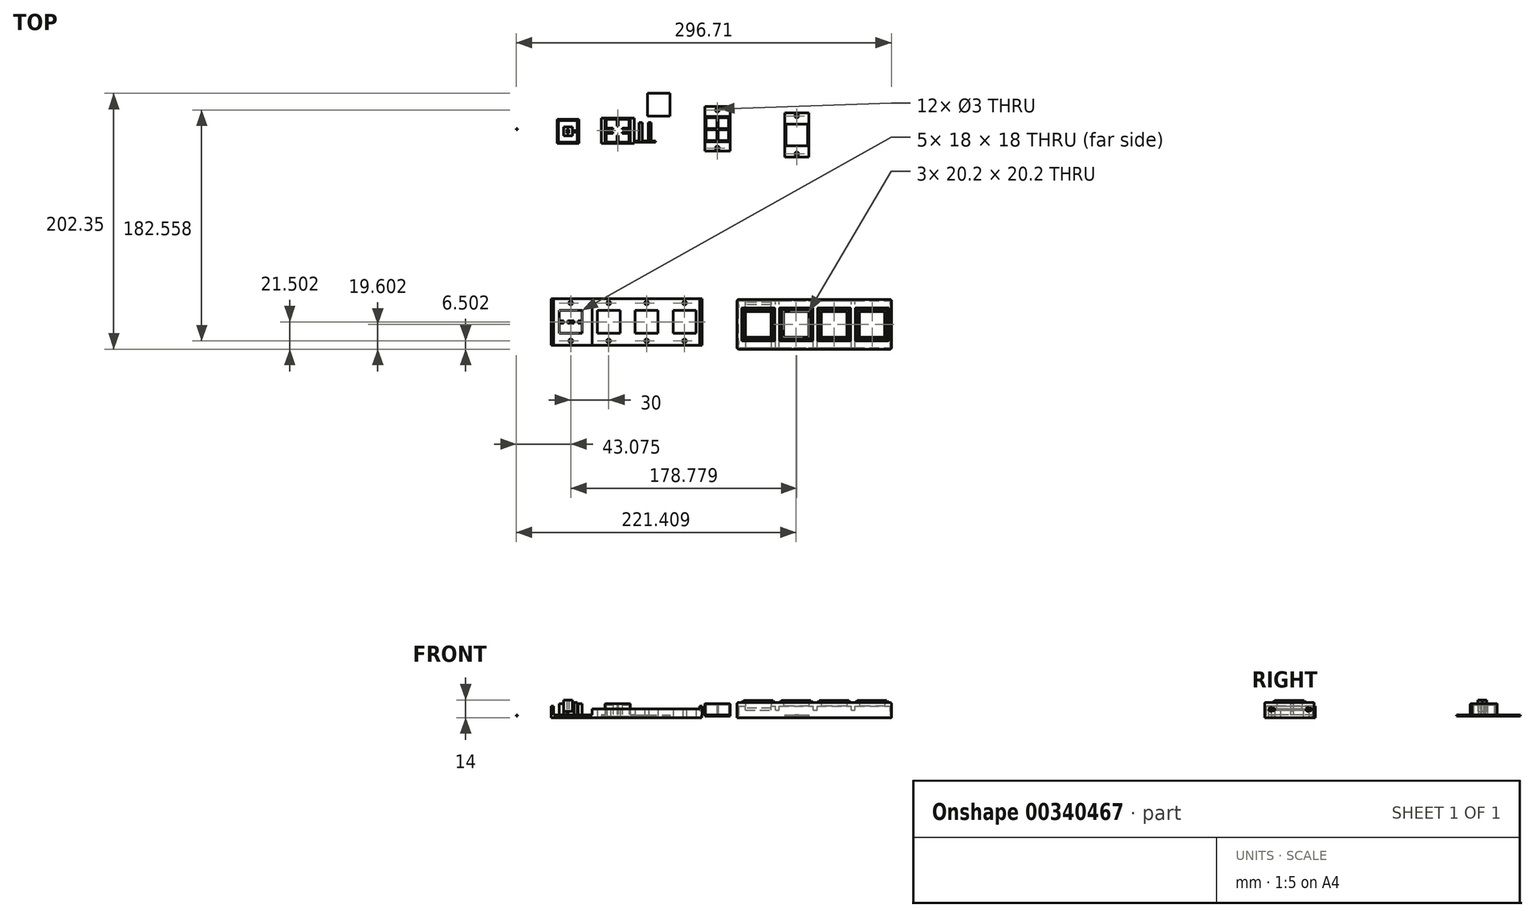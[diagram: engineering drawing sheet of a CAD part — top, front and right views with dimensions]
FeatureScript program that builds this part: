
annotation { "Feature Type Name" : "Feature", "Feature Type Description" : "" }
export const myFeature = defineFeature(function(context is Context, id is Id, definition is map)
    precondition{}
    {
        {
            var Q0;
            Q0=qCreatedBy(makeId("Top.planeOp"),FACE);
            var sketch = newSketch(context, id + "F0", { "sketchPlane" : qUnion([Q0])});
            skPoint(sketch, "E0.middle", {"position": v(0, 0) * mm});
            skLineSegment(sketch, "E1.bottom", {"start": v(10, -10) * mm, "end": v(-10, -10) * mm});
            skLineSegment(sketch, "E1.top", {"start": v(10, 10) * mm, "end": v(-10, 10) * mm});
            skLineSegment(sketch, "E1.left", {"start": v(10, -10) * mm, "end": v(10, 10) * mm});
            skLineSegment(sketch, "E1.right", {"start": v(-10, -10) * mm, "end": v(-10, 10) * mm});
            skSolve(sketch);
        }
        {
            var Q0;
            Q0=makeQuery(id+"F0.imprint","IMPRINT",FACE,{"disambiguationData":[TD([[makeQuery(id+"F0.imprint","IMPRINT",EDGE,{"derivedFrom":sQuery(id+"F0.wireOp",EDGE,"E1.bottom")}),-1.0]])]});
            extrude(context, id + "F1", {"entities" : qUnion([Q0]), "depth" : 10 * mm});
        }
        {
            var Q0;
            Q0=makeQuery(id+"F1.opExtrude","CAP_FACE",FACE,{"disambiguationData":[OSD([sQuery(id+"F0.wireOp",EDGE,"E1.bottom"),sQuery(id+"F0.wireOp",EDGE,"E1.top"),sQuery(id+"F0.wireOp",EDGE,"E1.left"),sQuery(id+"F0.wireOp",EDGE,"E1.right")])],"isStart":true});
            shell(context, id + "F2", {"entities" : qUnion([Q0]), "thickness" : 1 * mm});
        }
        {
            var Q0;
            Q0=qCreatedBy(makeId("Top.planeOp"),FACE);
            var sketch = newSketch(context, id + "F3", { "sketchPlane" : qUnion([Q0])});
            skLineSegment(sketch, "E2.bottom", {"start": v(0.5, -9) * mm, "end": v(-0.5, -9) * mm});
            skLineSegment(sketch, "E2.top", {"start": v(0.5, 9) * mm, "end": v(-0.5, 9) * mm});
            skLineSegment(sketch, "E2.left", {"start": v(0.5, -9) * mm, "end": v(0.5, -0.5) * mm});
            skLineSegment(sketch, "E2.right", {"start": v(-0.5, -9) * mm, "end": v(-0.5, -0.5) * mm});
            skLineSegment(sketch, "E3.bottom", {"start": v(9, 0.5) * mm, "end": v(0.5, 0.5) * mm});
            skLineSegment(sketch, "E3.top", {"start": v(9, -0.5) * mm, "end": v(0.5, -0.5) * mm});
            skLineSegment(sketch, "E3.left", {"start": v(9, 0.5) * mm, "end": v(9, -0.5) * mm});
            skLineSegment(sketch, "E3.right", {"start": v(-9, 0.5) * mm, "end": v(-9, -0.5) * mm});
            skLineSegment(sketch, "E4.trimOffspring", {"start": v(-0.5, 0.5) * mm, "end": v(-0.5, 9) * mm});
            skLineSegment(sketch, "E5.trimOffspring", {"start": v(-0.5, -0.5) * mm, "end": v(-9, -0.5) * mm});
            skLineSegment(sketch, "E6.trimOffspring", {"start": v(0.5, 0.5) * mm, "end": v(0.5, 9) * mm});
            skLineSegment(sketch, "E7.trimOffspring", {"start": v(-0.5, 0.5) * mm, "end": v(-9, 0.5) * mm});
            skSolve(sketch);
        }
        {
            var Q0;
            Q0=qSketchRegion(id+"F3",true);
            extrude(context, id + "F4", {"entities" : qUnion([Q0]), "operationType" : NewBodyOperationType.ADD, "depth" : 9 * mm});
        }
        {
            var Q0;
            Q0=qCreatedBy(makeId("Top.planeOp"),FACE);
            var sketch = newSketch(context, id + "F5", { "sketchPlane" : qUnion([Q0])});
            skLineSegment(sketch, "E8.bottom", {"start": v(-10, -9.5) * mm, "end": v(10, -9.5) * mm});
            skLineSegment(sketch, "E8.top", {"start": v(-10, -17.5) * mm, "end": v(10, -17.5) * mm});
            skLineSegment(sketch, "E8.left", {"start": v(-10, -9.5) * mm, "end": v(-10, -17.5) * mm});
            skLineSegment(sketch, "E8.right", {"start": v(10, -9.5) * mm, "end": v(10, -17.5) * mm});
            skLineSegment(sketch, "E9.bottom", {"start": v(-10, 10) * mm, "end": v(10, 10) * mm});
            skLineSegment(sketch, "E9.top", {"start": v(-10, 18) * mm, "end": v(10, 18) * mm});
            skLineSegment(sketch, "E9.left", {"start": v(-10, 10) * mm, "end": v(-10, 18) * mm});
            skLineSegment(sketch, "E9.right", {"start": v(10, 10) * mm, "end": v(10, 18) * mm});
            skLineSegment(sketch, "E10.bottom", {"start": v(-10, -9.5) * mm, "end": v(-13, -9.5) * mm, "construction": true});
            skLineSegment(sketch, "E10.top", {"start": v(-10, 10) * mm, "end": v(-13, 10) * mm, "construction": true});
            skLineSegment(sketch, "E10.left", {"start": v(-10, -9.5) * mm, "end": v(-10, 10) * mm});
            skLineSegment(sketch, "E10.right", {"start": v(-13, -9.5) * mm, "end": v(-13, 10) * mm, "construction": true});
            skLineSegment(sketch, "E11.bottom", {"start": v(10, -9.5) * mm, "end": v(13, -9.5) * mm, "construction": true});
            skLineSegment(sketch, "E11.top", {"start": v(10, 10) * mm, "end": v(13, 10) * mm, "construction": true});
            skLineSegment(sketch, "E11.left", {"start": v(10, -9.5) * mm, "end": v(10, 10) * mm});
            skLineSegment(sketch, "E11.right", {"start": v(13, -9.5) * mm, "end": v(13, 10) * mm, "construction": true});
            skCircle(sketch, "E12", {"center": v(0, 15) * mm, "radius": 1.5 * mm});
            skCircle(sketch, "E13", {"center": v(0, -15) * mm, "radius": 1.5 * mm});
            skSolve(sketch);
        }
        {
            var Q0;
            Q0=makeQuery(id+"F5.imprint","IMPRINT",FACE,{"disambiguationData":[TD([[makeQuery(id+"F5.imprint","IMPRINT",EDGE,{"derivedFrom":sQuery(id+"F5.wireOp",EDGE,"E10.bottom")}),-1.0]])]});
            var Q1;
            Q1=makeQuery(id+"F5.imprint","IMPRINT",FACE,{"disambiguationData":[TD([[makeQuery(id+"F5.imprint","IMPRINT",EDGE,{"derivedFrom":sQuery(id+"F5.wireOp",EDGE,"E8.bottom")}),-1.0]])]});
            var Q2;
            Q2=makeQuery(id+"F5.imprint","IMPRINT",FACE,{"disambiguationData":[TD([[makeQuery(id+"F5.imprint","IMPRINT",EDGE,{"derivedFrom":sQuery(id+"F5.wireOp",EDGE,"E11.bottom")}),1.0]])]});
            var Q3;
            Q3=makeQuery(id+"F5.imprint","IMPRINT",FACE,{"disambiguationData":[TD([[makeQuery(id+"F5.imprint","IMPRINT",EDGE,{"derivedFrom":sQuery(id+"F5.wireOp",EDGE,"E9.bottom")}),1.0]])]});
            extrude(context, id + "F6", {"entities" : qUnion([Q0, Q1, Q2, Q3]), "operationType" : NewBodyOperationType.ADD, "depth" : 1 * mm});
        }
        {
            var Q0;
            Q0=qCreatedBy(makeId("Top.planeOp"),FACE);
            var sketch = newSketch(context, id + "F7", { "sketchPlane" : qUnion([Q0])});
            skLineSegment(sketch, "E14.bottom", {"start": v(53.3, 4.9) * mm, "end": v(72.3, 4.9) * mm});
            skLineSegment(sketch, "E14.top", {"start": v(53.3, -14.1) * mm, "end": v(72.3, -14.1) * mm});
            skLineSegment(sketch, "E14.left", {"start": v(53.3, 4.9) * mm, "end": v(53.3, -14.1) * mm});
            skLineSegment(sketch, "E14.right", {"start": v(72.3, 4.9) * mm, "end": v(72.3, -14.1) * mm});
            skLineSegment(sketch, "E15.top", {"start": v(53.3, 12.9) * mm, "end": v(72.3, 12.9) * mm});
            skLineSegment(sketch, "E15.left", {"start": v(53.3, 4.9) * mm, "end": v(53.3, 12.9) * mm});
            skLineSegment(sketch, "E15.right", {"start": v(72.3, 4.9) * mm, "end": v(72.3, 12.9) * mm});
            skLineSegment(sketch, "E16.top", {"start": v(53.3, -22.1) * mm, "end": v(72.3, -22.1) * mm});
            skLineSegment(sketch, "E16.left", {"start": v(53.3, -14.1) * mm, "end": v(53.3, -22.1) * mm});
            skLineSegment(sketch, "E16.right", {"start": v(72.3, -14.1) * mm, "end": v(72.3, -22.1) * mm});
            skLineSegment(sketch, "E17.bottom", {"start": v(62.05, 4.9) * mm, "end": v(63.55, 4.9) * mm, "construction": true});
            skLineSegment(sketch, "E17.top", {"start": v(62.05, -14.1) * mm, "end": v(63.55, -14.1) * mm, "construction": true});
            skLineSegment(sketch, "E17.left", {"start": v(62.05, 4.9) * mm, "end": v(62.05, -14.1) * mm, "construction": true});
            skLineSegment(sketch, "E17.right", {"start": v(63.55, 4.9) * mm, "end": v(63.55, -14.1) * mm, "construction": true});
            skLineSegment(sketch, "E18.bottom", {"start": v(53.3, -3.86) * mm, "end": v(54.3, -3.86) * mm, "construction": true});
            skLineSegment(sketch, "E18.top", {"start": v(53.3, -5.36) * mm, "end": v(57.43, -5.36) * mm, "construction": true});
            skLineSegment(sketch, "E18.left", {"start": v(53.3, -3.86) * mm, "end": v(53.3, -5.36) * mm, "construction": true});
            skLineSegment(sketch, "E18.right", {"start": v(72.3, -3.86) * mm, "end": v(72.3, -5.36) * mm, "construction": true});
            skLineSegment(sketch, "E19.0", {"start": v(54.3, 3.9) * mm, "end": v(71.3, 3.9) * mm});
            skLineSegment(sketch, "E19.1", {"start": v(54.3, 3.9) * mm, "end": v(54.3, -13.1) * mm});
            skLineSegment(sketch, "E19.2", {"start": v(54.3, -13.1) * mm, "end": v(71.3, -13.1) * mm});
            skLineSegment(sketch, "E19.3", {"start": v(71.3, 3.9) * mm, "end": v(71.3, -13.1) * mm});
            skCircle(sketch, "E20", {"center": v(62.8, 10.4) * mm, "radius": 1.5 * mm});
            skPoint(sketch, "E21", {"position": v(62.8, 4.9) * mm});
            skLineSegment(sketch, "E22.bottom", {"start": v(63.3, -5.1) * mm, "end": v(62.3, -5.1) * mm, "construction": true});
            skLineSegment(sketch, "E22.top", {"start": v(63.3, -4.1) * mm, "end": v(62.3, -4.1) * mm, "construction": true});
            skLineSegment(sketch, "E22.left", {"start": v(63.3, -5.1) * mm, "end": v(63.3, -4.1) * mm, "construction": true});
            skLineSegment(sketch, "E22.right", {"start": v(62.3, -5.1) * mm, "end": v(62.3, -4.1) * mm, "construction": true});
            skPoint(sketch, "E22.middle", {"position": v(62.8, -4.6) * mm});
            skPoint(sketch, "E22.middle.positionSnap0", {"position": v(62.05, -4.6) * mm});
            skPoint(sketch, "E22.middle.positionSnap1", {"position": v(62.8, -3.86) * mm});
            skPoint(sketch, "E22.centerSnap0", {"position": v(62.05, -4.6) * mm});
            skPoint(sketch, "E22.centerSnap1", {"position": v(62.8, -3.86) * mm});
            skCircle(sketch, "E23", {"center": v(62.8, -19.6) * mm, "radius": 1.5 * mm});
            skPoint(sketch, "E23.centerSnap0", {"position": v(62.8, 12.9) * mm});
            skLineSegment(sketch, "E24.bottom", {"start": v(57.43, 3.9) * mm, "end": v(58.93, 3.9) * mm});
            skLineSegment(sketch, "E24.top", {"start": v(57.43, -13.1) * mm, "end": v(58.93, -13.1) * mm});
            skLineSegment(sketch, "E24.left", {"start": v(57.43, 3.9) * mm, "end": v(57.43, -3.86) * mm});
            skLineSegment(sketch, "E24.right", {"start": v(58.93, 3.9) * mm, "end": v(58.93, -3.86) * mm});
            skLineSegment(sketch, "E25.bottom", {"start": v(66.68, 3.9) * mm, "end": v(68.18, 3.9) * mm});
            skLineSegment(sketch, "E25.top", {"start": v(66.68, -13.1) * mm, "end": v(68.18, -13.1) * mm});
            skLineSegment(sketch, "E25.left", {"start": v(66.68, 3.9) * mm, "end": v(66.68, -3.86) * mm});
            skLineSegment(sketch, "E25.right", {"start": v(68.18, 3.9) * mm, "end": v(68.18, -3.86) * mm});
            skLineSegment(sketch, "E26.bottom", {"start": v(54.3, -3.86) * mm, "end": v(57.43, -3.86) * mm});
            skLineSegment(sketch, "E26.top", {"start": v(54.3, -5.36) * mm, "end": v(57.43, -5.36) * mm});
            skLineSegment(sketch, "E26.left", {"start": v(54.3, -3.86) * mm, "end": v(54.3, -5.36) * mm});
            skLineSegment(sketch, "E26.right", {"start": v(71.3, -3.86) * mm, "end": v(71.3, -5.36) * mm});
            skLineSegment(sketch, "E27.trimOffspring", {"start": v(58.93, -3.86) * mm, "end": v(66.68, -3.86) * mm, "construction": true});
            skLineSegment(sketch, "E28.trimOffspring", {"start": v(58.93, -3.86) * mm, "end": v(66.68, -3.86) * mm});
            skLineSegment(sketch, "E29.trimOffspring", {"start": v(57.43, -5.36) * mm, "end": v(57.43, -13.1) * mm});
            skLineSegment(sketch, "E30.trimOffspring", {"start": v(58.93, -5.36) * mm, "end": v(58.93, -13.1) * mm});
            skLineSegment(sketch, "E31.trimOffspring", {"start": v(58.93, -5.36) * mm, "end": v(66.68, -5.36) * mm, "construction": true});
            skLineSegment(sketch, "E32.trimOffspring", {"start": v(58.93, -5.36) * mm, "end": v(66.68, -5.36) * mm});
            skLineSegment(sketch, "E33.trimOffspring", {"start": v(68.18, -3.86) * mm, "end": v(72.3, -3.86) * mm, "construction": true});
            skLineSegment(sketch, "E34.trimOffspring", {"start": v(66.68, -5.36) * mm, "end": v(66.68, -13.1) * mm});
            skLineSegment(sketch, "E35.trimOffspring", {"start": v(68.18, -5.36) * mm, "end": v(72.3, -5.36) * mm, "construction": true});
            skLineSegment(sketch, "E36.trimOffspring", {"start": v(68.18, -5.36) * mm, "end": v(68.18, -13.1) * mm});
            skLineSegment(sketch, "E37.trimOffspring", {"start": v(68.18, -3.86) * mm, "end": v(71.3, -3.86) * mm});
            skLineSegment(sketch, "E38.trimOffspring", {"start": v(68.18, -5.36) * mm, "end": v(71.3, -5.36) * mm});
            skLineSegment(sketch, "E39.bottom", {"start": v(55.04, 3.07) * mm, "end": v(61.04, 3.07) * mm, "construction": true});
            skLineSegment(sketch, "E39.top", {"start": v(55.04, -2.93) * mm, "end": v(61.04, -2.93) * mm, "construction": true});
            skLineSegment(sketch, "E39.left", {"start": v(55.04, 3.07) * mm, "end": v(55.04, -2.93) * mm, "construction": true});
            skLineSegment(sketch, "E39.right", {"start": v(61.04, 3.07) * mm, "end": v(61.04, -2.93) * mm, "construction": true});
            skLineSegment(sketch, "E40.bottom", {"start": v(64.3, 3.07) * mm, "end": v(70.3, 3.07) * mm, "construction": true});
            skLineSegment(sketch, "E40.top", {"start": v(64.3, -2.93) * mm, "end": v(70.3, -2.93) * mm, "construction": true});
            skLineSegment(sketch, "E40.left", {"start": v(64.3, 3.07) * mm, "end": v(64.3, -2.93) * mm, "construction": true});
            skLineSegment(sketch, "E40.right", {"start": v(70.3, 3.07) * mm, "end": v(70.3, -2.93) * mm, "construction": true});
            skSolve(sketch);
        }
        {
            var Q0;
            Q0=makeQuery(id+"F7.imprint","IMPRINT",FACE,{"disambiguationData":[TD([[makeQuery(id+"F7.imprint","IMPRINT",EDGE,{"derivedFrom":sQuery(id+"F7.wireOp",EDGE,"E14.left")}),1.0]])]});
            var Q1;
            Q1=makeQuery(id+"F7.imprint","IMPRINT",FACE,{"disambiguationData":[TD([[makeQuery(id+"F7.imprint","IMPRINT",EDGE,{"derivedFrom":sQuery(id+"F7.wireOp",EDGE,"E14.bottom")}),1.0]])]});
            var Q2;
            Q2=makeQuery(id+"F7.imprint","IMPRINT",FACE,{"disambiguationData":[TD([[makeQuery(id+"F7.imprint","IMPRINT",EDGE,{"derivedFrom":sQuery(id+"F7.wireOp",EDGE,"MVN2uy9p-aqT3-YTcf-EiQD-pbnfHAAz3MAc.bottom")}),-1.0]])]});
            var Q3;
            Q3=makeQuery(id+"F7.imprint","IMPRINT",FACE,{"disambiguationData":[TD([[makeQuery(id+"F7.imprint","IMPRINT",EDGE,{"derivedFrom":sQuery(id+"F7.wireOp",EDGE,"sKF5d9FJ-0LFq-fu9g-diTO-PrwaPXYM0bzY.bottom")}),-1.0]])]});
            var Q4;
            Q4=makeQuery(id+"F7.imprint","IMPRINT",FACE,{"disambiguationData":[TD([[makeQuery(id+"F7.imprint","IMPRINT",EDGE,{"derivedFrom":sQuery(id+"F7.wireOp",EDGE,"E14.top")}),-1.0]])]});
            var Q5;
            Q5=makeQuery(id+"F7.imprint","IMPRINT",FACE,{"disambiguationData":[TD([[makeQuery(id+"F7.imprint","IMPRINT",EDGE,{"derivedFrom":sQuery(id+"F7.wireOp",EDGE,"E24.bottom")}),-1.0]])]});
            var Q6;
            Q6=makeQuery(id+"F7.imprint","IMPRINT",FACE,{"disambiguationData":[TD([[makeQuery(id+"F7.imprint","IMPRINT",EDGE,{"derivedFrom":sQuery(id+"F7.wireOp",EDGE,"E25.bottom")}),-1.0]])]});
            extrude(context, id + "F8", {"entities" : qUnion([Q0, Q1, Q2, Q3, Q4, Q5, Q6]), "depth" : 1 * mm});
        }
        {
            var Q0;
            Q0=qCreatedBy(makeId("Top.planeOp"),FACE);
            var sketch = newSketch(context, id + "F9", { "sketchPlane" : qUnion([Q0])});
            skLineSegment(sketch, "E41.bottom", {"start": v(-88.88, 8.7) * mm, "end": v(-68.88, 8.7) * mm});
            skLineSegment(sketch, "E41.top", {"start": v(-88.88, -11.3) * mm, "end": v(-68.88, -11.3) * mm});
            skLineSegment(sketch, "E41.left", {"start": v(-88.88, 8.7) * mm, "end": v(-88.88, -11.3) * mm});
            skLineSegment(sketch, "E41.right", {"start": v(-68.88, 8.7) * mm, "end": v(-68.88, -11.3) * mm});
            skSolve(sketch);
        }
        {
            var Q0;
            Q0=makeQuery(id+"F9.imprint","IMPRINT",FACE,{"disambiguationData":[TD([[makeQuery(id+"F9.imprint","IMPRINT",EDGE,{"derivedFrom":sQuery(id+"F9.wireOp",EDGE,"E41.bottom")}),-1.0]])]});
            extrude(context, id + "F10", {"entities" : qUnion([Q0]), "depth" : 10 * mm});
        }
        {
            var Q0;
            Q0=makeQuery(id+"F15.boolean.opBoolean","MERGE",FACE,{"derivedFrom":[makeQuery(id+"F10.opExtrude","CAP_FACE",FACE,{"disambiguationData":[OSD([sQuery(id+"F9.wireOp",EDGE,"E41.bottom"),sQuery(id+"F9.wireOp",EDGE,"E41.top"),sQuery(id+"F9.wireOp",EDGE,"E41.left"),sQuery(id+"F9.wireOp",EDGE,"E41.right")])],"isStart":true}),makeQuery(id+"F15.opExtrude","CAP_FACE",FACE,{"disambiguationData":[OSD([sQuery(id+"F14.wireOp",EDGE,"E49.bottom"),sQuery(id+"F14.wireOp",EDGE,"E49.top"),sQuery(id+"F14.wireOp",EDGE,"E49.left"),sQuery(id+"F14.wireOp",EDGE,"E49.right"),sQuery(id+"F14.wireOp",EDGE,"E50.trimOffspring"),sQuery(id+"F14.wireOp",EDGE,"E52.trimOffspring"),sQuery(id+"F14.wireOp",EDGE,"E54"),sQuery(id+"F14.wireOp",EDGE,"E55"),sQuery(id+"F14.wireOp",EDGE,"E56.bottom"),sQuery(id+"F14.wireOp",EDGE,"E56.top"),sQuery(id+"F14.wireOp",EDGE,"E56.left"),sQuery(id+"F14.wireOp",EDGE,"E57.bottom"),sQuery(id+"F14.wireOp",EDGE,"E57.top"),sQuery(id+"F14.wireOp",EDGE,"E57.left"),sQuery(id+"F14.wireOp",EDGE,"E58.bottom"),sQuery(id+"F14.wireOp",EDGE,"E58.top"),sQuery(id+"F14.wireOp",EDGE,"E58.right"),sQuery(id+"F14.wireOp",EDGE,"E59.bottom"),sQuery(id+"F14.wireOp",EDGE,"E59.top"),sQuery(id+"F14.wireOp",EDGE,"E59.right")])],"isStart":true})]});
            var sketch = newSketch(context, id + "F11", { "sketchPlane" : qUnion([Q0])});
            skLineSegment(sketch, "E42.bottom", {"start": v(-88.88, 11.3) * mm, "end": v(-68.88, 11.3) * mm});
            skLineSegment(sketch, "E42.top", {"start": v(-88.88, 14.3) * mm, "end": v(-68.88, 14.3) * mm, "construction": true});
            skLineSegment(sketch, "E42.left", {"start": v(-88.88, 11.3) * mm, "end": v(-88.88, 14.3) * mm, "construction": true});
            skLineSegment(sketch, "E42.right", {"start": v(-68.88, 11.3) * mm, "end": v(-68.88, 14.3) * mm, "construction": true});
            skLineSegment(sketch, "E43.bottom", {"start": v(-88.88, -8.7) * mm, "end": v(-68.88, -8.7) * mm});
            skLineSegment(sketch, "E43.top", {"start": v(-88.88, -11.7) * mm, "end": v(-68.88, -11.7) * mm});
            skLineSegment(sketch, "E43.left", {"start": v(-88.88, -8.7) * mm, "end": v(-88.88, -11.7) * mm, "construction": true});
            skLineSegment(sketch, "E43.right", {"start": v(-68.88, -8.7) * mm, "end": v(-68.88, -11.7) * mm, "construction": true});
            skLineSegment(sketch, "E44.bottom", {"start": v(-88.88, -8.7) * mm, "end": v(-91.88, -8.7) * mm});
            skLineSegment(sketch, "E44.top", {"start": v(-88.88, 11.3) * mm, "end": v(-91.88, 11.3) * mm});
            skLineSegment(sketch, "E44.left", {"start": v(-88.88, -8.7) * mm, "end": v(-88.88, 11.3) * mm});
            skLineSegment(sketch, "E44.right", {"start": v(-91.88, -8.7) * mm, "end": v(-91.88, 11.3) * mm});
            skLineSegment(sketch, "E45.bottom", {"start": v(-68.88, -8.7) * mm, "end": v(-65.88, -8.7) * mm});
            skLineSegment(sketch, "E45.top", {"start": v(-68.88, 11.3) * mm, "end": v(-65.88, 11.3) * mm});
            skLineSegment(sketch, "E45.left", {"start": v(-68.88, -8.7) * mm, "end": v(-68.88, 11.3) * mm});
            skLineSegment(sketch, "E45.right", {"start": v(-65.88, -8.7) * mm, "end": v(-65.88, 11.3) * mm});
            skLineSegment(sketch, "E46.bottom", {"start": v(-88.88, -11.7) * mm, "end": v(-68.88, -11.7) * mm, "construction": true});
            skLineSegment(sketch, "E46.top", {"start": v(-88.88, -16.7) * mm, "end": v(-68.88, -16.7) * mm, "construction": true});
            skLineSegment(sketch, "E46.left", {"start": v(-88.88, -11.7) * mm, "end": v(-88.88, -16.7) * mm, "construction": true});
            skLineSegment(sketch, "E46.right", {"start": v(-68.88, -11.7) * mm, "end": v(-68.88, -16.7) * mm, "construction": true});
            skCircle(sketch, "E47", {"center": v(-78.88, -13.7) * mm, "radius": 1.5 * mm, "construction": true});
            skSolve(sketch);
        }
        {
            var Q0;
            Q0=qSketchRegion(id+"F11",true);
            extrude(context, id + "F12", {"entities" : qUnion([Q0]), "operationType" : NewBodyOperationType.ADD, "oppositeDirection" : true, "depth" : 0.95 * mm});
        }
        {
            var Q0;
            Q0=makeQuery(id+"F10.opExtrude","CAP_FACE",FACE,{"disambiguationData":[OSD([sQuery(id+"F9.wireOp",EDGE,"E41.bottom"),sQuery(id+"F9.wireOp",EDGE,"E41.top"),sQuery(id+"F9.wireOp",EDGE,"E41.left"),sQuery(id+"F9.wireOp",EDGE,"E41.right")])],"isStart":true});
            shell(context, id + "F13", {"entities" : qUnion([Q0]), "thickness" : 1 * mm});
        }
        {
            var Q0;
            Q0=qCreatedBy(makeId("Top.planeOp"),FACE);
            var sketch = newSketch(context, id + "F14", { "sketchPlane" : qUnion([Q0])});
            skLineSegment(sketch, "E48.bottom", {"start": v(-87.88, -0.2) * mm, "end": v(-79.38, -0.2) * mm, "construction": true});
            skLineSegment(sketch, "E48.top", {"start": v(-87.88, -2.4) * mm, "end": v(-79.38, -2.4) * mm, "construction": true});
            skLineSegment(sketch, "E48.left", {"start": v(-87.88, -0.2) * mm, "end": v(-87.88, -2.4) * mm, "construction": true});
            skLineSegment(sketch, "E48.right", {"start": v(-69.88, -0.2) * mm, "end": v(-69.88, -2.4) * mm, "construction": true});
            skLineSegment(sketch, "E49.bottom", {"start": v(-79.38, 7.7) * mm, "end": v(-78.38, 7.7) * mm});
            skLineSegment(sketch, "E49.top", {"start": v(-79.38, -10.3) * mm, "end": v(-78.38, -10.3) * mm});
            skLineSegment(sketch, "E49.left", {"start": v(-79.38, 7.7) * mm, "end": v(-79.38, -0.2) * mm});
            skLineSegment(sketch, "E49.right", {"start": v(-78.38, 7.7) * mm, "end": v(-78.38, -0.2) * mm});
            skLineSegment(sketch, "E50.trimOffspring", {"start": v(-79.38, -10.3) * mm, "end": v(-79.38, -2.4) * mm});
            skLineSegment(sketch, "E51.trimOffspring", {"start": v(-78.38, -0.2) * mm, "end": v(-69.88, -0.2) * mm, "construction": true});
            skLineSegment(sketch, "E52.trimOffspring", {"start": v(-78.38, -2.4) * mm, "end": v(-78.38, -10.3) * mm});
            skLineSegment(sketch, "E53.trimOffspring", {"start": v(-78.38, -2.4) * mm, "end": v(-69.88, -2.4) * mm, "construction": true});
            skLineSegment(sketch, "E54", {"start": v(-79.38, -2.4) * mm, "end": v(-79.38, -0.2) * mm});
            skLineSegment(sketch, "E55", {"start": v(-78.38, -2.4) * mm, "end": v(-78.38, -0.2) * mm});
            skLineSegment(sketch, "E56.bottom", {"start": v(-87.88, -2.4) * mm, "end": v(-79.38, -2.4) * mm});
            skLineSegment(sketch, "E56.top", {"start": v(-87.88, -3.3) * mm, "end": v(-79.38, -3.3) * mm});
            skLineSegment(sketch, "E56.left", {"start": v(-87.88, -2.4) * mm, "end": v(-87.88, -3.3) * mm});
            skLineSegment(sketch, "E56.right", {"start": v(-79.38, -2.4) * mm, "end": v(-79.38, -3.3) * mm});
            skLineSegment(sketch, "E57.bottom", {"start": v(-87.88, -0.2) * mm, "end": v(-79.38, -0.2) * mm});
            skLineSegment(sketch, "E57.top", {"start": v(-87.88, 0.7) * mm, "end": v(-79.38, 0.7) * mm});
            skLineSegment(sketch, "E57.left", {"start": v(-87.88, -0.2) * mm, "end": v(-87.88, 0.7) * mm});
            skLineSegment(sketch, "E57.right", {"start": v(-79.38, -0.2) * mm, "end": v(-79.38, 0.7) * mm});
            skLineSegment(sketch, "E58.bottom", {"start": v(-78.38, -3.3) * mm, "end": v(-69.88, -3.3) * mm});
            skLineSegment(sketch, "E58.top", {"start": v(-78.38, -2.4) * mm, "end": v(-69.88, -2.4) * mm});
            skLineSegment(sketch, "E58.left", {"start": v(-78.38, -3.3) * mm, "end": v(-78.38, -2.4) * mm});
            skLineSegment(sketch, "E58.right", {"start": v(-69.88, -3.3) * mm, "end": v(-69.88, -2.4) * mm});
            skLineSegment(sketch, "E59.bottom", {"start": v(-78.38, -0.2) * mm, "end": v(-69.88, -0.2) * mm});
            skLineSegment(sketch, "E59.top", {"start": v(-78.38, 0.7) * mm, "end": v(-69.88, 0.7) * mm});
            skLineSegment(sketch, "E59.left", {"start": v(-78.38, -0.2) * mm, "end": v(-78.38, 0.7) * mm});
            skLineSegment(sketch, "E59.right", {"start": v(-69.88, -0.2) * mm, "end": v(-69.88, 0.7) * mm});
            skSolve(sketch);
        }
        {
            var Q0;
            Q0=makeQuery(id+"F14.imprint","IMPRINT",FACE,{"disambiguationData":[TD([[makeQuery(id+"F14.imprint","IMPRINT",EDGE,{"derivedFrom":sQuery(id+"F14.wireOp",EDGE,"E49.bottom")}),-1.0]])]});
            var Q1;
            Q1=makeQuery(id+"F14.imprint","IMPRINT",FACE,{"disambiguationData":[TD([[makeQuery(id+"F14.imprint","IMPRINT",EDGE,{"derivedFrom":sQuery(id+"F14.wireOp",EDGE,"E56.bottom")}),-1.0]])]});
            var Q2;
            Q2=makeQuery(id+"F14.imprint","IMPRINT",FACE,{"disambiguationData":[TD([[makeQuery(id+"F14.imprint","IMPRINT",EDGE,{"derivedFrom":sQuery(id+"F14.wireOp",EDGE,"E57.bottom")}),1.0]])]});
            var Q3;
            Q3=makeQuery(id+"F14.imprint","IMPRINT",FACE,{"disambiguationData":[TD([[makeQuery(id+"F14.imprint","IMPRINT",EDGE,{"derivedFrom":sQuery(id+"F14.wireOp",EDGE,"E59.bottom")}),1.0]])]});
            var Q4;
            Q4=makeQuery(id+"F14.imprint","IMPRINT",FACE,{"disambiguationData":[TD([[makeQuery(id+"F14.imprint","IMPRINT",EDGE,{"derivedFrom":sQuery(id+"F14.wireOp",EDGE,"E58.bottom")}),1.0]])]});
            var Q5;
            Q5=sQuery(id+"F14.wireOp",EDGE,"E49.left");
            var Q6;
            Q6=sQuery(id+"F14.wireOp",EDGE,"E50.trimOffspring");
            var Q7;
            Q7=sQuery(id+"F14.wireOp",EDGE,"E48.top");
            var Q8;
            Q8=sQuery(id+"F14.wireOp",EDGE,"E51.trimOffspring");
            var Q9;
            Q9=sQuery(id+"F14.wireOp",EDGE,"E49.bottom");
            var Q10;
            Q10=sQuery(id+"F14.wireOp",EDGE,"E49.right");
            var Q11;
            Q11=sQuery(id+"F14.wireOp",EDGE,"E49.top");
            var Q12;
            Q12=sQuery(id+"F14.wireOp",EDGE,"E48.bottom");
            var Q13;
            Q13=sQuery(id+"F14.wireOp",EDGE,"E52.trimOffspring");
            var Q14;
            Q14=sQuery(id+"F14.wireOp",EDGE,"E53.trimOffspring");
            var Q15;
            Q15=sQuery(id+"F14.wireOp",EDGE,"E48.right");
            var Q16;
            Q16=sQuery(id+"F14.wireOp",EDGE,"E48.left");
            extrude(context, id + "F15", {"entities" : qUnion([Q0, Q1, Q2, Q3, Q4]), "operationType" : NewBodyOperationType.ADD, "surfaceEntities" : qUnion([Q5, Q6, Q7, Q8, Q9, Q10, Q11, Q12, Q13, Q14, Q15, Q16]), "depth" : 9 * mm});
        }
        {
            var Q0;
            Q0=makeQuery(id+"F15.boolean.opBoolean","MERGE",FACE,{"derivedFrom":[makeQuery(id+"F10.opExtrude","CAP_FACE",FACE,{"disambiguationData":[OSD([sQuery(id+"F9.wireOp",EDGE,"E41.bottom"),sQuery(id+"F9.wireOp",EDGE,"E41.top"),sQuery(id+"F9.wireOp",EDGE,"E41.left"),sQuery(id+"F9.wireOp",EDGE,"E41.right")])],"isStart":true}),makeQuery(id+"F15.opExtrude","CAP_FACE",FACE,{"disambiguationData":[OSD([sQuery(id+"F14.wireOp",EDGE,"E48.bottom"),sQuery(id+"F14.wireOp",EDGE,"E48.top"),sQuery(id+"F14.wireOp",EDGE,"E48.left"),sQuery(id+"F14.wireOp",EDGE,"E48.right"),sQuery(id+"F14.wireOp",EDGE,"E49.bottom"),sQuery(id+"F14.wireOp",EDGE,"E49.top"),sQuery(id+"F14.wireOp",EDGE,"E49.left"),sQuery(id+"F14.wireOp",EDGE,"E49.right"),sQuery(id+"F14.wireOp",EDGE,"E50.trimOffspring"),sQuery(id+"F14.wireOp",EDGE,"E51.trimOffspring"),sQuery(id+"F14.wireOp",EDGE,"E52.trimOffspring"),sQuery(id+"F14.wireOp",EDGE,"E53.trimOffspring")])],"isStart":true})]});
            var sketch = newSketch(context, id + "F16", { "sketchPlane" : qUnion([Q0])});
            skLineSegment(sketch, "E60.bottom", {"start": v(-75.28, -2.3) * mm, "end": v(-82.48, -2.3) * mm});
            skLineSegment(sketch, "E60.top", {"start": v(-75.28, 4.9) * mm, "end": v(-82.48, 4.9) * mm});
            skLineSegment(sketch, "E60.left", {"start": v(-75.28, -2.3) * mm, "end": v(-75.28, 4.9) * mm});
            skLineSegment(sketch, "E60.right", {"start": v(-82.48, -2.3) * mm, "end": v(-82.48, 4.9) * mm});
            skPoint(sketch, "E60.middle.positionSnap1", {"position": v(-88.88, 1.8) * mm});
            skSolve(sketch);
        }
        {
            var Q0;
            {var subQ1=makeQuery(id+"F15.opExtrude","CAP_EDGE",EDGE,{"disambiguationData":[OSD([sQuery(id+"F14.wireOp",EDGE,"E49.right")])],"isStart":true});var subQ3=sQuery(id+"F16.wireOp",EDGE,"E60.bottom");var subQ4=makeQuery(id+"F16.imprint","INTERSECT",VERTEX,{"derivedFrom":[subQ1,subQ3]});Q0=makeQuery(id+"F16.imprint","IMPRINT",FACE,{"disambiguationData":[TD([[makeQuery(id+"F16.imprint","IMPRINT",EDGE,{"disambiguationData":[TD([[subQ4,-1.0]])],"derivedFrom":subQ3}),-1.0]])]});}
            extrude(context, id + "F17", {"entities" : qUnion([Q0]), "operationType" : NewBodyOperationType.REMOVE, "oppositeDirection" : true, "depth" : 9 * mm});
        }
        {
            var Q0;
            Q0=qCreatedBy(makeId("Top.planeOp"),FACE);
            var sketch = newSketch(context, id + "F18", { "sketchPlane" : qUnion([Q0])});
            skLineSegment(sketch, "E61.bottom", {"start": v(-126.7, 7.66) * mm, "end": v(-109.7, 7.66) * mm});
            skLineSegment(sketch, "E61.top", {"start": v(-126.7, -11.34) * mm, "end": v(-109.7, -11.34) * mm});
            skLineSegment(sketch, "E61.left", {"start": v(-126.7, 7.66) * mm, "end": v(-126.7, -11.34) * mm});
            skLineSegment(sketch, "E61.right", {"start": v(-109.7, 7.66) * mm, "end": v(-109.7, -11.34) * mm});
            skLineSegment(sketch, "E62.top", {"start": v(-126.7, 15.66) * mm, "end": v(-109.7, 15.66) * mm});
            skLineSegment(sketch, "E62.left", {"start": v(-126.7, 7.66) * mm, "end": v(-126.7, 15.66) * mm});
            skLineSegment(sketch, "E62.right", {"start": v(-109.7, 7.66) * mm, "end": v(-109.7, 15.66) * mm});
            skLineSegment(sketch, "E63.top", {"start": v(-126.7, -19.34) * mm, "end": v(-109.7, -19.34) * mm});
            skLineSegment(sketch, "E63.left", {"start": v(-126.7, -11.34) * mm, "end": v(-126.7, -19.34) * mm});
            skLineSegment(sketch, "E63.right", {"start": v(-109.7, -11.34) * mm, "end": v(-109.7, -19.34) * mm});
            skLineSegment(sketch, "E64.bottom", {"start": v(-118.94, 7.66) * mm, "end": v(-117.44, 7.66) * mm, "construction": true});
            skLineSegment(sketch, "E64.top", {"start": v(-118.94, -11.34) * mm, "end": v(-117.44, -11.34) * mm, "construction": true});
            skLineSegment(sketch, "E64.left", {"start": v(-118.94, 7.66) * mm, "end": v(-118.94, -1.09) * mm, "construction": true});
            skLineSegment(sketch, "E64.right", {"start": v(-117.44, 7.66) * mm, "end": v(-117.44, -1.09) * mm, "construction": true});
            skLineSegment(sketch, "E65.bottom", {"start": v(-126.7, -1.09) * mm, "end": v(-123.07, -1.09) * mm, "construction": true});
            skLineSegment(sketch, "E65.top", {"start": v(-126.7, -2.59) * mm, "end": v(-123.07, -2.59) * mm, "construction": true});
            skLineSegment(sketch, "E65.left", {"start": v(-126.7, -1.09) * mm, "end": v(-126.7, -2.59) * mm, "construction": true});
            skLineSegment(sketch, "E65.right", {"start": v(-109.7, -1.09) * mm, "end": v(-109.7, -2.59) * mm, "construction": true});
            skLineSegment(sketch, "E66.0", {"start": v(-125.7, 6.66) * mm, "end": v(-110.7, 6.66) * mm});
            skLineSegment(sketch, "E66.1", {"start": v(-125.7, 6.66) * mm, "end": v(-125.7, -10.34) * mm});
            skLineSegment(sketch, "E66.2", {"start": v(-125.7, -10.34) * mm, "end": v(-110.7, -10.34) * mm});
            skLineSegment(sketch, "E66.3", {"start": v(-110.7, 6.66) * mm, "end": v(-110.7, -10.34) * mm});
            skCircle(sketch, "E67", {"center": v(-118.2, 13.16) * mm, "radius": 1.5 * mm});
            skPoint(sketch, "E68", {"position": v(-118.2, 7.66) * mm});
            skCircle(sketch, "E69", {"center": v(-118.2, -16.84) * mm, "radius": 1.5 * mm});
            skPoint(sketch, "E69.centerSnap0", {"position": v(-118.2, 15.66) * mm});
            skLineSegment(sketch, "E70.bottom", {"start": v(-125.3, 5.6) * mm, "end": v(-119.3, 5.6) * mm, "construction": true});
            skLineSegment(sketch, "E70.top", {"start": v(-125.3, -0.4) * mm, "end": v(-119.3, -0.4) * mm, "construction": true});
            skLineSegment(sketch, "E70.left", {"start": v(-125.3, 5.6) * mm, "end": v(-125.3, -0.4) * mm, "construction": true});
            skLineSegment(sketch, "E70.right", {"start": v(-119.3, 5.6) * mm, "end": v(-119.3, -0.4) * mm, "construction": true});
            skLineSegment(sketch, "E71.bottom", {"start": v(-101.6, 6.16) * mm, "end": v(-94.6, 6.16) * mm, "construction": true});
            skLineSegment(sketch, "E71.top", {"start": v(-101.6, -0.84) * mm, "end": v(-94.6, -0.84) * mm, "construction": true});
            skLineSegment(sketch, "E71.left", {"start": v(-101.6, 6.16) * mm, "end": v(-101.6, -0.84) * mm, "construction": true});
            skLineSegment(sketch, "E71.right", {"start": v(-94.6, 6.16) * mm, "end": v(-94.6, -0.84) * mm, "construction": true});
            skLineSegment(sketch, "E72.trimOffspring", {"start": v(-117.44, -1.09) * mm, "end": v(-114.82, -1.09) * mm, "construction": true});
            skLineSegment(sketch, "E73.trimOffspring", {"start": v(-117.44, -2.59) * mm, "end": v(-114.82, -2.59) * mm, "construction": true});
            skLineSegment(sketch, "E74.trimOffspring", {"start": v(-118.94, -2.59) * mm, "end": v(-118.94, -11.34) * mm, "construction": true});
            skLineSegment(sketch, "E75.trimOffspring", {"start": v(-117.44, -2.59) * mm, "end": v(-117.44, -11.34) * mm, "construction": true});
            skLineSegment(sketch, "E76.bottom", {"start": v(-123.07, 6.66) * mm, "end": v(-121.57, 6.66) * mm});
            skLineSegment(sketch, "E76.top", {"start": v(-123.07, -10.34) * mm, "end": v(-121.57, -10.34) * mm});
            skLineSegment(sketch, "E76.left", {"start": v(-123.07, 6.66) * mm, "end": v(-123.07, -1.09) * mm});
            skLineSegment(sketch, "E76.right", {"start": v(-121.57, 6.66) * mm, "end": v(-121.57, -1.09) * mm});
            skLineSegment(sketch, "E77.bottom", {"start": v(-114.82, 6.66) * mm, "end": v(-113.32, 6.66) * mm});
            skLineSegment(sketch, "E77.top", {"start": v(-114.82, -10.34) * mm, "end": v(-113.32, -10.34) * mm});
            skLineSegment(sketch, "E77.left", {"start": v(-114.82, 6.66) * mm, "end": v(-114.82, -1.09) * mm});
            skLineSegment(sketch, "E77.right", {"start": v(-113.32, 6.66) * mm, "end": v(-113.32, -1.09) * mm});
            skLineSegment(sketch, "E78.bottom", {"start": v(-125.7, -1.09) * mm, "end": v(-123.07, -1.09) * mm});
            skLineSegment(sketch, "E78.top", {"start": v(-125.7, -2.59) * mm, "end": v(-123.07, -2.59) * mm});
            skLineSegment(sketch, "E78.left", {"start": v(-125.7, -1.09) * mm, "end": v(-125.7, -2.59) * mm});
            skLineSegment(sketch, "E78.right", {"start": v(-110.7, -1.09) * mm, "end": v(-110.7, -2.59) * mm});
            skLineSegment(sketch, "E79.trimOffspring", {"start": v(-123.07, -2.59) * mm, "end": v(-123.07, -10.34) * mm});
            skLineSegment(sketch, "E80.trimOffspring", {"start": v(-121.57, -2.59) * mm, "end": v(-121.57, -10.34) * mm});
            skLineSegment(sketch, "E81.trimOffspring", {"start": v(-121.57, -1.09) * mm, "end": v(-118.94, -1.09) * mm, "construction": true});
            skLineSegment(sketch, "E82.trimOffspring", {"start": v(-121.57, -2.59) * mm, "end": v(-118.94, -2.59) * mm, "construction": true});
            skLineSegment(sketch, "E83.trimOffspring", {"start": v(-121.57, -1.09) * mm, "end": v(-114.82, -1.09) * mm});
            skLineSegment(sketch, "E84.trimOffspring", {"start": v(-121.57, -2.59) * mm, "end": v(-114.82, -2.59) * mm});
            skLineSegment(sketch, "E85.trimOffspring", {"start": v(-114.82, -2.59) * mm, "end": v(-114.82, -10.34) * mm});
            skLineSegment(sketch, "E86.trimOffspring", {"start": v(-113.32, -1.09) * mm, "end": v(-109.7, -1.09) * mm, "construction": true});
            skLineSegment(sketch, "E87.trimOffspring", {"start": v(-113.32, -2.59) * mm, "end": v(-113.32, -10.34) * mm});
            skLineSegment(sketch, "E88.trimOffspring", {"start": v(-113.32, -1.09) * mm, "end": v(-110.7, -1.09) * mm});
            skLineSegment(sketch, "E89.trimOffspring", {"start": v(-113.32, -2.59) * mm, "end": v(-109.7, -2.59) * mm, "construction": true});
            skLineSegment(sketch, "E90.trimOffspring", {"start": v(-113.32, -2.59) * mm, "end": v(-110.7, -2.59) * mm});
            skLineSegment(sketch, "E91.bottom", {"start": v(-117.06, 5.6) * mm, "end": v(-111.06, 5.6) * mm, "construction": true});
            skLineSegment(sketch, "E91.top", {"start": v(-117.06, -0.4) * mm, "end": v(-111.06, -0.4) * mm, "construction": true});
            skLineSegment(sketch, "E91.left", {"start": v(-117.06, 5.6) * mm, "end": v(-117.06, -0.4) * mm, "construction": true});
            skLineSegment(sketch, "E91.right", {"start": v(-111.06, 5.6) * mm, "end": v(-111.06, -0.4) * mm, "construction": true});
            skSolve(sketch);
        }
        {
            var Q0;
            Q0=makeQuery(id+"F18.imprint","IMPRINT",FACE,{"disambiguationData":[TD([[makeQuery(id+"F18.imprint","IMPRINT",EDGE,{"derivedFrom":sQuery(id+"F18.wireOp",EDGE,"E61.bottom")}),1.0]])]});
            var Q1;
            Q1=makeQuery(id+"F18.imprint","IMPRINT",FACE,{"disambiguationData":[TD([[makeQuery(id+"F18.imprint","IMPRINT",EDGE,{"derivedFrom":sQuery(id+"F18.wireOp",EDGE,"E61.top")}),-1.0]])]});
            var Q2;
            Q2=makeQuery(id+"F18.imprint","IMPRINT",FACE,{"disambiguationData":[TD([[makeQuery(id+"F18.imprint","IMPRINT",EDGE,{"derivedFrom":sQuery(id+"F18.wireOp",EDGE,"E61.left")}),1.0]])]});
            var Q3;
            Q3=makeQuery(id+"F18.imprint","IMPRINT",FACE,{"disambiguationData":[TD([[makeQuery(id+"F18.imprint","IMPRINT",EDGE,{"derivedFrom":sQuery(id+"F18.wireOp",EDGE,"0d877499-d8d4-4159-99c7-822d795fc6ca.bottom")}),-1.0]])]});
            var Q4;
            Q4=makeQuery(id+"F18.imprint","IMPRINT",FACE,{"disambiguationData":[TD([[makeQuery(id+"F18.imprint","IMPRINT",EDGE,{"derivedFrom":sQuery(id+"F18.wireOp",EDGE,"c0df8190-0039-47ec-86a2-d0705ce6734e.bottom")}),-1.0]])]});
            var Q5;
            Q5=makeQuery(id+"F18.imprint","IMPRINT",FACE,{"disambiguationData":[TD([[makeQuery(id+"F18.imprint","IMPRINT",EDGE,{"derivedFrom":sQuery(id+"F18.wireOp",EDGE,"hlkj7elJ-mpTF-eRwW-Toyz-55aFHtf3xgrz.bottom")}),-1.0]])]});
            var Q6;
            Q6=makeQuery(id+"F18.imprint","IMPRINT",FACE,{"disambiguationData":[TD([[makeQuery(id+"F18.imprint","IMPRINT",EDGE,{"derivedFrom":sQuery(id+"F18.wireOp",EDGE,"E76.bottom")}),-1.0]])]});
            var Q7;
            Q7=makeQuery(id+"F18.imprint","IMPRINT",FACE,{"disambiguationData":[TD([[makeQuery(id+"F18.imprint","IMPRINT",EDGE,{"derivedFrom":sQuery(id+"F18.wireOp",EDGE,"E77.bottom")}),-1.0]])]});
            extrude(context, id + "F19", {"entities" : qUnion([Q0, Q1, Q2, Q3, Q4, Q5, Q6, Q7]), "depth" : 1 * mm});
        }
        {
            var Q0;
            Q0=makeQuery(id+"F19.opExtrude","CAP_FACE",FACE,{"disambiguationData":[OSD([sQuery(id+"F18.wireOp",EDGE,"E61.left"),sQuery(id+"F18.wireOp",EDGE,"E61.right"),sQuery(id+"F18.wireOp",EDGE,"E62.top"),sQuery(id+"F18.wireOp",EDGE,"E62.left"),sQuery(id+"F18.wireOp",EDGE,"E62.right"),sQuery(id+"F18.wireOp",EDGE,"E63.top"),sQuery(id+"F18.wireOp",EDGE,"E63.left"),sQuery(id+"F18.wireOp",EDGE,"E63.right"),sQuery(id+"F18.wireOp",EDGE,"E66.0"),sQuery(id+"F18.wireOp",EDGE,"E66.1"),sQuery(id+"F18.wireOp",EDGE,"E66.2"),sQuery(id+"F18.wireOp",EDGE,"E66.3"),sQuery(id+"F18.wireOp",EDGE,"0d877499-d8d4-4159-99c7-822d795fc6ca.bottom"),sQuery(id+"F18.wireOp",EDGE,"0d877499-d8d4-4159-99c7-822d795fc6ca.top"),sQuery(id+"F18.wireOp",EDGE,"c0df8190-0039-47ec-86a2-d0705ce6734e.bottom"),sQuery(id+"F18.wireOp",EDGE,"c0df8190-0039-47ec-86a2-d0705ce6734e.top"),sQuery(id+"F18.wireOp",EDGE,"E67"),sQuery(id+"F18.wireOp",EDGE,"E69"),sQuery(id+"F18.wireOp",EDGE,"hlkj7elJ-mpTF-eRwW-Toyz-55aFHtf3xgrz.left"),sQuery(id+"F18.wireOp",EDGE,"hlkj7elJ-mpTF-eRwW-Toyz-55aFHtf3xgrz.right")])],"isStart":false});
            var sketch = newSketch(context, id + "F20", { "sketchPlane" : qUnion([Q0])});
            skLineSegment(sketch, "E92.bottom", {"start": v(-118.94, -0.34) * mm, "end": v(-117.44, -0.34) * mm});
            skLineSegment(sketch, "E92.top", {"start": v(-118.94, -3.34) * mm, "end": v(-117.44, -3.34) * mm});
            skLineSegment(sketch, "E92.left", {"start": v(-118.94, -0.34) * mm, "end": v(-118.94, -3.34) * mm});
            skLineSegment(sketch, "E92.right", {"start": v(-117.44, -0.34) * mm, "end": v(-117.44, -3.34) * mm});
            skSolve(sketch);
        }
        {
            var Q0;
            {var subQ0=sQuery(id+"F20.wireOp",EDGE,"E92.left");var subQ1=makeQuery(id+"F19.opExtrude","CAP_EDGE",EDGE,{"disambiguationData":[OSD([sQuery(id+"F18.wireOp",EDGE,"E83.trimOffspring")])],"isStart":false});var subQ2=makeQuery(id+"F20.imprint","INTERSECT",VERTEX,{"derivedFrom":[subQ1,subQ0]});Q0=makeQuery(id+"F20.imprint","IMPRINT",FACE,{"disambiguationData":[TD([[makeQuery(id+"F20.imprint","IMPRINT",EDGE,{"disambiguationData":[TD([[subQ2,-1.0]])],"derivedFrom":subQ0}),1.0]])]});}
            extrude(context, id + "F21", {"entities" : qUnion([Q0]), "operationType" : NewBodyOperationType.ADD, "depth" : 3 * mm});
        }
        {
            var Q0;
            Q0=makeQuery(id+"F21.opExtrude","CAP_FACE",FACE,{"disambiguationData":[OSD([sQuery(id+"F18.wireOp",EDGE,"E83.trimOffspring"),sQuery(id+"F18.wireOp",EDGE,"E84.trimOffspring"),sQuery(id+"F20.wireOp",EDGE,"E92.left"),sQuery(id+"F20.wireOp",EDGE,"E92.right")])],"isStart":false});
            var sketch = newSketch(context, id + "F22", { "sketchPlane" : qUnion([Q0])});
            skLineSegment(sketch, "E93.bottom", {"start": v(-114.7, -5.34) * mm, "end": v(-121.7, -5.34) * mm});
            skLineSegment(sketch, "E93.top", {"start": v(-114.7, 1.66) * mm, "end": v(-121.7, 1.66) * mm});
            skLineSegment(sketch, "E93.left", {"start": v(-114.7, -5.34) * mm, "end": v(-114.7, 1.66) * mm});
            skLineSegment(sketch, "E93.right", {"start": v(-121.7, -5.34) * mm, "end": v(-121.7, 1.66) * mm});
            skPoint(sketch, "E93.middle", {"position": v(-118.2, -1.84) * mm});
            skPoint(sketch, "E93.middle.positionSnap0", {"position": v(-118.2, -1.09) * mm});
            skPoint(sketch, "E93.middle.positionSnap1", {"position": v(-118.94, -1.84) * mm});
            skPoint(sketch, "E93.centerSnap0", {"position": v(-118.2, -1.09) * mm});
            skPoint(sketch, "E93.centerSnap1", {"position": v(-118.94, -1.84) * mm});
            skSolve(sketch);
        }
        {
            var Q0;
            Q0=makeQuery(id+"F22.imprint","IMPRINT",FACE,{"disambiguationData":[TD([[makeQuery(id+"F22.imprint","IMPRINT",EDGE,{"derivedFrom":sQuery(id+"F22.wireOp",EDGE,"E93.bottom")}),-1.0]])]});
            extrude(context, id + "F23", {"entities" : qUnion([Q0]), "depth" : 9 * mm});
        }
        {
            var Q0;
            Q0=qCreatedBy(makeId("Top.planeOp"),FACE);
            var sketch = newSketch(context, id + "F24", { "sketchPlane" : qUnion([Q0])});
            skLineSegment(sketch, "E94.bottom", {"start": v(-158.05, -0.5) * mm, "end": v(-159.05, -0.5) * mm});
            skLineSegment(sketch, "E94.top", {"start": v(-158.05, 0.5) * mm, "end": v(-159.05, 0.5) * mm});
            skLineSegment(sketch, "E94.left", {"start": v(-158.05, -0.5) * mm, "end": v(-158.05, 0.5) * mm});
            skLineSegment(sketch, "E94.right", {"start": v(-159.05, -0.5) * mm, "end": v(-159.05, 0.5) * mm});
            skPoint(sketch, "E94.middle", {"position": v(-158.55, 0) * mm});
            skSolve(sketch);
        }
        {
            var Q0;
            Q0=qSketchRegion(id+"F24",true);
            extrude(context, id + "F25", {"entities" : qUnion([Q0]), "depth" : 1 * mm});
        }
        {
            var Q0;
            Q0=makeQuery(id+"F19.opExtrude","CAP_FACE",FACE,{"disambiguationData":[OSD([sQuery(id+"F18.wireOp",EDGE,"E61.left"),sQuery(id+"F18.wireOp",EDGE,"E61.right"),sQuery(id+"F18.wireOp",EDGE,"E62.top"),sQuery(id+"F18.wireOp",EDGE,"E62.left"),sQuery(id+"F18.wireOp",EDGE,"E62.right"),sQuery(id+"F18.wireOp",EDGE,"E63.top"),sQuery(id+"F18.wireOp",EDGE,"E63.left"),sQuery(id+"F18.wireOp",EDGE,"E63.right"),sQuery(id+"F18.wireOp",EDGE,"E66.0"),sQuery(id+"F18.wireOp",EDGE,"E66.1"),sQuery(id+"F18.wireOp",EDGE,"E66.2"),sQuery(id+"F18.wireOp",EDGE,"E66.3"),sQuery(id+"F18.wireOp",EDGE,"E67"),sQuery(id+"F18.wireOp",EDGE,"E69"),sQuery(id+"F18.wireOp",EDGE,"E76.left"),sQuery(id+"F18.wireOp",EDGE,"E76.right"),sQuery(id+"F18.wireOp",EDGE,"E77.left"),sQuery(id+"F18.wireOp",EDGE,"E77.right"),sQuery(id+"F18.wireOp",EDGE,"E78.bottom"),sQuery(id+"F18.wireOp",EDGE,"E78.top"),sQuery(id+"F18.wireOp",EDGE,"E79.trimOffspring"),sQuery(id+"F18.wireOp",EDGE,"E80.trimOffspring"),sQuery(id+"F18.wireOp",EDGE,"E83.trimOffspring"),sQuery(id+"F18.wireOp",EDGE,"E84.trimOffspring"),sQuery(id+"F18.wireOp",EDGE,"E85.trimOffspring"),sQuery(id+"F18.wireOp",EDGE,"E87.trimOffspring"),sQuery(id+"F18.wireOp",EDGE,"E88.trimOffspring"),sQuery(id+"F18.wireOp",EDGE,"E90.trimOffspring")])],"isStart":false});
            var sketch = newSketch(context, id + "F26", { "sketchPlane" : qUnion([Q0])});
            skPoint(sketch, "E95.firstSnap0", {"position": v(-116.13, -1.09) * mm});
            skLineSegment(sketch, "E95.bottom", {"start": v(-126.7, -1.09) * mm, "end": v(-123.07, -1.09) * mm});
            skLineSegment(sketch, "E95.top", {"start": v(-126.7, -2.59) * mm, "end": v(-123.07, -2.59) * mm});
            skLineSegment(sketch, "E95.left", {"start": v(-126.7, -1.09) * mm, "end": v(-126.7, -2.59) * mm});
            skLineSegment(sketch, "E95.right", {"start": v(-123.07, -1.09) * mm, "end": v(-123.07, -2.59) * mm});
            skLineSegment(sketch, "E96.bottom", {"start": v(-113.32, -1.09) * mm, "end": v(-109.7, -1.09) * mm});
            skLineSegment(sketch, "E96.top", {"start": v(-113.32, -2.59) * mm, "end": v(-109.7, -2.59) * mm});
            skLineSegment(sketch, "E96.left", {"start": v(-113.32, -1.09) * mm, "end": v(-113.32, -2.59) * mm});
            skLineSegment(sketch, "E96.right", {"start": v(-109.7, -1.09) * mm, "end": v(-109.7, -2.59) * mm});
            skSolve(sketch);
        }
        {
            var Q0;
            {var subQ4=sQuery(id+"F26.wireOp",EDGE,"E96.left");Q0=makeQuery(id+"F26.imprint","IMPRINT",FACE,{"disambiguationData":[TD([[makeQuery(id+"F26.imprint","IMPRINT",EDGE,{"derivedFrom":subQ4}),1.0]])]});}
            var Q1;
            {var subQ4=sQuery(id+"F26.wireOp",EDGE,"E95.left");Q1=makeQuery(id+"F26.imprint","IMPRINT",FACE,{"disambiguationData":[TD([[makeQuery(id+"F26.imprint","IMPRINT",EDGE,{"derivedFrom":subQ4}),-1.0]])]});}
            extrude(context, id + "F27", {"entities" : qUnion([Q0, Q1]), "operationType" : NewBodyOperationType.ADD, "depth" : 10 * mm});
        }
        {
            var Q0;
            Q0=qCreatedBy(makeId("Top.planeOp"),FACE);
            var sketch = newSketch(context, id + "F28", { "sketchPlane" : qUnion([Q0])});
            skLineSegment(sketch, "E97.bottom", {"start": v(-65.37, 6.18) * mm, "end": v(-48.87, 6.18) * mm});
            skLineSegment(sketch, "E97.top", {"start": v(-65.37, -10.32) * mm, "end": v(-48.87, -10.32) * mm});
            skLineSegment(sketch, "E97.left", {"start": v(-65.37, 6.18) * mm, "end": v(-65.37, -10.32) * mm});
            skLineSegment(sketch, "E97.right", {"start": v(-48.87, 6.18) * mm, "end": v(-48.87, -10.32) * mm});
            skLineSegment(sketch, "E98.left", {"start": v(-61.97, 5.28) * mm, "end": v(-61.97, -9.42) * mm});
            skLineSegment(sketch, "E98.right", {"start": v(-59.47, 5.28) * mm, "end": v(-59.47, -9.42) * mm});
            skLineSegment(sketch, "E99.left", {"start": v(-54.77, 5.28) * mm, "end": v(-54.77, -9.42) * mm});
            skLineSegment(sketch, "E99.right", {"start": v(-52.27, 5.28) * mm, "end": v(-52.27, -9.42) * mm});
            skLineSegment(sketch, "E100.bottom", {"start": v(-63.47, 4.48) * mm, "end": v(-57.47, 4.48) * mm});
            skLineSegment(sketch, "E100.top", {"start": v(-63.47, -1.52) * mm, "end": v(-57.47, -1.52) * mm});
            skLineSegment(sketch, "E100.left", {"start": v(-63.47, 4.48) * mm, "end": v(-63.47, -1.52) * mm});
            skLineSegment(sketch, "E100.right", {"start": v(-57.47, 4.48) * mm, "end": v(-57.47, -1.52) * mm});
            skLineSegment(sketch, "E101.bottom", {"start": v(-56.77, 4.48) * mm, "end": v(-50.77, 4.48) * mm});
            skLineSegment(sketch, "E101.top", {"start": v(-56.77, -1.52) * mm, "end": v(-50.77, -1.52) * mm});
            skLineSegment(sketch, "E101.left", {"start": v(-56.77, 4.48) * mm, "end": v(-56.77, -1.52) * mm});
            skLineSegment(sketch, "E101.right", {"start": v(-50.77, 4.48) * mm, "end": v(-50.77, -1.52) * mm});
            skLineSegment(sketch, "E102.bottom", {"start": v(-63.47, -2.62) * mm, "end": v(-57.47, -2.62) * mm});
            skLineSegment(sketch, "E102.top", {"start": v(-63.47, -8.62) * mm, "end": v(-57.47, -8.62) * mm});
            skLineSegment(sketch, "E102.left", {"start": v(-63.47, -2.62) * mm, "end": v(-63.47, -8.62) * mm});
            skLineSegment(sketch, "E102.right", {"start": v(-57.47, -2.62) * mm, "end": v(-57.47, -8.62) * mm});
            skLineSegment(sketch, "E103.bottom", {"start": v(-56.77, -2.62) * mm, "end": v(-50.77, -2.62) * mm});
            skLineSegment(sketch, "E103.top", {"start": v(-56.77, -8.62) * mm, "end": v(-50.77, -8.62) * mm});
            skLineSegment(sketch, "E103.left", {"start": v(-56.77, -2.62) * mm, "end": v(-56.77, -8.62) * mm});
            skLineSegment(sketch, "E103.right", {"start": v(-50.77, -2.62) * mm, "end": v(-50.77, -8.62) * mm});
            skLineSegment(sketch, "E104.top", {"start": v(-65.37, 5.28) * mm, "end": v(-48.87, 5.28) * mm});
            skLineSegment(sketch, "E104.left", {"start": v(-65.37, 6.18) * mm, "end": v(-65.37, 5.28) * mm});
            skLineSegment(sketch, "E104.right", {"start": v(-48.87, 6.18) * mm, "end": v(-48.87, 5.28) * mm});
            skLineSegment(sketch, "E105.bottom", {"start": v(-65.37, -10.32) * mm, "end": v(-54.77, -10.32) * mm});
            skLineSegment(sketch, "E105.top", {"start": v(-65.37, -9.42) * mm, "end": v(-48.87, -9.42) * mm});
            skLineSegment(sketch, "E105.left", {"start": v(-65.37, -10.32) * mm, "end": v(-65.37, -9.42) * mm});
            skLineSegment(sketch, "E105.right", {"start": v(-48.87, -10.32) * mm, "end": v(-48.87, -9.42) * mm});
            skLineSegment(sketch, "E106.bottom", {"start": v(-65.37, -9.42) * mm, "end": v(-64.47, -9.42) * mm});
            skLineSegment(sketch, "E106.top", {"start": v(-65.37, 5.28) * mm, "end": v(-64.47, 5.28) * mm});
            skLineSegment(sketch, "E106.left", {"start": v(-65.37, -9.42) * mm, "end": v(-65.37, 5.28) * mm});
            skLineSegment(sketch, "E106.right", {"start": v(-64.47, -9.42) * mm, "end": v(-64.47, 5.28) * mm});
            skLineSegment(sketch, "E107.bottom", {"start": v(-48.87, 5.28) * mm, "end": v(-49.77, 5.28) * mm});
            skLineSegment(sketch, "E107.top", {"start": v(-48.87, -9.42) * mm, "end": v(-49.77, -9.42) * mm});
            skLineSegment(sketch, "E107.left", {"start": v(-48.87, 5.28) * mm, "end": v(-48.87, -9.42) * mm});
            skLineSegment(sketch, "E107.right", {"start": v(-49.77, 5.28) * mm, "end": v(-49.77, -9.42) * mm});
            skLineSegment(sketch, "E108.trimOffspring", {"start": v(-52.27, -10.32) * mm, "end": v(-48.87, -10.32) * mm});
            skSolve(sketch);
        }
        {
            var Q0;
            Q0=makeQuery(id+"F28.imprint","IMPRINT",FACE,{"disambiguationData":[TD([[makeQuery(id+"F28.imprint","IMPRINT",EDGE,{"derivedFrom":sQuery(id+"F28.wireOp",EDGE,"E97.top")}),1.0]])]});
            var Q1;
            Q1=makeQuery(id+"F28.imprint","IMPRINT",FACE,{"disambiguationData":[TD([[makeQuery(id+"F28.imprint","IMPRINT",EDGE,{"derivedFrom":sQuery(id+"F28.wireOp",EDGE,"E106.bottom")}),1.0]])]});
            var Q2;
            Q2=makeQuery(id+"F28.imprint","IMPRINT",FACE,{"disambiguationData":[TD([[makeQuery(id+"F28.imprint","IMPRINT",EDGE,{"derivedFrom":sQuery(id+"F28.wireOp",EDGE,"E97.bottom")}),-1.0]])]});
            var Q3;
            Q3=makeQuery(id+"F28.imprint","IMPRINT",FACE,{"disambiguationData":[TD([[makeQuery(id+"F28.imprint","IMPRINT",EDGE,{"derivedFrom":sQuery(id+"F28.wireOp",EDGE,"E107.bottom")}),1.0]])]});
            var Q4;
            {var subQ0=sQuery(id+"F28.wireOp",EDGE,"E99.left");Q4=makeQuery(id+"F28.imprint","IMPRINT",FACE,{"disambiguationData":[TD([[makeQuery(id+"F28.imprint","IMPRINT",EDGE,{"derivedFrom":subQ0}),1.0]])]});}
            var Q5;
            {var subQ0=sQuery(id+"F28.wireOp",EDGE,"E98.left");Q5=makeQuery(id+"F28.imprint","IMPRINT",FACE,{"disambiguationData":[TD([[makeQuery(id+"F28.imprint","IMPRINT",EDGE,{"derivedFrom":subQ0}),1.0]])]});}
            extrude(context, id + "F29", {"entities" : qUnion([Q0, Q1, Q2, Q3, Q4, Q5]), "depth" : 1 * mm});
        }
        {
            var Q0;
            Q0=qCreatedBy(makeId("Top.planeOp"),FACE);
            var sketch = newSketch(context, id + "F30", { "sketchPlane" : qUnion([Q0])});
            skLineSegment(sketch, "E109.bottom", {"start": v(-124.98, -143.56) * mm, "end": v(-106.98, -143.56) * mm});
            skLineSegment(sketch, "E109.top", {"start": v(-124.98, -161.56) * mm, "end": v(-106.98, -161.56) * mm});
            skLineSegment(sketch, "E109.left", {"start": v(-124.98, -143.56) * mm, "end": v(-124.98, -161.56) * mm});
            skLineSegment(sketch, "E109.right", {"start": v(-106.98, -143.56) * mm, "end": v(-106.98, -161.56) * mm});
            skLineSegment(sketch, "E110.bottom", {"start": v(-116.73, -143.56) * mm, "end": v(-115.23, -143.56) * mm, "construction": true});
            skLineSegment(sketch, "E110.top", {"start": v(-116.73, -161.56) * mm, "end": v(-115.23, -161.56) * mm, "construction": true});
            skLineSegment(sketch, "E110.left", {"start": v(-116.73, -143.56) * mm, "end": v(-116.73, -151.56) * mm, "construction": true});
            skLineSegment(sketch, "E110.right", {"start": v(-115.23, -143.56) * mm, "end": v(-115.23, -151.56) * mm, "construction": true});
            skCircle(sketch, "E111", {"center": v(-115.98, -137.56) * mm, "radius": 1.5 * mm});
            skPoint(sketch, "E112", {"position": v(-115.98, -143.56) * mm});
            skCircle(sketch, "E113", {"center": v(-115.98, -167.56) * mm, "radius": 1.5 * mm});
            skLineSegment(sketch, "E114.trimOffspring", {"start": v(-115.23, -151.56) * mm, "end": v(-112.23, -151.56) * mm, "construction": true});
            skLineSegment(sketch, "E115.trimOffspring", {"start": v(-115.23, -153.56) * mm, "end": v(-112.23, -153.56) * mm, "construction": true});
            skLineSegment(sketch, "E116.trimOffspring", {"start": v(-116.73, -153.56) * mm, "end": v(-116.73, -161.56) * mm, "construction": true});
            skLineSegment(sketch, "E117.trimOffspring", {"start": v(-115.23, -153.56) * mm, "end": v(-115.23, -161.56) * mm, "construction": true});
            skLineSegment(sketch, "E118.bottom", {"start": v(-121.73, -143.56) * mm, "end": v(-119.73, -143.56) * mm});
            skLineSegment(sketch, "E118.top", {"start": v(-121.73, -161.56) * mm, "end": v(-119.73, -161.56) * mm});
            skLineSegment(sketch, "E118.left", {"start": v(-121.73, -143.56) * mm, "end": v(-121.73, -151.56) * mm});
            skLineSegment(sketch, "E118.right", {"start": v(-119.73, -143.56) * mm, "end": v(-119.73, -151.56) * mm});
            skLineSegment(sketch, "E119.bottom", {"start": v(-112.23, -143.56) * mm, "end": v(-110.23, -143.56) * mm});
            skLineSegment(sketch, "E119.top", {"start": v(-112.23, -161.56) * mm, "end": v(-110.23, -161.56) * mm});
            skLineSegment(sketch, "E119.left", {"start": v(-112.23, -143.56) * mm, "end": v(-112.23, -151.56) * mm});
            skLineSegment(sketch, "E119.right", {"start": v(-110.23, -143.56) * mm, "end": v(-110.23, -151.56) * mm});
            skLineSegment(sketch, "E120.bottom", {"start": v(-124.98, -151.56) * mm, "end": v(-121.73, -151.56) * mm});
            skLineSegment(sketch, "E120.top", {"start": v(-124.98, -153.56) * mm, "end": v(-121.73, -153.56) * mm});
            skLineSegment(sketch, "E120.left", {"start": v(-124.98, -151.56) * mm, "end": v(-124.98, -153.56) * mm});
            skLineSegment(sketch, "E120.right", {"start": v(-106.98, -151.56) * mm, "end": v(-106.98, -153.56) * mm});
            skLineSegment(sketch, "E121.trimOffspring", {"start": v(-121.73, -153.56) * mm, "end": v(-121.73, -161.56) * mm});
            skLineSegment(sketch, "E122.trimOffspring", {"start": v(-119.73, -153.56) * mm, "end": v(-119.73, -161.56) * mm});
            skLineSegment(sketch, "E123.trimOffspring", {"start": v(-119.73, -151.56) * mm, "end": v(-116.73, -151.56) * mm, "construction": true});
            skLineSegment(sketch, "E124.trimOffspring", {"start": v(-119.73, -153.56) * mm, "end": v(-116.73, -153.56) * mm, "construction": true});
            skLineSegment(sketch, "E125.trimOffspring", {"start": v(-119.73, -151.56) * mm, "end": v(-112.23, -151.56) * mm});
            skLineSegment(sketch, "E126.trimOffspring", {"start": v(-119.73, -153.56) * mm, "end": v(-112.23, -153.56) * mm});
            skLineSegment(sketch, "E127.trimOffspring", {"start": v(-112.23, -153.56) * mm, "end": v(-112.23, -161.56) * mm});
            skLineSegment(sketch, "E128.trimOffspring", {"start": v(-110.23, -153.56) * mm, "end": v(-110.23, -161.56) * mm});
            skLineSegment(sketch, "E129.trimOffspring", {"start": v(-110.23, -151.56) * mm, "end": v(-106.98, -151.56) * mm});
            skLineSegment(sketch, "E130.trimOffspring", {"start": v(-110.23, -153.56) * mm, "end": v(-106.98, -153.56) * mm});
            skLineSegment(sketch, "E131.bottom", {"start": v(-94.98, -143.56) * mm, "end": v(-76.98, -143.56) * mm});
            skLineSegment(sketch, "E131.top", {"start": v(-94.98, -161.56) * mm, "end": v(-76.98, -161.56) * mm});
            skLineSegment(sketch, "E131.left", {"start": v(-94.98, -143.56) * mm, "end": v(-94.98, -161.56) * mm});
            skLineSegment(sketch, "E131.right", {"start": v(-76.98, -143.56) * mm, "end": v(-76.98, -161.56) * mm});
            skLineSegment(sketch, "E132.bottom", {"start": v(-86.73, -143.56) * mm, "end": v(-85.23, -143.56) * mm, "construction": true});
            skLineSegment(sketch, "E132.top", {"start": v(-86.73, -161.56) * mm, "end": v(-85.23, -161.56) * mm, "construction": true});
            skLineSegment(sketch, "E132.left", {"start": v(-86.73, -143.56) * mm, "end": v(-86.73, -151.56) * mm, "construction": true});
            skLineSegment(sketch, "E132.right", {"start": v(-85.23, -143.56) * mm, "end": v(-85.23, -151.56) * mm, "construction": true});
            skLineSegment(sketch, "E133.bottom", {"start": v(-94.98, -151.56) * mm, "end": v(-91.73, -151.56) * mm, "construction": true});
            skLineSegment(sketch, "E133.top", {"start": v(-94.98, -153.56) * mm, "end": v(-91.73, -153.56) * mm, "construction": true});
            skLineSegment(sketch, "E133.left", {"start": v(-94.98, -151.56) * mm, "end": v(-94.98, -153.56) * mm, "construction": true});
            skLineSegment(sketch, "E133.right", {"start": v(-76.98, -151.56) * mm, "end": v(-76.98, -153.56) * mm, "construction": true});
            skCircle(sketch, "E134", {"center": v(-85.98, -137.56) * mm, "radius": 1.5 * mm});
            skPoint(sketch, "E135", {"position": v(-85.98, -143.56) * mm});
            skCircle(sketch, "E136", {"center": v(-85.98, -167.56) * mm, "radius": 1.5 * mm});
            skLineSegment(sketch, "E137.trimOffspring", {"start": v(-85.23, -151.56) * mm, "end": v(-82.23, -151.56) * mm, "construction": true});
            skLineSegment(sketch, "E138.trimOffspring", {"start": v(-85.23, -153.56) * mm, "end": v(-82.23, -153.56) * mm, "construction": true});
            skLineSegment(sketch, "E139.trimOffspring", {"start": v(-86.73, -153.56) * mm, "end": v(-86.73, -161.56) * mm, "construction": true});
            skLineSegment(sketch, "E140.trimOffspring", {"start": v(-85.23, -153.56) * mm, "end": v(-85.23, -161.56) * mm, "construction": true});
            skLineSegment(sketch, "E141.bottom", {"start": v(-91.73, -143.56) * mm, "end": v(-89.73, -143.56) * mm});
            skLineSegment(sketch, "E141.top", {"start": v(-91.73, -161.56) * mm, "end": v(-89.73, -161.56) * mm});
            skLineSegment(sketch, "E141.left", {"start": v(-91.73, -143.56) * mm, "end": v(-91.73, -151.56) * mm});
            skLineSegment(sketch, "E141.right", {"start": v(-89.73, -143.56) * mm, "end": v(-89.73, -151.56) * mm});
            skLineSegment(sketch, "E142.bottom", {"start": v(-82.23, -143.56) * mm, "end": v(-80.23, -143.56) * mm});
            skLineSegment(sketch, "E142.top", {"start": v(-82.23, -161.56) * mm, "end": v(-80.23, -161.56) * mm});
            skLineSegment(sketch, "E142.left", {"start": v(-82.23, -143.56) * mm, "end": v(-82.23, -151.56) * mm});
            skLineSegment(sketch, "E142.right", {"start": v(-80.23, -143.56) * mm, "end": v(-80.23, -151.56) * mm});
            skLineSegment(sketch, "E143.bottom", {"start": v(-94.98, -151.56) * mm, "end": v(-91.73, -151.56) * mm});
            skLineSegment(sketch, "E143.top", {"start": v(-94.98, -153.56) * mm, "end": v(-91.73, -153.56) * mm});
            skLineSegment(sketch, "E143.left", {"start": v(-94.98, -151.56) * mm, "end": v(-94.98, -153.56) * mm});
            skLineSegment(sketch, "E143.right", {"start": v(-76.98, -151.56) * mm, "end": v(-76.98, -153.56) * mm});
            skLineSegment(sketch, "E144.trimOffspring", {"start": v(-91.73, -153.56) * mm, "end": v(-91.73, -161.56) * mm});
            skLineSegment(sketch, "E145.trimOffspring", {"start": v(-89.73, -153.56) * mm, "end": v(-89.73, -161.56) * mm});
            skLineSegment(sketch, "E146.trimOffspring", {"start": v(-89.73, -151.56) * mm, "end": v(-86.73, -151.56) * mm, "construction": true});
            skLineSegment(sketch, "E147.trimOffspring", {"start": v(-89.73, -153.56) * mm, "end": v(-86.73, -153.56) * mm, "construction": true});
            skLineSegment(sketch, "E148.trimOffspring", {"start": v(-89.73, -151.56) * mm, "end": v(-82.23, -151.56) * mm});
            skLineSegment(sketch, "E149.trimOffspring", {"start": v(-89.73, -153.56) * mm, "end": v(-82.23, -153.56) * mm});
            skLineSegment(sketch, "E150.trimOffspring", {"start": v(-82.23, -153.56) * mm, "end": v(-82.23, -161.56) * mm});
            skLineSegment(sketch, "E151.trimOffspring", {"start": v(-80.23, -151.56) * mm, "end": v(-76.98, -151.56) * mm, "construction": true});
            skLineSegment(sketch, "E152.trimOffspring", {"start": v(-80.23, -153.56) * mm, "end": v(-80.23, -161.56) * mm});
            skLineSegment(sketch, "E153.trimOffspring", {"start": v(-80.23, -151.56) * mm, "end": v(-76.98, -151.56) * mm});
            skLineSegment(sketch, "E154.trimOffspring", {"start": v(-80.23, -153.56) * mm, "end": v(-76.98, -153.56) * mm, "construction": true});
            skLineSegment(sketch, "E155.trimOffspring", {"start": v(-80.23, -153.56) * mm, "end": v(-76.98, -153.56) * mm});
            skLineSegment(sketch, "E156.bottom", {"start": v(-64.98, -143.56) * mm, "end": v(-46.98, -143.56) * mm});
            skLineSegment(sketch, "E156.top", {"start": v(-64.98, -161.56) * mm, "end": v(-46.98, -161.56) * mm});
            skLineSegment(sketch, "E156.left", {"start": v(-64.98, -143.56) * mm, "end": v(-64.98, -161.56) * mm});
            skLineSegment(sketch, "E156.right", {"start": v(-46.98, -143.56) * mm, "end": v(-46.98, -161.56) * mm});
            skLineSegment(sketch, "E157.bottom", {"start": v(-64.98, -161.56) * mm, "end": v(-47.98, -161.56) * mm});
            skLineSegment(sketch, "E158.bottom", {"start": v(-56.73, -143.56) * mm, "end": v(-55.23, -143.56) * mm, "construction": true});
            skLineSegment(sketch, "E158.top", {"start": v(-56.73, -161.56) * mm, "end": v(-55.23, -161.56) * mm, "construction": true});
            skLineSegment(sketch, "E158.left", {"start": v(-56.73, -143.56) * mm, "end": v(-56.73, -151.56) * mm, "construction": true});
            skLineSegment(sketch, "E158.right", {"start": v(-55.23, -143.56) * mm, "end": v(-55.23, -151.56) * mm, "construction": true});
            skLineSegment(sketch, "E159.bottom", {"start": v(-64.98, -151.56) * mm, "end": v(-61.73, -151.56) * mm, "construction": true});
            skLineSegment(sketch, "E159.top", {"start": v(-64.98, -153.56) * mm, "end": v(-61.73, -153.56) * mm, "construction": true});
            skLineSegment(sketch, "E159.left", {"start": v(-64.98, -151.56) * mm, "end": v(-64.98, -153.56) * mm, "construction": true});
            skLineSegment(sketch, "E159.right", {"start": v(-46.98, -151.56) * mm, "end": v(-46.98, -153.56) * mm, "construction": true});
            skCircle(sketch, "E160", {"center": v(-55.98, -137.56) * mm, "radius": 1.5 * mm});
            skPoint(sketch, "E161", {"position": v(-55.98, -143.56) * mm});
            skCircle(sketch, "E162", {"center": v(-55.98, -167.56) * mm, "radius": 1.5 * mm});
            skLineSegment(sketch, "E163.trimOffspring", {"start": v(-55.23, -151.56) * mm, "end": v(-52.23, -151.56) * mm, "construction": true});
            skLineSegment(sketch, "E164.trimOffspring", {"start": v(-55.23, -153.56) * mm, "end": v(-52.23, -153.56) * mm, "construction": true});
            skLineSegment(sketch, "E165.trimOffspring", {"start": v(-56.73, -153.56) * mm, "end": v(-56.73, -161.56) * mm, "construction": true});
            skLineSegment(sketch, "E166.trimOffspring", {"start": v(-55.23, -153.56) * mm, "end": v(-55.23, -161.56) * mm, "construction": true});
            skLineSegment(sketch, "E167.bottom", {"start": v(-61.73, -143.56) * mm, "end": v(-59.73, -143.56) * mm});
            skLineSegment(sketch, "E167.top", {"start": v(-61.73, -161.56) * mm, "end": v(-59.73, -161.56) * mm});
            skLineSegment(sketch, "E167.left", {"start": v(-61.73, -143.56) * mm, "end": v(-61.73, -151.56) * mm});
            skLineSegment(sketch, "E167.right", {"start": v(-59.73, -143.56) * mm, "end": v(-59.73, -151.56) * mm});
            skLineSegment(sketch, "E168.bottom", {"start": v(-52.23, -143.56) * mm, "end": v(-50.23, -143.56) * mm});
            skLineSegment(sketch, "E168.top", {"start": v(-52.23, -161.56) * mm, "end": v(-50.23, -161.56) * mm});
            skLineSegment(sketch, "E168.left", {"start": v(-52.23, -143.56) * mm, "end": v(-52.23, -151.56) * mm});
            skLineSegment(sketch, "E168.right", {"start": v(-50.23, -143.56) * mm, "end": v(-50.23, -151.56) * mm});
            skLineSegment(sketch, "E169.bottom", {"start": v(-64.98, -151.56) * mm, "end": v(-61.73, -151.56) * mm});
            skLineSegment(sketch, "E169.top", {"start": v(-64.98, -153.56) * mm, "end": v(-61.73, -153.56) * mm});
            skLineSegment(sketch, "E169.left", {"start": v(-64.98, -151.56) * mm, "end": v(-64.98, -153.56) * mm});
            skLineSegment(sketch, "E169.right", {"start": v(-46.98, -151.56) * mm, "end": v(-46.98, -153.56) * mm});
            skLineSegment(sketch, "E170.trimOffspring", {"start": v(-61.73, -153.56) * mm, "end": v(-61.73, -161.56) * mm});
            skLineSegment(sketch, "E171.trimOffspring", {"start": v(-59.73, -153.56) * mm, "end": v(-59.73, -161.56) * mm});
            skLineSegment(sketch, "E172.trimOffspring", {"start": v(-59.73, -151.56) * mm, "end": v(-56.73, -151.56) * mm, "construction": true});
            skLineSegment(sketch, "E173.trimOffspring", {"start": v(-59.73, -153.56) * mm, "end": v(-56.73, -153.56) * mm, "construction": true});
            skLineSegment(sketch, "E174.trimOffspring", {"start": v(-59.73, -151.56) * mm, "end": v(-52.23, -151.56) * mm});
            skLineSegment(sketch, "E175.trimOffspring", {"start": v(-59.73, -153.56) * mm, "end": v(-52.23, -153.56) * mm});
            skLineSegment(sketch, "E176.trimOffspring", {"start": v(-52.23, -153.56) * mm, "end": v(-52.23, -161.56) * mm});
            skLineSegment(sketch, "E177.trimOffspring", {"start": v(-50.23, -151.56) * mm, "end": v(-46.98, -151.56) * mm, "construction": true});
            skLineSegment(sketch, "E178.trimOffspring", {"start": v(-50.23, -153.56) * mm, "end": v(-50.23, -161.56) * mm});
            skLineSegment(sketch, "E179.trimOffspring", {"start": v(-50.23, -151.56) * mm, "end": v(-46.98, -151.56) * mm});
            skLineSegment(sketch, "E180.trimOffspring", {"start": v(-50.23, -153.56) * mm, "end": v(-46.98, -153.56) * mm, "construction": true});
            skLineSegment(sketch, "E181.trimOffspring", {"start": v(-50.23, -153.56) * mm, "end": v(-46.98, -153.56) * mm});
            skLineSegment(sketch, "E182.bottom", {"start": v(-34.98, -143.56) * mm, "end": v(-16.98, -143.56) * mm});
            skLineSegment(sketch, "E182.top", {"start": v(-34.98, -161.56) * mm, "end": v(-16.98, -161.56) * mm});
            skLineSegment(sketch, "E182.left", {"start": v(-34.98, -143.56) * mm, "end": v(-34.98, -161.56) * mm});
            skLineSegment(sketch, "E182.right", {"start": v(-16.98, -143.56) * mm, "end": v(-16.98, -161.56) * mm});
            skLineSegment(sketch, "E183.bottom", {"start": v(-34.98, -161.56) * mm, "end": v(-17.98, -161.56) * mm});
            skLineSegment(sketch, "E184.bottom", {"start": v(-26.73, -143.56) * mm, "end": v(-25.23, -143.56) * mm, "construction": true});
            skLineSegment(sketch, "E184.top", {"start": v(-26.73, -161.56) * mm, "end": v(-25.23, -161.56) * mm, "construction": true});
            skLineSegment(sketch, "E184.left", {"start": v(-26.73, -143.56) * mm, "end": v(-26.73, -151.56) * mm, "construction": true});
            skLineSegment(sketch, "E184.right", {"start": v(-25.23, -143.56) * mm, "end": v(-25.23, -151.56) * mm, "construction": true});
            skLineSegment(sketch, "E185.bottom", {"start": v(-34.98, -151.56) * mm, "end": v(-31.73, -151.56) * mm, "construction": true});
            skLineSegment(sketch, "E185.top", {"start": v(-34.98, -153.56) * mm, "end": v(-31.73, -153.56) * mm, "construction": true});
            skLineSegment(sketch, "E185.left", {"start": v(-34.98, -151.56) * mm, "end": v(-34.98, -153.56) * mm, "construction": true});
            skLineSegment(sketch, "E185.right", {"start": v(-16.98, -151.56) * mm, "end": v(-16.98, -153.56) * mm, "construction": true});
            skCircle(sketch, "E186", {"center": v(-25.98, -137.56) * mm, "radius": 1.5 * mm});
            skPoint(sketch, "E187", {"position": v(-25.98, -143.56) * mm});
            skCircle(sketch, "E188", {"center": v(-25.98, -167.56) * mm, "radius": 1.5 * mm});
            skLineSegment(sketch, "E189.trimOffspring", {"start": v(-25.23, -151.56) * mm, "end": v(-22.23, -151.56) * mm, "construction": true});
            skLineSegment(sketch, "E190.trimOffspring", {"start": v(-25.23, -153.56) * mm, "end": v(-22.23, -153.56) * mm, "construction": true});
            skLineSegment(sketch, "E191.trimOffspring", {"start": v(-26.73, -153.56) * mm, "end": v(-26.73, -161.56) * mm, "construction": true});
            skLineSegment(sketch, "E192.trimOffspring", {"start": v(-25.23, -153.56) * mm, "end": v(-25.23, -161.56) * mm, "construction": true});
            skLineSegment(sketch, "E193.bottom", {"start": v(-31.73, -143.56) * mm, "end": v(-29.73, -143.56) * mm});
            skLineSegment(sketch, "E193.top", {"start": v(-31.73, -161.56) * mm, "end": v(-29.73, -161.56) * mm});
            skLineSegment(sketch, "E193.left", {"start": v(-31.73, -143.56) * mm, "end": v(-31.73, -151.56) * mm});
            skLineSegment(sketch, "E193.right", {"start": v(-29.73, -143.56) * mm, "end": v(-29.73, -151.56) * mm});
            skLineSegment(sketch, "E194.bottom", {"start": v(-22.23, -143.56) * mm, "end": v(-20.23, -143.56) * mm});
            skLineSegment(sketch, "E194.top", {"start": v(-22.23, -161.56) * mm, "end": v(-20.23, -161.56) * mm});
            skLineSegment(sketch, "E194.left", {"start": v(-22.23, -143.56) * mm, "end": v(-22.23, -151.56) * mm});
            skLineSegment(sketch, "E194.right", {"start": v(-20.23, -143.56) * mm, "end": v(-20.23, -151.56) * mm});
            skLineSegment(sketch, "E195.bottom", {"start": v(-34.98, -151.56) * mm, "end": v(-31.73, -151.56) * mm});
            skLineSegment(sketch, "E195.top", {"start": v(-34.98, -153.56) * mm, "end": v(-31.73, -153.56) * mm});
            skLineSegment(sketch, "E195.left", {"start": v(-34.98, -151.56) * mm, "end": v(-34.98, -153.56) * mm});
            skLineSegment(sketch, "E195.right", {"start": v(-16.98, -151.56) * mm, "end": v(-16.98, -153.56) * mm});
            skLineSegment(sketch, "E196.trimOffspring", {"start": v(-31.73, -153.56) * mm, "end": v(-31.73, -161.56) * mm});
            skLineSegment(sketch, "E197.trimOffspring", {"start": v(-29.73, -153.56) * mm, "end": v(-29.73, -161.56) * mm});
            skLineSegment(sketch, "E198.trimOffspring", {"start": v(-29.73, -151.56) * mm, "end": v(-26.73, -151.56) * mm, "construction": true});
            skLineSegment(sketch, "E199.trimOffspring", {"start": v(-29.73, -153.56) * mm, "end": v(-26.73, -153.56) * mm, "construction": true});
            skLineSegment(sketch, "E200.trimOffspring", {"start": v(-29.73, -151.56) * mm, "end": v(-22.23, -151.56) * mm});
            skLineSegment(sketch, "E201.trimOffspring", {"start": v(-29.73, -153.56) * mm, "end": v(-22.23, -153.56) * mm});
            skLineSegment(sketch, "E202.trimOffspring", {"start": v(-22.23, -153.56) * mm, "end": v(-22.23, -161.56) * mm});
            skLineSegment(sketch, "E203.trimOffspring", {"start": v(-20.23, -151.56) * mm, "end": v(-16.98, -151.56) * mm, "construction": true});
            skLineSegment(sketch, "E204.trimOffspring", {"start": v(-20.23, -153.56) * mm, "end": v(-20.23, -161.56) * mm});
            skLineSegment(sketch, "E205.trimOffspring", {"start": v(-20.23, -151.56) * mm, "end": v(-16.98, -151.56) * mm});
            skLineSegment(sketch, "E206.trimOffspring", {"start": v(-20.23, -153.56) * mm, "end": v(-16.98, -153.56) * mm, "construction": true});
            skLineSegment(sketch, "E207.trimOffspring", {"start": v(-20.23, -153.56) * mm, "end": v(-16.98, -153.56) * mm});
            skLineSegment(sketch, "E208.bottom", {"start": v(-129.58, -134.06) * mm, "end": v(-12.58, -134.06) * mm});
            skLineSegment(sketch, "E208.top", {"start": v(-129.58, -171.06) * mm, "end": v(-12.58, -171.06) * mm});
            skLineSegment(sketch, "E208.left", {"start": v(-129.58, -134.06) * mm, "end": v(-129.58, -171.06) * mm});
            skLineSegment(sketch, "E208.right", {"start": v(-12.58, -134.06) * mm, "end": v(-12.58, -171.06) * mm});
            skSolve(sketch);
        }
        {
            var Q0;
            Q0=makeQuery(id+"F30.imprint","IMPRINT",FACE,{"disambiguationData":[TD([[makeQuery(id+"F30.imprint","IMPRINT",EDGE,{"derivedFrom":sQuery(id+"F30.wireOp",EDGE,"E111")}),-1.0]])]});
            var Q1;
            Q1=makeQuery(id+"F30.imprint","IMPRINT",FACE,{"disambiguationData":[TD([[makeQuery(id+"F30.imprint","IMPRINT",EDGE,{"derivedFrom":sQuery(id+"F30.wireOp",EDGE,"E118.bottom")}),-1.0]])]});
            var Q2;
            Q2=makeQuery(id+"F30.imprint","IMPRINT",FACE,{"disambiguationData":[TD([[makeQuery(id+"F30.imprint","IMPRINT",EDGE,{"derivedFrom":sQuery(id+"F30.wireOp",EDGE,"E141.bottom")}),-1.0]])]});
            var Q3;
            Q3=makeQuery(id+"F30.imprint","IMPRINT",FACE,{"disambiguationData":[TD([[makeQuery(id+"F30.imprint","IMPRINT",EDGE,{"derivedFrom":sQuery(id+"F30.wireOp",EDGE,"E167.bottom")}),-1.0]])]});
            var Q4;
            Q4=makeQuery(id+"F30.imprint","IMPRINT",FACE,{"disambiguationData":[TD([[makeQuery(id+"F30.imprint","IMPRINT",EDGE,{"derivedFrom":sQuery(id+"F30.wireOp",EDGE,"E193.bottom")}),-1.0]])]});
            extrude(context, id + "F31", {"entities" : qUnion([Q0, Q1, Q2, Q3, Q4]), "depth" : 1 * mm});
        }
        {
            var Q0;
            Q0=qCreatedBy(makeId("Top.planeOp"),FACE);
            var sketch = newSketch(context, id + "F32", { "sketchPlane" : qUnion([Q0])});
            skLineSegment(sketch, "E209.bottom", {"start": v(15.66, -134.86) * mm, "end": v(137.66, -134.86) * mm});
            skLineSegment(sketch, "E209.top", {"start": v(15.66, -174.06) * mm, "end": v(137.66, -174.06) * mm});
            skLineSegment(sketch, "E209.left", {"start": v(15.66, -134.86) * mm, "end": v(15.66, -174.06) * mm});
            skLineSegment(sketch, "E209.right", {"start": v(137.66, -134.86) * mm, "end": v(137.66, -174.06) * mm});
            skLineSegment(sketch, "E210.bottom", {"start": v(22.26, -144.36) * mm, "end": v(42.46, -144.36) * mm});
            skLineSegment(sketch, "E210.top", {"start": v(22.26, -164.56) * mm, "end": v(42.46, -164.56) * mm});
            skLineSegment(sketch, "E210.left", {"start": v(22.26, -144.36) * mm, "end": v(22.26, -164.56) * mm});
            skLineSegment(sketch, "E210.right", {"start": v(42.46, -144.36) * mm, "end": v(42.46, -164.56) * mm});
            skCircle(sketch, "E211", {"center": v(32.36, -139.46) * mm, "radius": 1.5 * mm, "construction": true});
            skCircle(sketch, "E212", {"center": v(32.36, -169.46) * mm, "radius": 1.5 * mm, "construction": true});
            skLineSegment(sketch, "E213.bottom", {"start": v(52.26, -144.36) * mm, "end": v(72.46, -144.36) * mm});
            skLineSegment(sketch, "E213.top", {"start": v(52.26, -164.56) * mm, "end": v(72.46, -164.56) * mm});
            skLineSegment(sketch, "E213.left", {"start": v(52.26, -144.36) * mm, "end": v(52.26, -164.56) * mm});
            skLineSegment(sketch, "E213.right", {"start": v(72.46, -144.36) * mm, "end": v(72.46, -164.56) * mm});
            skCircle(sketch, "E214", {"center": v(62.36, -139.46) * mm, "radius": 1.5 * mm, "construction": true});
            skCircle(sketch, "E215", {"center": v(62.36, -169.46) * mm, "radius": 1.5 * mm, "construction": true});
            skLineSegment(sketch, "E216.bottom", {"start": v(82.26, -144.36) * mm, "end": v(102.46, -144.36) * mm});
            skLineSegment(sketch, "E216.top", {"start": v(82.26, -164.56) * mm, "end": v(102.46, -164.56) * mm});
            skLineSegment(sketch, "E216.left", {"start": v(82.26, -144.36) * mm, "end": v(82.26, -164.56) * mm});
            skLineSegment(sketch, "E216.right", {"start": v(102.46, -144.36) * mm, "end": v(102.46, -164.56) * mm});
            skCircle(sketch, "E217", {"center": v(92.36, -139.46) * mm, "radius": 1.5 * mm, "construction": true});
            skCircle(sketch, "E218", {"center": v(92.36, -169.46) * mm, "radius": 1.5 * mm, "construction": true});
            skPoint(sketch, "E218.centerSnap0", {"position": v(92.36, -164.56) * mm});
            skLineSegment(sketch, "E219.bottom", {"start": v(112.26, -144.36) * mm, "end": v(132.46, -144.36) * mm});
            skLineSegment(sketch, "E219.top", {"start": v(112.26, -164.56) * mm, "end": v(132.46, -164.56) * mm});
            skLineSegment(sketch, "E219.left", {"start": v(112.26, -144.36) * mm, "end": v(112.26, -164.56) * mm});
            skLineSegment(sketch, "E219.right", {"start": v(132.46, -144.36) * mm, "end": v(132.46, -164.56) * mm});
            skCircle(sketch, "E220", {"center": v(122.36, -139.46) * mm, "radius": 1.5 * mm, "construction": true});
            skCircle(sketch, "E221", {"center": v(122.36, -169.46) * mm, "radius": 1.5 * mm, "construction": true});
            skLineSegment(sketch, "E222.bottom", {"start": v(23.36, -145.46) * mm, "end": v(41.36, -145.46) * mm, "construction": true});
            skLineSegment(sketch, "E222.top", {"start": v(23.36, -163.46) * mm, "end": v(41.36, -163.46) * mm, "construction": true});
            skLineSegment(sketch, "E222.left", {"start": v(23.36, -145.46) * mm, "end": v(23.36, -163.46) * mm, "construction": true});
            skLineSegment(sketch, "E222.right", {"start": v(41.36, -145.46) * mm, "end": v(41.36, -163.46) * mm, "construction": true});
            skSolve(sketch);
        }
        {
            var Q0;
            Q0=qSketchRegion(id+"F32",true);
            extrude(context, id + "F33", {"entities" : qUnion([Q0]), "depth" : 11 * mm});
        }
        {
            var Q0;
            Q0=makeQuery(id+"F33.opExtrude","CAP_FACE",FACE,{"disambiguationData":[OSD([sQuery(id+"F32.wireOp",EDGE,"E209.bottom"),sQuery(id+"F32.wireOp",EDGE,"E209.top"),sQuery(id+"F32.wireOp",EDGE,"E209.left"),sQuery(id+"F32.wireOp",EDGE,"E209.right")])],"isStart":true});
            var sketch = newSketch(context, id + "F34", { "sketchPlane" : qUnion([Q0])});
            skLineSegment(sketch, "E223.bottom", {"start": v(16.66, 173.06) * mm, "end": v(136.66, 173.06) * mm});
            skLineSegment(sketch, "E223.top", {"start": v(16.66, 135.86) * mm, "end": v(136.66, 135.86) * mm});
            skLineSegment(sketch, "E223.left", {"start": v(16.66, 173.06) * mm, "end": v(16.66, 135.86) * mm});
            skLineSegment(sketch, "E223.right", {"start": v(136.66, 173.06) * mm, "end": v(136.66, 135.86) * mm});
            skSolve(sketch);
        }
        {
            var Q0;
            Q0=qSketchRegion(id+"F34",true);
            extrude(context, id + "F35", {"entities" : qUnion([Q0]), "operationType" : NewBodyOperationType.REMOVE, "oppositeDirection" : true, "depth" : 8 * mm});
        }
        {
            var Q0;
            Q0=makeQuery(id+"F31.opExtrude","CAP_FACE",FACE,{"disambiguationData":[OSD([sQuery(id+"F30.wireOp",EDGE,"55227c07-3752-4080-a22d-609154aa437d.0"),sQuery(id+"F30.wireOp",EDGE,"55227c07-3752-4080-a22d-609154aa437d.1"),sQuery(id+"F30.wireOp",EDGE,"55227c07-3752-4080-a22d-609154aa437d.2"),sQuery(id+"F30.wireOp",EDGE,"55227c07-3752-4080-a22d-609154aa437d.3"),sQuery(id+"F30.wireOp",EDGE,"E111"),sQuery(id+"F30.wireOp",EDGE,"E113"),sQuery(id+"F30.wireOp",EDGE,"E118.left"),sQuery(id+"F30.wireOp",EDGE,"E118.right"),sQuery(id+"F30.wireOp",EDGE,"E119.left"),sQuery(id+"F30.wireOp",EDGE,"E119.right"),sQuery(id+"F30.wireOp",EDGE,"E120.bottom"),sQuery(id+"F30.wireOp",EDGE,"E120.top"),sQuery(id+"F30.wireOp",EDGE,"E121.trimOffspring"),sQuery(id+"F30.wireOp",EDGE,"E122.trimOffspring"),sQuery(id+"F30.wireOp",EDGE,"E125.trimOffspring"),sQuery(id+"F30.wireOp",EDGE,"E126.trimOffspring"),sQuery(id+"F30.wireOp",EDGE,"E127.trimOffspring"),sQuery(id+"F30.wireOp",EDGE,"E128.trimOffspring"),sQuery(id+"F30.wireOp",EDGE,"E129.trimOffspring"),sQuery(id+"F30.wireOp",EDGE,"E130.trimOffspring"),sQuery(id+"F30.wireOp",EDGE,"E131.bottom"),sQuery(id+"F30.wireOp",EDGE,"E131.left"),sQuery(id+"F30.wireOp",EDGE,"E131.top"),sQuery(id+"F30.wireOp",EDGE,"E131.right"),sQuery(id+"F30.wireOp",EDGE,"E134"),sQuery(id+"F30.wireOp",EDGE,"E136"),sQuery(id+"F30.wireOp",EDGE,"E141.left"),sQuery(id+"F30.wireOp",EDGE,"E141.right"),sQuery(id+"F30.wireOp",EDGE,"E142.left"),sQuery(id+"F30.wireOp",EDGE,"E142.right"),sQuery(id+"F30.wireOp",EDGE,"E143.bottom"),sQuery(id+"F30.wireOp",EDGE,"E143.top"),sQuery(id+"F30.wireOp",EDGE,"E144.trimOffspring"),sQuery(id+"F30.wireOp",EDGE,"E145.trimOffspring"),sQuery(id+"F30.wireOp",EDGE,"E148.trimOffspring"),sQuery(id+"F30.wireOp",EDGE,"E149.trimOffspring"),sQuery(id+"F30.wireOp",EDGE,"E150.trimOffspring"),sQuery(id+"F30.wireOp",EDGE,"E152.trimOffspring"),sQuery(id+"F30.wireOp",EDGE,"E153.trimOffspring"),sQuery(id+"F30.wireOp",EDGE,"E155.trimOffspring"),sQuery(id+"F30.wireOp",EDGE,"E156.bottom"),sQuery(id+"F30.wireOp",EDGE,"E156.left"),sQuery(id+"F30.wireOp",EDGE,"E156.top"),sQuery(id+"F30.wireOp",EDGE,"E156.right"),sQuery(id+"F30.wireOp",EDGE,"E160"),sQuery(id+"F30.wireOp",EDGE,"E162"),sQuery(id+"F30.wireOp",EDGE,"E167.left"),sQuery(id+"F30.wireOp",EDGE,"E167.right"),sQuery(id+"F30.wireOp",EDGE,"E168.left"),sQuery(id+"F30.wireOp",EDGE,"E168.right"),sQuery(id+"F30.wireOp",EDGE,"E169.bottom"),sQuery(id+"F30.wireOp",EDGE,"E169.top"),sQuery(id+"F30.wireOp",EDGE,"E170.trimOffspring"),sQuery(id+"F30.wireOp",EDGE,"E171.trimOffspring"),sQuery(id+"F30.wireOp",EDGE,"E174.trimOffspring"),sQuery(id+"F30.wireOp",EDGE,"E175.trimOffspring"),sQuery(id+"F30.wireOp",EDGE,"E176.trimOffspring"),sQuery(id+"F30.wireOp",EDGE,"E178.trimOffspring"),sQuery(id+"F30.wireOp",EDGE,"E179.trimOffspring"),sQuery(id+"F30.wireOp",EDGE,"E181.trimOffspring"),sQuery(id+"F30.wireOp",EDGE,"E182.bottom"),sQuery(id+"F30.wireOp",EDGE,"E182.left"),sQuery(id+"F30.wireOp",EDGE,"E182.top"),sQuery(id+"F30.wireOp",EDGE,"E182.right"),sQuery(id+"F30.wireOp",EDGE,"E186"),sQuery(id+"F30.wireOp",EDGE,"E188"),sQuery(id+"F30.wireOp",EDGE,"E193.left"),sQuery(id+"F30.wireOp",EDGE,"E193.right"),sQuery(id+"F30.wireOp",EDGE,"E194.left"),sQuery(id+"F30.wireOp",EDGE,"E194.right"),sQuery(id+"F30.wireOp",EDGE,"E195.bottom"),sQuery(id+"F30.wireOp",EDGE,"E195.top"),sQuery(id+"F30.wireOp",EDGE,"E196.trimOffspring"),sQuery(id+"F30.wireOp",EDGE,"E197.trimOffspring"),sQuery(id+"F30.wireOp",EDGE,"E200.trimOffspring"),sQuery(id+"F30.wireOp",EDGE,"E201.trimOffspring"),sQuery(id+"F30.wireOp",EDGE,"E202.trimOffspring"),sQuery(id+"F30.wireOp",EDGE,"E204.trimOffspring"),sQuery(id+"F30.wireOp",EDGE,"E205.trimOffspring"),sQuery(id+"F30.wireOp",EDGE,"E207.trimOffspring"),sQuery(id+"F30.wireOp",EDGE,"E208.bottom"),sQuery(id+"F30.wireOp",EDGE,"E208.top"),sQuery(id+"F30.wireOp",EDGE,"E208.left"),sQuery(id+"F30.wireOp",EDGE,"E208.right")])],"isStart":false});
            var sketch = newSketch(context, id + "F36", { "sketchPlane" : qUnion([Q0])});
            skLineSegment(sketch, "E224.bottom", {"start": v(-94.98, -143.56) * mm, "end": v(-98.98, -143.56) * mm});
            skLineSegment(sketch, "E224.top", {"start": v(-94.98, -161.56) * mm, "end": v(-98.98, -161.56) * mm});
            skLineSegment(sketch, "E224.left", {"start": v(-94.98, -143.56) * mm, "end": v(-94.98, -161.56) * mm});
            skLineSegment(sketch, "E224.right", {"start": v(-98.98, -143.56) * mm, "end": v(-98.98, -161.56) * mm});
            skLineSegment(sketch, "E225.bottom", {"start": v(-76.98, -143.56) * mm, "end": v(-72.98, -143.56) * mm});
            skLineSegment(sketch, "E225.top", {"start": v(-76.98, -161.56) * mm, "end": v(-72.98, -161.56) * mm});
            skLineSegment(sketch, "E225.left", {"start": v(-76.98, -143.56) * mm, "end": v(-76.98, -161.56) * mm});
            skLineSegment(sketch, "E225.right", {"start": v(-72.98, -143.56) * mm, "end": v(-72.98, -161.56) * mm});
            skLineSegment(sketch, "E226.bottom", {"start": v(-64.98, -143.56) * mm, "end": v(-68.98, -143.56) * mm});
            skLineSegment(sketch, "E226.top", {"start": v(-64.98, -161.56) * mm, "end": v(-68.98, -161.56) * mm});
            skLineSegment(sketch, "E226.left", {"start": v(-64.98, -143.56) * mm, "end": v(-64.98, -161.56) * mm});
            skLineSegment(sketch, "E226.right", {"start": v(-68.98, -143.56) * mm, "end": v(-68.98, -161.56) * mm});
            skLineSegment(sketch, "E227.bottom", {"start": v(-46.98, -143.56) * mm, "end": v(-42.98, -143.56) * mm});
            skLineSegment(sketch, "E227.top", {"start": v(-46.98, -161.56) * mm, "end": v(-42.98, -161.56) * mm});
            skLineSegment(sketch, "E227.left", {"start": v(-46.98, -143.56) * mm, "end": v(-46.98, -161.56) * mm});
            skLineSegment(sketch, "E227.right", {"start": v(-42.98, -143.56) * mm, "end": v(-42.98, -161.56) * mm});
            skLineSegment(sketch, "E228.bottom", {"start": v(-34.98, -143.56) * mm, "end": v(-38.98, -143.56) * mm});
            skLineSegment(sketch, "E228.top", {"start": v(-34.98, -161.56) * mm, "end": v(-38.98, -161.56) * mm});
            skLineSegment(sketch, "E228.left", {"start": v(-34.98, -143.56) * mm, "end": v(-34.98, -161.56) * mm});
            skLineSegment(sketch, "E228.right", {"start": v(-38.98, -143.56) * mm, "end": v(-38.98, -161.56) * mm});
            skLineSegment(sketch, "E229.bottom", {"start": v(-16.98, -143.56) * mm, "end": v(-12.98, -143.56) * mm});
            skLineSegment(sketch, "E229.top", {"start": v(-16.98, -161.56) * mm, "end": v(-12.98, -161.56) * mm});
            skLineSegment(sketch, "E229.left", {"start": v(-16.98, -143.56) * mm, "end": v(-16.98, -161.56) * mm});
            skLineSegment(sketch, "E229.right", {"start": v(-12.98, -143.56) * mm, "end": v(-12.98, -161.56) * mm});
            skSolve(sketch);
        }
        {
            var Q0;
            Q0=qSketchRegion(id+"F36",true);
            extrude(context, id + "F37", {"entities" : qUnion([Q0]), "operationType" : NewBodyOperationType.ADD, "depth" : 3 * mm});
        }
        {
            var Q0;
            Q0=makeQuery(id+"F31.opExtrude","CAP_FACE",FACE,{"disambiguationData":[OSD([sQuery(id+"F30.wireOp",EDGE,"55227c07-3752-4080-a22d-609154aa437d.0"),sQuery(id+"F30.wireOp",EDGE,"55227c07-3752-4080-a22d-609154aa437d.1"),sQuery(id+"F30.wireOp",EDGE,"55227c07-3752-4080-a22d-609154aa437d.2"),sQuery(id+"F30.wireOp",EDGE,"55227c07-3752-4080-a22d-609154aa437d.3"),sQuery(id+"F30.wireOp",EDGE,"E111"),sQuery(id+"F30.wireOp",EDGE,"E113"),sQuery(id+"F30.wireOp",EDGE,"E118.left"),sQuery(id+"F30.wireOp",EDGE,"E118.right"),sQuery(id+"F30.wireOp",EDGE,"E119.left"),sQuery(id+"F30.wireOp",EDGE,"E119.right"),sQuery(id+"F30.wireOp",EDGE,"E120.bottom"),sQuery(id+"F30.wireOp",EDGE,"E120.top"),sQuery(id+"F30.wireOp",EDGE,"E121.trimOffspring"),sQuery(id+"F30.wireOp",EDGE,"E122.trimOffspring"),sQuery(id+"F30.wireOp",EDGE,"E125.trimOffspring"),sQuery(id+"F30.wireOp",EDGE,"E126.trimOffspring"),sQuery(id+"F30.wireOp",EDGE,"E127.trimOffspring"),sQuery(id+"F30.wireOp",EDGE,"E128.trimOffspring"),sQuery(id+"F30.wireOp",EDGE,"E129.trimOffspring"),sQuery(id+"F30.wireOp",EDGE,"E130.trimOffspring"),sQuery(id+"F30.wireOp",EDGE,"E131.bottom"),sQuery(id+"F30.wireOp",EDGE,"E131.left"),sQuery(id+"F30.wireOp",EDGE,"E131.top"),sQuery(id+"F30.wireOp",EDGE,"E131.right"),sQuery(id+"F30.wireOp",EDGE,"E134"),sQuery(id+"F30.wireOp",EDGE,"E136"),sQuery(id+"F30.wireOp",EDGE,"E141.left"),sQuery(id+"F30.wireOp",EDGE,"E141.right"),sQuery(id+"F30.wireOp",EDGE,"E142.left"),sQuery(id+"F30.wireOp",EDGE,"E142.right"),sQuery(id+"F30.wireOp",EDGE,"E143.bottom"),sQuery(id+"F30.wireOp",EDGE,"E143.top"),sQuery(id+"F30.wireOp",EDGE,"E144.trimOffspring"),sQuery(id+"F30.wireOp",EDGE,"E145.trimOffspring"),sQuery(id+"F30.wireOp",EDGE,"E148.trimOffspring"),sQuery(id+"F30.wireOp",EDGE,"E149.trimOffspring"),sQuery(id+"F30.wireOp",EDGE,"E150.trimOffspring"),sQuery(id+"F30.wireOp",EDGE,"E152.trimOffspring"),sQuery(id+"F30.wireOp",EDGE,"E153.trimOffspring"),sQuery(id+"F30.wireOp",EDGE,"E155.trimOffspring"),sQuery(id+"F30.wireOp",EDGE,"E156.bottom"),sQuery(id+"F30.wireOp",EDGE,"E156.left"),sQuery(id+"F30.wireOp",EDGE,"E156.top"),sQuery(id+"F30.wireOp",EDGE,"E156.right"),sQuery(id+"F30.wireOp",EDGE,"E160"),sQuery(id+"F30.wireOp",EDGE,"E162"),sQuery(id+"F30.wireOp",EDGE,"E167.left"),sQuery(id+"F30.wireOp",EDGE,"E167.right"),sQuery(id+"F30.wireOp",EDGE,"E168.left"),sQuery(id+"F30.wireOp",EDGE,"E168.right"),sQuery(id+"F30.wireOp",EDGE,"E169.bottom"),sQuery(id+"F30.wireOp",EDGE,"E169.top"),sQuery(id+"F30.wireOp",EDGE,"E170.trimOffspring"),sQuery(id+"F30.wireOp",EDGE,"E171.trimOffspring"),sQuery(id+"F30.wireOp",EDGE,"E174.trimOffspring"),sQuery(id+"F30.wireOp",EDGE,"E175.trimOffspring"),sQuery(id+"F30.wireOp",EDGE,"E176.trimOffspring"),sQuery(id+"F30.wireOp",EDGE,"E178.trimOffspring"),sQuery(id+"F30.wireOp",EDGE,"E179.trimOffspring"),sQuery(id+"F30.wireOp",EDGE,"E181.trimOffspring"),sQuery(id+"F30.wireOp",EDGE,"E182.bottom"),sQuery(id+"F30.wireOp",EDGE,"E182.left"),sQuery(id+"F30.wireOp",EDGE,"E182.top"),sQuery(id+"F30.wireOp",EDGE,"E182.right"),sQuery(id+"F30.wireOp",EDGE,"E186"),sQuery(id+"F30.wireOp",EDGE,"E188"),sQuery(id+"F30.wireOp",EDGE,"E193.left"),sQuery(id+"F30.wireOp",EDGE,"E193.right"),sQuery(id+"F30.wireOp",EDGE,"E194.left"),sQuery(id+"F30.wireOp",EDGE,"E194.right"),sQuery(id+"F30.wireOp",EDGE,"E195.bottom"),sQuery(id+"F30.wireOp",EDGE,"E195.top"),sQuery(id+"F30.wireOp",EDGE,"E196.trimOffspring"),sQuery(id+"F30.wireOp",EDGE,"E197.trimOffspring"),sQuery(id+"F30.wireOp",EDGE,"E200.trimOffspring"),sQuery(id+"F30.wireOp",EDGE,"E201.trimOffspring"),sQuery(id+"F30.wireOp",EDGE,"E202.trimOffspring"),sQuery(id+"F30.wireOp",EDGE,"E204.trimOffspring"),sQuery(id+"F30.wireOp",EDGE,"E205.trimOffspring"),sQuery(id+"F30.wireOp",EDGE,"E207.trimOffspring"),sQuery(id+"F30.wireOp",EDGE,"E208.bottom"),sQuery(id+"F30.wireOp",EDGE,"E208.top"),sQuery(id+"F30.wireOp",EDGE,"E208.left"),sQuery(id+"F30.wireOp",EDGE,"E208.right")])],"isStart":false});
            var sketch = newSketch(context, id + "F38", { "sketchPlane" : qUnion([Q0])});
            skLineSegment(sketch, "E230.bottom", {"start": v(-98.98, -143.56) * mm, "end": v(-72.98, -143.56) * mm});
            skLineSegment(sketch, "E230.top", {"start": v(-98.98, -134.06) * mm, "end": v(-72.98, -134.06) * mm});
            skLineSegment(sketch, "E230.left", {"start": v(-98.98, -143.56) * mm, "end": v(-98.98, -134.06) * mm});
            skLineSegment(sketch, "E230.right", {"start": v(-72.98, -143.56) * mm, "end": v(-72.98, -134.06) * mm});
            skLineSegment(sketch, "E231.bottom", {"start": v(-98.98, -161.56) * mm, "end": v(-72.98, -161.56) * mm});
            skLineSegment(sketch, "E231.top", {"start": v(-98.98, -171.06) * mm, "end": v(-72.98, -171.06) * mm});
            skLineSegment(sketch, "E231.left", {"start": v(-98.98, -161.56) * mm, "end": v(-98.98, -171.06) * mm});
            skLineSegment(sketch, "E231.right", {"start": v(-72.98, -161.56) * mm, "end": v(-72.98, -171.06) * mm});
            skCircle(sketch, "E232", {"center": v(-85.98, -137.56) * mm, "radius": 1.5 * mm});
            skCircle(sketch, "E233", {"center": v(-85.98, -167.56) * mm, "radius": 1.5 * mm});
            skLineSegment(sketch, "E234.bottom", {"start": v(-68.98, -143.56) * mm, "end": v(-42.98, -143.56) * mm});
            skLineSegment(sketch, "E234.top", {"start": v(-68.98, -134.06) * mm, "end": v(-42.98, -134.06) * mm});
            skLineSegment(sketch, "E234.left", {"start": v(-68.98, -143.56) * mm, "end": v(-68.98, -134.06) * mm});
            skLineSegment(sketch, "E234.right", {"start": v(-42.98, -143.56) * mm, "end": v(-42.98, -134.06) * mm});
            skLineSegment(sketch, "E235.bottom", {"start": v(-68.98, -161.56) * mm, "end": v(-42.98, -161.56) * mm});
            skLineSegment(sketch, "E235.top", {"start": v(-68.98, -171.06) * mm, "end": v(-42.98, -171.06) * mm});
            skLineSegment(sketch, "E235.left", {"start": v(-68.98, -161.56) * mm, "end": v(-68.98, -171.06) * mm});
            skLineSegment(sketch, "E235.right", {"start": v(-42.98, -161.56) * mm, "end": v(-42.98, -171.06) * mm});
            skLineSegment(sketch, "E236.bottom", {"start": v(-38.98, -143.56) * mm, "end": v(-12.98, -143.56) * mm});
            skLineSegment(sketch, "E236.top", {"start": v(-38.98, -134.06) * mm, "end": v(-12.98, -134.06) * mm});
            skLineSegment(sketch, "E236.left", {"start": v(-38.98, -143.56) * mm, "end": v(-38.98, -134.06) * mm});
            skLineSegment(sketch, "E236.right", {"start": v(-12.98, -143.56) * mm, "end": v(-12.98, -134.06) * mm});
            skLineSegment(sketch, "E237.bottom", {"start": v(-38.98, -161.56) * mm, "end": v(-12.98, -161.56) * mm});
            skLineSegment(sketch, "E237.top", {"start": v(-38.98, -171.06) * mm, "end": v(-12.98, -171.06) * mm});
            skLineSegment(sketch, "E237.left", {"start": v(-38.98, -161.56) * mm, "end": v(-38.98, -171.06) * mm});
            skLineSegment(sketch, "E237.right", {"start": v(-12.98, -161.56) * mm, "end": v(-12.98, -171.06) * mm});
            skCircle(sketch, "E238", {"center": v(-55.98, -137.56) * mm, "radius": 1.5 * mm});
            skCircle(sketch, "E239", {"center": v(-55.98, -167.56) * mm, "radius": 1.5 * mm});
            skCircle(sketch, "E240", {"center": v(-25.98, -137.56) * mm, "radius": 1.5 * mm});
            skCircle(sketch, "E241", {"center": v(-25.98, -167.56) * mm, "radius": 1.5 * mm});
            skSolve(sketch);
        }
        {
            var Q0;
            Q0=makeQuery(id+"F36.imprint","IMPRINT",FACE,{"disambiguationData":[TD([[makeQuery(id+"F36.imprint","IMPRINT",EDGE,{"derivedFrom":sQuery(id+"F36.wireOp",EDGE,"E224.bottom")}),-1.0]])]});
            var sketch = newSketch(context, id + "F39", { "sketchPlane" : qUnion([Q0])});
            skLineSegment(sketch, "E242.bottom", {"start": v(-124.98, -151.56) * mm, "end": v(-121.73, -151.56) * mm});
            skLineSegment(sketch, "E242.top", {"start": v(-124.98, -153.56) * mm, "end": v(-121.73, -153.56) * mm});
            skLineSegment(sketch, "E242.left", {"start": v(-124.98, -151.56) * mm, "end": v(-124.98, -153.56) * mm});
            skLineSegment(sketch, "E242.right", {"start": v(-121.73, -151.56) * mm, "end": v(-121.73, -153.56) * mm});
            skLineSegment(sketch, "E243.bottom", {"start": v(-110.23, -151.56) * mm, "end": v(-106.98, -151.56) * mm});
            skLineSegment(sketch, "E243.top", {"start": v(-110.23, -153.56) * mm, "end": v(-106.98, -153.56) * mm});
            skLineSegment(sketch, "E243.left", {"start": v(-110.23, -151.56) * mm, "end": v(-110.23, -153.56) * mm});
            skLineSegment(sketch, "E243.right", {"start": v(-106.98, -151.56) * mm, "end": v(-106.98, -153.56) * mm});
            skSolve(sketch);
        }
        {
            var Q0;
            Q0=qSketchRegion(id+"F39",true);
            extrude(context, id + "F40", {"entities" : qUnion([Q0]), "operationType" : NewBodyOperationType.ADD, "depth" : 9 * mm});
        }
        {
            var Q0;
            Q0=makeQuery(id+"F36.imprint","IMPRINT",FACE,{"disambiguationData":[TD([[makeQuery(id+"F36.imprint","IMPRINT",EDGE,{"derivedFrom":sQuery(id+"F36.wireOp",EDGE,"E224.bottom")}),-1.0]])]});
            var sketch = newSketch(context, id + "F41", { "sketchPlane" : qUnion([Q0])});
            skLineSegment(sketch, "E244.bottom", {"start": v(-118.48, -151.56) * mm, "end": v(-113.48, -151.56) * mm});
            skLineSegment(sketch, "E244.top", {"start": v(-118.48, -153.56) * mm, "end": v(-113.48, -153.56) * mm});
            skLineSegment(sketch, "E244.left", {"start": v(-118.48, -151.56) * mm, "end": v(-118.48, -153.56) * mm});
            skLineSegment(sketch, "E244.right", {"start": v(-113.48, -151.56) * mm, "end": v(-113.48, -153.56) * mm});
            skSolve(sketch);
        }
        {
            var Q0;
            Q0=qSketchRegion(id+"F41",true);
            extrude(context, id + "F42", {"entities" : qUnion([Q0]), "operationType" : NewBodyOperationType.ADD, "depth" : 3 * mm});
        }
        {
            var Q0;
            Q0=makeQuery(id+"F33.opExtrude","SWEPT_EDGE",EDGE,{"disambiguationData":[OSD([sQuery(id+"F32.wireOp",EDGE,"E209.bottom"),sQuery(id+"F32.wireOp",EDGE,"E209.left")])]});
            var Q1;
            Q1=makeQuery(id+"F33.opExtrude","SWEPT_EDGE",EDGE,{"disambiguationData":[OSD([sQuery(id+"F32.wireOp",EDGE,"E209.top"),sQuery(id+"F32.wireOp",EDGE,"E209.left")])]});
            var Q2;
            Q2=makeQuery(id+"F33.opExtrude","SWEPT_EDGE",EDGE,{"disambiguationData":[OSD([sQuery(id+"F32.wireOp",EDGE,"E209.top"),sQuery(id+"F32.wireOp",EDGE,"E209.right")])]});
            var Q3;
            Q3=makeQuery(id+"F33.opExtrude","SWEPT_EDGE",EDGE,{"disambiguationData":[OSD([sQuery(id+"F32.wireOp",EDGE,"E209.bottom"),sQuery(id+"F32.wireOp",EDGE,"E209.right")])]});
            var Q4;
            Q4=makeQuery(id+"F33.opExtrude","CAP_EDGE",EDGE,{"disambiguationData":[OSD([sQuery(id+"F32.wireOp",EDGE,"E209.top")])],"isStart":false});
            var Q5;
            Q5=makeQuery(id+"F33.opExtrude","CAP_EDGE",EDGE,{"disambiguationData":[OSD([sQuery(id+"F32.wireOp",EDGE,"E209.left")])],"isStart":false});
            var Q6;
            Q6=makeQuery(id+"F33.opExtrude","CAP_EDGE",EDGE,{"disambiguationData":[OSD([sQuery(id+"F32.wireOp",EDGE,"E209.bottom")])],"isStart":false});
            var Q7;
            Q7=makeQuery(id+"F33.opExtrude","CAP_EDGE",EDGE,{"disambiguationData":[OSD([sQuery(id+"F32.wireOp",EDGE,"E209.right")])],"isStart":false});
            fillet(context, id + "F43", {"entities" : qUnion([Q0, Q1, Q2, Q3, Q4, Q5, Q6, Q7]), "radius" : 1 * mm, "tangentPropagation" : true, "allowEdgeOverflow" : false});
        }
        {
            var Q0;
            Q0=makeQuery(id+"F10.opExtrude","SWEPT_EDGE",EDGE,{"disambiguationData":[OSD([sQuery(id+"F9.wireOp",EDGE,"E41.top"),sQuery(id+"F9.wireOp",EDGE,"E41.right")])]});
            var Q1;
            Q1=makeQuery(id+"F10.opExtrude","CAP_EDGE",EDGE,{"disambiguationData":[OSD([sQuery(id+"F9.wireOp",EDGE,"E41.top")])],"isStart":false});
            var Q2;
            Q2=makeQuery(id+"F10.opExtrude","CAP_EDGE",EDGE,{"disambiguationData":[OSD([sQuery(id+"F9.wireOp",EDGE,"E41.right")])],"isStart":false});
            var Q3;
            Q3=makeQuery(id+"F10.opExtrude","SWEPT_EDGE",EDGE,{"disambiguationData":[OSD([sQuery(id+"F9.wireOp",EDGE,"E41.bottom"),sQuery(id+"F9.wireOp",EDGE,"E41.right")])]});
            var Q4;
            Q4=makeQuery(id+"F10.opExtrude","CAP_EDGE",EDGE,{"disambiguationData":[OSD([sQuery(id+"F9.wireOp",EDGE,"E41.bottom")])],"isStart":false});
            var Q5;
            Q5=makeQuery(id+"F10.opExtrude","SWEPT_EDGE",EDGE,{"disambiguationData":[OSD([sQuery(id+"F9.wireOp",EDGE,"E41.bottom"),sQuery(id+"F9.wireOp",EDGE,"E41.left")])]});
            var Q6;
            Q6=makeQuery(id+"F10.opExtrude","CAP_EDGE",EDGE,{"disambiguationData":[OSD([sQuery(id+"F9.wireOp",EDGE,"E41.left")])],"isStart":false});
            var Q7;
            Q7=makeQuery(id+"F10.opExtrude","SWEPT_EDGE",EDGE,{"disambiguationData":[OSD([sQuery(id+"F9.wireOp",EDGE,"E41.top"),sQuery(id+"F9.wireOp",EDGE,"E41.left")])]});
            var Q8;
            Q8=makeQuery(id+"F1.opExtrude","SWEPT_EDGE",EDGE,{"disambiguationData":[OSD([sQuery(id+"F0.wireOp",EDGE,"E1.bottom"),sQuery(id+"F0.wireOp",EDGE,"E1.right")])]});
            var Q9;
            Q9=makeQuery(id+"F1.opExtrude","CAP_EDGE",EDGE,{"disambiguationData":[OSD([sQuery(id+"F0.wireOp",EDGE,"E1.bottom")])],"isStart":false});
            var Q10;
            Q10=makeQuery(id+"F1.opExtrude","SWEPT_EDGE",EDGE,{"disambiguationData":[OSD([sQuery(id+"F0.wireOp",EDGE,"E1.bottom"),sQuery(id+"F0.wireOp",EDGE,"E1.left")])]});
            var Q11;
            Q11=makeQuery(id+"F1.opExtrude","CAP_EDGE",EDGE,{"disambiguationData":[OSD([sQuery(id+"F0.wireOp",EDGE,"E1.right")])],"isStart":false});
            var Q12;
            Q12=makeQuery(id+"F1.opExtrude","SWEPT_EDGE",EDGE,{"disambiguationData":[OSD([sQuery(id+"F0.wireOp",EDGE,"E1.top"),sQuery(id+"F0.wireOp",EDGE,"E1.right")])]});
            var Q13;
            Q13=makeQuery(id+"F1.opExtrude","CAP_EDGE",EDGE,{"disambiguationData":[OSD([sQuery(id+"F0.wireOp",EDGE,"E1.top")])],"isStart":false});
            var Q14;
            Q14=makeQuery(id+"F1.opExtrude","SWEPT_EDGE",EDGE,{"disambiguationData":[OSD([sQuery(id+"F0.wireOp",EDGE,"E1.top"),sQuery(id+"F0.wireOp",EDGE,"E1.left")])]});
            var Q15;
            Q15=makeQuery(id+"F1.opExtrude","CAP_EDGE",EDGE,{"disambiguationData":[OSD([sQuery(id+"F0.wireOp",EDGE,"E1.left")])],"isStart":false});
            fillet(context, id + "F44", {"entities" : qUnion([Q0, Q1, Q2, Q3, Q4, Q5, Q6, Q7, Q8, Q9, Q10, Q11, Q12, Q13, Q14, Q15]), "radius" : 0.5 * mm, "tangentPropagation" : true, "allowEdgeOverflow" : false});
        }
        {
            var Q0;
            Q0=makeQuery(id+"F38.imprint","IMPRINT",FACE,{"disambiguationData":[TD([[makeQuery(id+"F38.imprint","IMPRINT",EDGE,{"derivedFrom":sQuery(id+"F38.wireOp",EDGE,"E230.top")}),-1.0]])]});
            var Q1;
            Q1=makeQuery(id+"F38.imprint","IMPRINT",FACE,{"disambiguationData":[TD([[makeQuery(id+"F38.imprint","IMPRINT",EDGE,{"derivedFrom":sQuery(id+"F38.wireOp",EDGE,"E231.top")}),1.0]])]});
            var Q2;
            Q2=makeQuery(id+"F38.imprint","IMPRINT",FACE,{"disambiguationData":[TD([[makeQuery(id+"F38.imprint","IMPRINT",EDGE,{"derivedFrom":sQuery(id+"F38.wireOp",EDGE,"E235.top")}),1.0]])]});
            var Q3;
            Q3=makeQuery(id+"F38.imprint","IMPRINT",FACE,{"disambiguationData":[TD([[makeQuery(id+"F38.imprint","IMPRINT",EDGE,{"derivedFrom":sQuery(id+"F38.wireOp",EDGE,"E234.top")}),-1.0]])]});
            var Q4;
            Q4=makeQuery(id+"F38.imprint","IMPRINT",FACE,{"disambiguationData":[TD([[makeQuery(id+"F38.imprint","IMPRINT",EDGE,{"derivedFrom":sQuery(id+"F38.wireOp",EDGE,"E236.top")}),-1.0]])]});
            var Q5;
            Q5=makeQuery(id+"F38.imprint","IMPRINT",FACE,{"disambiguationData":[TD([[makeQuery(id+"F38.imprint","IMPRINT",EDGE,{"derivedFrom":sQuery(id+"F38.wireOp",EDGE,"E237.top")}),1.0]])]});
            extrude(context, id + "F45", {"entities" : qUnion([Q0, Q1, Q2, Q3, Q4, Q5]), "operationType" : NewBodyOperationType.ADD, "depth" : 3 * mm});
        }
        {
            var Q0;
            Q0=makeQuery(id+"F31.opExtrude","SWEPT_FACE",FACE,{"disambiguationData":[OSD([sQuery(id+"F30.wireOp",EDGE,"E208.left")])]});
            extrude(context, id + "F46", {"entities" : qUnion([Q0]), "operationType" : NewBodyOperationType.ADD, "depth" : 2 * mm});
        }
        {
            var Q0;
            {var subQ0=sQuery(id+"F30.wireOp",EDGE,"E208.left");var subQ1=sQuery(id+"F30.wireOp",EDGE,"55227c07-3752-4080-a22d-609154aa437d.3");var subQ2=sQuery(id+"F30.wireOp",EDGE,"55227c07-3752-4080-a22d-609154aa437d.0");var subQ4=sQuery(id+"F30.wireOp",EDGE,"E129.trimOffspring");var subQ6=sQuery(id+"F30.wireOp",EDGE,"E208.top");var subQ7=sQuery(id+"F30.wireOp",EDGE,"E130.trimOffspring");var subQ8=sQuery(id+"F30.wireOp",EDGE,"55227c07-3752-4080-a22d-609154aa437d.2");var subQ11=sQuery(id+"F30.wireOp",EDGE,"E128.trimOffspring");var subQ13=sQuery(id+"F30.wireOp",EDGE,"E208.bottom");var subQ14=sQuery(id+"F30.wireOp",EDGE,"E122.trimOffspring");var subQ16=sQuery(id+"F30.wireOp",EDGE,"E127.trimOffspring");var subQ17=sQuery(id+"F30.wireOp",EDGE,"E126.trimOffspring");var subQ18=sQuery(id+"F30.wireOp",EDGE,"55227c07-3752-4080-a22d-609154aa437d.1");var subQ21=sQuery(id+"F30.wireOp",EDGE,"E120.bottom");var subQ22=sQuery(id+"F30.wireOp",EDGE,"E119.right");var subQ24=sQuery(id+"F30.wireOp",EDGE,"E118.right");var subQ26=sQuery(id+"F30.wireOp",EDGE,"E119.left");var subQ28=sQuery(id+"F30.wireOp",EDGE,"E121.trimOffspring");var subQ29=sQuery(id+"F30.wireOp",EDGE,"E120.top");var subQ30=sQuery(id+"F30.wireOp",EDGE,"E118.left");var subQ31=sQuery(id+"F30.wireOp",EDGE,"E111");var subQ32=sQuery(id+"F30.wireOp",EDGE,"E113");var subQ33=sQuery(id+"F30.wireOp",EDGE,"E125.trimOffspring");Q0=makeQuery(id+"F46.boolean.opBoolean","MERGE",FACE,{"derivedFrom":[makeQuery(id+"F45.boolean.opBoolean","SPLIT",FACE,{"disambiguationData":[TD([makeQuery(id+"F31.opExtrude","SWEPT_FACE",FACE,{"disambiguationData":[OSD([subQ31])]})])],"derivedFrom":makeQuery(id+"F31.opExtrude","CAP_FACE",FACE,{"disambiguationData":[OSD([subQ2,subQ18,subQ8,subQ1,subQ31,subQ32,subQ30,subQ24,subQ26,subQ22,subQ21,subQ29,subQ28,subQ14,subQ33,subQ17,subQ16,subQ11,subQ4,subQ7,sQuery(id+"F30.wireOp",EDGE,"E131.bottom"),sQuery(id+"F30.wireOp",EDGE,"E131.left"),sQuery(id+"F30.wireOp",EDGE,"E131.top"),sQuery(id+"F30.wireOp",EDGE,"E131.right"),sQuery(id+"F30.wireOp",EDGE,"E134"),sQuery(id+"F30.wireOp",EDGE,"E136"),sQuery(id+"F30.wireOp",EDGE,"E141.left"),sQuery(id+"F30.wireOp",EDGE,"E141.right"),sQuery(id+"F30.wireOp",EDGE,"E142.left"),sQuery(id+"F30.wireOp",EDGE,"E142.right"),sQuery(id+"F30.wireOp",EDGE,"E143.bottom"),sQuery(id+"F30.wireOp",EDGE,"E143.top"),sQuery(id+"F30.wireOp",EDGE,"E144.trimOffspring"),sQuery(id+"F30.wireOp",EDGE,"E145.trimOffspring"),sQuery(id+"F30.wireOp",EDGE,"E148.trimOffspring"),sQuery(id+"F30.wireOp",EDGE,"E149.trimOffspring"),sQuery(id+"F30.wireOp",EDGE,"E150.trimOffspring"),sQuery(id+"F30.wireOp",EDGE,"E152.trimOffspring"),sQuery(id+"F30.wireOp",EDGE,"E153.trimOffspring"),sQuery(id+"F30.wireOp",EDGE,"E155.trimOffspring"),sQuery(id+"F30.wireOp",EDGE,"E156.bottom"),sQuery(id+"F30.wireOp",EDGE,"E156.left"),sQuery(id+"F30.wireOp",EDGE,"E156.top"),sQuery(id+"F30.wireOp",EDGE,"E156.right"),sQuery(id+"F30.wireOp",EDGE,"E160"),sQuery(id+"F30.wireOp",EDGE,"E162"),sQuery(id+"F30.wireOp",EDGE,"E167.left"),sQuery(id+"F30.wireOp",EDGE,"E167.right"),sQuery(id+"F30.wireOp",EDGE,"E168.left"),sQuery(id+"F30.wireOp",EDGE,"E168.right"),sQuery(id+"F30.wireOp",EDGE,"E169.bottom"),sQuery(id+"F30.wireOp",EDGE,"E169.top"),sQuery(id+"F30.wireOp",EDGE,"E170.trimOffspring"),sQuery(id+"F30.wireOp",EDGE,"E171.trimOffspring"),sQuery(id+"F30.wireOp",EDGE,"E174.trimOffspring"),sQuery(id+"F30.wireOp",EDGE,"E175.trimOffspring"),sQuery(id+"F30.wireOp",EDGE,"E176.trimOffspring"),sQuery(id+"F30.wireOp",EDGE,"E178.trimOffspring"),sQuery(id+"F30.wireOp",EDGE,"E179.trimOffspring"),sQuery(id+"F30.wireOp",EDGE,"E181.trimOffspring"),sQuery(id+"F30.wireOp",EDGE,"E182.bottom"),sQuery(id+"F30.wireOp",EDGE,"E182.left"),sQuery(id+"F30.wireOp",EDGE,"E182.top"),sQuery(id+"F30.wireOp",EDGE,"E182.right"),sQuery(id+"F30.wireOp",EDGE,"E186"),sQuery(id+"F30.wireOp",EDGE,"E188"),sQuery(id+"F30.wireOp",EDGE,"E193.left"),sQuery(id+"F30.wireOp",EDGE,"E193.right"),sQuery(id+"F30.wireOp",EDGE,"E194.left"),sQuery(id+"F30.wireOp",EDGE,"E194.right"),sQuery(id+"F30.wireOp",EDGE,"E195.bottom"),sQuery(id+"F30.wireOp",EDGE,"E195.top"),sQuery(id+"F30.wireOp",EDGE,"E196.trimOffspring"),sQuery(id+"F30.wireOp",EDGE,"E197.trimOffspring"),sQuery(id+"F30.wireOp",EDGE,"E200.trimOffspring"),sQuery(id+"F30.wireOp",EDGE,"E201.trimOffspring"),sQuery(id+"F30.wireOp",EDGE,"E202.trimOffspring"),sQuery(id+"F30.wireOp",EDGE,"E204.trimOffspring"),sQuery(id+"F30.wireOp",EDGE,"E205.trimOffspring"),sQuery(id+"F30.wireOp",EDGE,"E207.trimOffspring"),subQ13,subQ6,subQ0,sQuery(id+"F30.wireOp",EDGE,"E208.right")])],"isStart":false})}),makeQuery(id+"F46.opExtrude","SWEPT_FACE",FACE,{"disambiguationData":[OSD([subQ0]),TDD([makeQuery(id+"F31.opExtrude","CAP_EDGE",EDGE,{"disambiguationData":[OSD([subQ0])],"isStart":false})])]})]});}
            var sketch = newSketch(context, id + "F47", { "sketchPlane" : qUnion([Q0])});
            skLineSegment(sketch, "E245.bottom", {"start": v(-131.58, -134.06) * mm, "end": v(-129.58, -134.06) * mm});
            skLineSegment(sketch, "E245.top", {"start": v(-131.58, -171.06) * mm, "end": v(-129.58, -171.06) * mm});
            skLineSegment(sketch, "E245.left", {"start": v(-131.58, -134.06) * mm, "end": v(-131.58, -171.06) * mm});
            skLineSegment(sketch, "E245.right", {"start": v(-129.58, -134.06) * mm, "end": v(-129.58, -171.06) * mm});
            skSolve(sketch);
        }
        {
            var Q0;
            Q0=qSketchRegion(id+"F47",true);
            extrude(context, id + "F48", {"entities" : qUnion([Q0]), "operationType" : NewBodyOperationType.ADD, "depth" : 7 * mm});
        }
        {
            var Q0;
            Q0=makeQuery(id+"F35.boolean.opBoolean","COPY",FACE,{"derivedFrom":makeQuery(id+"F35.opExtrude","CAP_FACE",FACE,{"disambiguationData":[OSD([sQuery(id+"F34.wireOp",EDGE,"E223.bottom"),sQuery(id+"F34.wireOp",EDGE,"E223.top"),sQuery(id+"F34.wireOp",EDGE,"E223.left"),sQuery(id+"F34.wireOp",EDGE,"E223.right")])],"isStart":false})});
            var sketch = newSketch(context, id + "F49", { "sketchPlane" : qUnion([Q0])});
            skLineSegment(sketch, "E246.bottom", {"start": v(22.26, 164.56) * mm, "end": v(42.46, 164.56) * mm});
            skLineSegment(sketch, "E246.top", {"start": v(22.26, 173.06) * mm, "end": v(42.46, 173.06) * mm});
            skLineSegment(sketch, "E246.left", {"start": v(22.26, 164.56) * mm, "end": v(22.26, 173.06) * mm});
            skLineSegment(sketch, "E246.right", {"start": v(42.46, 164.56) * mm, "end": v(42.46, 173.06) * mm});
            skLineSegment(sketch, "E247.bottom", {"start": v(22.26, 144.36) * mm, "end": v(42.46, 144.36) * mm});
            skLineSegment(sketch, "E247.top", {"start": v(22.26, 135.86) * mm, "end": v(42.46, 135.86) * mm});
            skLineSegment(sketch, "E247.left", {"start": v(22.26, 144.36) * mm, "end": v(22.26, 135.86) * mm});
            skLineSegment(sketch, "E247.right", {"start": v(42.46, 144.36) * mm, "end": v(42.46, 135.86) * mm});
            skSolve(sketch);
        }
        {
            var Q0;
            Q0=qSketchRegion(id+"F49",true);
            extrude(context, id + "F50", {"entities" : qUnion([Q0]), "operationType" : NewBodyOperationType.ADD, "depth" : 3 * mm});
        }
        {
            var Q0;
            Q0=makeQuery(id+"F33.opExtrude","SWEPT_FACE",FACE,{"disambiguationData":[OSD([sQuery(id+"F32.wireOp",EDGE,"E209.left")])]});
            var sketch = newSketch(context, id + "F51", { "sketchPlane" : qUnion([Q0])});
            skCircle(sketch, "E248", {"center": v(139.86, 5.5) * mm, "radius": 1.5 * mm});
            skCircle(sketch, "E249", {"center": v(169.06, 5.5) * mm, "radius": 1.5 * mm});
            skSolve(sketch);
        }
        {
            var Q0;
            Q0=qSketchRegion(id+"F51",true);
            extrude(context, id + "F52", {"entities" : qUnion([Q0]), "operationType" : NewBodyOperationType.REMOVE, "oppositeDirection" : true, "depth" : 3 * mm});
        }
        {
            var Q0;
            Q0=makeQuery(id+"F48.boolean.opBoolean","MERGE",FACE,{"derivedFrom":[makeQuery(id+"F46.opExtrude","CAP_FACE",FACE,{"disambiguationData":[OSD([sQuery(id+"F30.wireOp",EDGE,"E208.left")])],"isStart":false}),makeQuery(id+"F48.opExtrude","SWEPT_FACE",FACE,{"disambiguationData":[OSD([sQuery(id+"F47.wireOp",EDGE,"E245.left")])]})]});
            var sketch = newSketch(context, id + "F53", { "sketchPlane" : qUnion([Q0])});
            skCircle(sketch, "E250", {"center": v(137.96, 5.5) * mm, "radius": 1.1 * mm});
            skCircle(sketch, "E251", {"center": v(167.16, 5.5) * mm, "radius": 1.1 * mm});
            skSolve(sketch);
        }
        {
            var Q0;
            Q0=makeQuery(id+"F33.opExtrude","SWEPT_FACE",FACE,{"disambiguationData":[OSD([sQuery(id+"F32.wireOp",EDGE,"E209.right")])]});
            var sketch = newSketch(context, id + "F54", { "sketchPlane" : qUnion([Q0])});
            skCircle(sketch, "E252", {"center": v(-169.06, 5.5) * mm, "radius": 1.5 * mm});
            skCircle(sketch, "E253", {"center": v(-139.86, 5.5) * mm, "radius": 1.5 * mm});
            skSolve(sketch);
        }
        {
            var Q0;
            Q0=makeQuery(id+"F54.imprint","IMPRINT",FACE,{"disambiguationData":[TD([[makeQuery(id+"F54.imprint","IMPRINT",EDGE,{"derivedFrom":sQuery(id+"F54.wireOp",EDGE,"E252")}),1.0]])]});
            var Q1;
            Q1=makeQuery(id+"F54.imprint","IMPRINT",FACE,{"disambiguationData":[TD([[makeQuery(id+"F54.imprint","IMPRINT",EDGE,{"derivedFrom":sQuery(id+"F54.wireOp",EDGE,"E253")}),1.0]])]});
            extrude(context, id + "F55", {"entities" : qUnion([Q0, Q1]), "operationType" : NewBodyOperationType.REMOVE, "oppositeDirection" : true, "depth" : 2 * mm});
        }
        {
            var Q0;
            {var subQ0=sQuery(id+"F34.wireOp",EDGE,"E223.top");var subQ1=sQuery(id+"F34.wireOp",EDGE,"E223.bottom");var subQ2=sQuery(id+"F34.wireOp",EDGE,"E223.right");Q0=makeQuery(id+"F50.boolean.opBoolean","SPLIT",FACE,{"disambiguationData":[TD([makeQuery(id+"F33.opExtrude","SWEPT_FACE",FACE,{"disambiguationData":[OSD([sQuery(id+"F32.wireOp",EDGE,"E210.right")])]})])],"derivedFrom":makeQuery(id+"F35.boolean.opBoolean","COPY",FACE,{"derivedFrom":makeQuery(id+"F35.opExtrude","CAP_FACE",FACE,{"disambiguationData":[OSD([subQ1,subQ0,sQuery(id+"F34.wireOp",EDGE,"E223.left"),subQ2])],"isStart":false})})});}
            var sketch = newSketch(context, id + "F56", { "sketchPlane" : qUnion([Q0])});
            skLineSegment(sketch, "E254.bottom", {"start": v(45.96, 173.06) * mm, "end": v(48.96, 173.06) * mm});
            skLineSegment(sketch, "E254.top", {"start": v(45.96, 135.86) * mm, "end": v(48.96, 135.86) * mm});
            skLineSegment(sketch, "E254.left", {"start": v(45.96, 173.06) * mm, "end": v(45.96, 135.86) * mm});
            skLineSegment(sketch, "E254.right", {"start": v(48.96, 173.06) * mm, "end": v(48.96, 135.86) * mm});
            skLineSegment(sketch, "E255.bottom", {"start": v(75.96, 173.06) * mm, "end": v(78.96, 173.06) * mm});
            skLineSegment(sketch, "E255.top", {"start": v(75.96, 135.86) * mm, "end": v(78.96, 135.86) * mm});
            skLineSegment(sketch, "E255.left", {"start": v(75.96, 173.06) * mm, "end": v(75.96, 135.86) * mm});
            skLineSegment(sketch, "E255.right", {"start": v(78.96, 173.06) * mm, "end": v(78.96, 135.86) * mm});
            skLineSegment(sketch, "E256.bottom", {"start": v(105.96, 173.06) * mm, "end": v(108.96, 173.06) * mm});
            skLineSegment(sketch, "E256.top", {"start": v(105.96, 135.86) * mm, "end": v(108.96, 135.86) * mm});
            skLineSegment(sketch, "E256.left", {"start": v(105.96, 173.06) * mm, "end": v(105.96, 135.86) * mm});
            skLineSegment(sketch, "E256.right", {"start": v(108.96, 173.06) * mm, "end": v(108.96, 135.86) * mm});
            skSolve(sketch);
        }
        {
            var Q0;
            Q0=qSketchRegion(id+"F56",true);
            extrude(context, id + "F57", {"entities" : qUnion([Q0]), "operationType" : NewBodyOperationType.ADD, "depth" : 1 * mm});
        }
        {
            var Q0;
            Q0=makeQuery(id+"F45.boolean.opBoolean","MERGE",FACE,{"derivedFrom":[makeQuery(id+"F37.opExtrude","SWEPT_FACE",FACE,{"disambiguationData":[OSD([sQuery(id+"F36.wireOp",EDGE,"E229.right")])]}),makeQuery(id+"F45.opExtrude","SWEPT_FACE",FACE,{"disambiguationData":[OSD([sQuery(id+"F38.wireOp",EDGE,"E236.right")])]}),makeQuery(id+"F45.opExtrude","SWEPT_FACE",FACE,{"disambiguationData":[OSD([sQuery(id+"F38.wireOp",EDGE,"E237.right")])]})]});
            extrude(context, id + "F58", {"entities" : qUnion([Q0]), "operationType" : NewBodyOperationType.ADD, "depth" : 1 * mm});
        }
        {
            var Q0;
            {var subQ0=sQuery(id+"F38.wireOp",EDGE,"E237.right");var subQ1=sQuery(id+"F38.wireOp",EDGE,"E236.right");var subQ2=sQuery(id+"F36.wireOp",EDGE,"E229.right");Q0=makeQuery(id+"F58.boolean.opBoolean","MERGE",FACE,{"derivedFrom":[makeQuery(id+"F45.boolean.opBoolean","MERGE",FACE,{"derivedFrom":[makeQuery(id+"F37.opExtrude","CAP_FACE",FACE,{"disambiguationData":[OSD([sQuery(id+"F36.wireOp",EDGE,"E228.bottom"),sQuery(id+"F36.wireOp",EDGE,"E228.top"),sQuery(id+"F36.wireOp",EDGE,"E228.left"),sQuery(id+"F36.wireOp",EDGE,"E228.right")])],"isStart":false}),makeQuery(id+"F37.opExtrude","CAP_FACE",FACE,{"disambiguationData":[OSD([sQuery(id+"F36.wireOp",EDGE,"E229.bottom"),sQuery(id+"F36.wireOp",EDGE,"E229.top"),sQuery(id+"F36.wireOp",EDGE,"E229.left"),subQ2])],"isStart":false}),makeQuery(id+"F45.opExtrude","CAP_FACE",FACE,{"disambiguationData":[OSD([sQuery(id+"F38.wireOp",EDGE,"E236.bottom"),sQuery(id+"F38.wireOp",EDGE,"E236.top"),sQuery(id+"F38.wireOp",EDGE,"E236.left"),subQ1,sQuery(id+"F38.wireOp",EDGE,"E240")])],"isStart":false}),makeQuery(id+"F45.opExtrude","CAP_FACE",FACE,{"disambiguationData":[OSD([sQuery(id+"F38.wireOp",EDGE,"E237.bottom"),sQuery(id+"F38.wireOp",EDGE,"E237.top"),sQuery(id+"F38.wireOp",EDGE,"E237.left"),subQ0,sQuery(id+"F38.wireOp",EDGE,"E241")])],"isStart":false})]}),makeQuery(id+"F58.opExtrude","SWEPT_FACE",FACE,{"disambiguationData":[OSD([subQ2,subQ1,subQ0]),TDD([makeQuery(id+"F45.boolean.opBoolean","MERGE",EDGE,{"derivedFrom":[makeQuery(id+"F37.opExtrude","CAP_EDGE",EDGE,{"disambiguationData":[OSD([subQ2])],"isStart":false}),makeQuery(id+"F45.opExtrude","CAP_EDGE",EDGE,{"disambiguationData":[OSD([subQ1])],"isStart":false}),makeQuery(id+"F45.opExtrude","CAP_EDGE",EDGE,{"disambiguationData":[OSD([subQ0])],"isStart":false})]})])]})]});}
            var sketch = newSketch(context, id + "F59", { "sketchPlane" : qUnion([Q0])});
            skLineSegment(sketch, "E257.bottom", {"start": v(-11.98, -171.06) * mm, "end": v(-13.98, -171.06) * mm});
            skLineSegment(sketch, "E257.top", {"start": v(-11.98, -134.06) * mm, "end": v(-13.98, -134.06) * mm});
            skLineSegment(sketch, "E257.left", {"start": v(-11.98, -171.06) * mm, "end": v(-11.98, -134.06) * mm});
            skLineSegment(sketch, "E257.right", {"start": v(-13.98, -171.06) * mm, "end": v(-13.98, -134.06) * mm});
            skSolve(sketch);
        }
        {
            var Q0;
            Q0=qSketchRegion(id+"F59",true);
            extrude(context, id + "F60", {"entities" : qUnion([Q0]), "operationType" : NewBodyOperationType.ADD, "depth" : 4 * mm});
        }
        {
            var Q0;
            Q0=qSketchRegion(id+"F53",true);
            extrude(context, id + "F61", {"entities" : qUnion([Q0]), "operationType" : NewBodyOperationType.REMOVE, "endBound" : BoundingType.THROUGH_ALL, "oppositeDirection" : true, "depth" : 3 * mm});
        }
        {
            var Q0;
            Q0=qSketchRegion(id+"F56",true);
            extrude(context, id + "F62", {"entities" : qUnion([Q0]), "operationType" : NewBodyOperationType.ADD, "depth" : 3 * mm});
        }
        {
            var Q0;
            Q0=makeQuery(id+"F45.boolean.opBoolean","MERGE",FACE,{"derivedFrom":[makeQuery(id+"F37.opExtrude","SWEPT_FACE",FACE,{"disambiguationData":[OSD([sQuery(id+"F36.wireOp",EDGE,"E225.right")])]}),makeQuery(id+"F45.opExtrude","SWEPT_FACE",FACE,{"disambiguationData":[OSD([sQuery(id+"F38.wireOp",EDGE,"E230.right")])]}),makeQuery(id+"F45.opExtrude","SWEPT_FACE",FACE,{"disambiguationData":[OSD([sQuery(id+"F38.wireOp",EDGE,"E231.right")])]})]});
            var Q1;
            Q1=makeQuery(id+"F45.boolean.opBoolean","MERGE",FACE,{"derivedFrom":[makeQuery(id+"F37.opExtrude","SWEPT_FACE",FACE,{"disambiguationData":[OSD([sQuery(id+"F36.wireOp",EDGE,"E227.right")])]}),makeQuery(id+"F45.opExtrude","SWEPT_FACE",FACE,{"disambiguationData":[OSD([sQuery(id+"F38.wireOp",EDGE,"E234.right")])]}),makeQuery(id+"F45.opExtrude","SWEPT_FACE",FACE,{"disambiguationData":[OSD([sQuery(id+"F38.wireOp",EDGE,"E235.right")])]})]});
            extrude(context, id + "F63", {"entities" : qUnion([Q0, Q1]), "operationType" : NewBodyOperationType.ADD, "depth" : 5 * mm});
        }
        {
            var Q0;
            Q0=makeQuery(id+"F30.imprint","IMPRINT",FACE,{"disambiguationData":[TD([[makeQuery(id+"F30.imprint","IMPRINT",EDGE,{"derivedFrom":sQuery(id+"F30.wireOp",EDGE,"E111")}),-1.0]])]});
            var Q1;
            {var subQ0=sQuery(id+"F30.wireOp",EDGE,"E208.left");Q1=makeQuery(id+"F46.boolean.opBoolean","MERGE",FACE,{"derivedFrom":[makeQuery(id+"F31.opExtrude","CAP_FACE",FACE,{"disambiguationData":[OSD([sQuery(id+"F30.wireOp",EDGE,"55227c07-3752-4080-a22d-609154aa437d.0"),sQuery(id+"F30.wireOp",EDGE,"55227c07-3752-4080-a22d-609154aa437d.1"),sQuery(id+"F30.wireOp",EDGE,"55227c07-3752-4080-a22d-609154aa437d.2"),sQuery(id+"F30.wireOp",EDGE,"55227c07-3752-4080-a22d-609154aa437d.3"),sQuery(id+"F30.wireOp",EDGE,"E111"),sQuery(id+"F30.wireOp",EDGE,"E113"),sQuery(id+"F30.wireOp",EDGE,"E118.left"),sQuery(id+"F30.wireOp",EDGE,"E118.right"),sQuery(id+"F30.wireOp",EDGE,"E119.left"),sQuery(id+"F30.wireOp",EDGE,"E119.right"),sQuery(id+"F30.wireOp",EDGE,"E120.bottom"),sQuery(id+"F30.wireOp",EDGE,"E120.top"),sQuery(id+"F30.wireOp",EDGE,"E121.trimOffspring"),sQuery(id+"F30.wireOp",EDGE,"E122.trimOffspring"),sQuery(id+"F30.wireOp",EDGE,"E125.trimOffspring"),sQuery(id+"F30.wireOp",EDGE,"E126.trimOffspring"),sQuery(id+"F30.wireOp",EDGE,"E127.trimOffspring"),sQuery(id+"F30.wireOp",EDGE,"E128.trimOffspring"),sQuery(id+"F30.wireOp",EDGE,"E129.trimOffspring"),sQuery(id+"F30.wireOp",EDGE,"E130.trimOffspring"),sQuery(id+"F30.wireOp",EDGE,"E131.bottom"),sQuery(id+"F30.wireOp",EDGE,"E131.left"),sQuery(id+"F30.wireOp",EDGE,"E131.top"),sQuery(id+"F30.wireOp",EDGE,"E131.right"),sQuery(id+"F30.wireOp",EDGE,"E134"),sQuery(id+"F30.wireOp",EDGE,"E136"),sQuery(id+"F30.wireOp",EDGE,"E141.left"),sQuery(id+"F30.wireOp",EDGE,"E141.right"),sQuery(id+"F30.wireOp",EDGE,"E142.left"),sQuery(id+"F30.wireOp",EDGE,"E142.right"),sQuery(id+"F30.wireOp",EDGE,"E143.bottom"),sQuery(id+"F30.wireOp",EDGE,"E143.top"),sQuery(id+"F30.wireOp",EDGE,"E144.trimOffspring"),sQuery(id+"F30.wireOp",EDGE,"E145.trimOffspring"),sQuery(id+"F30.wireOp",EDGE,"E148.trimOffspring"),sQuery(id+"F30.wireOp",EDGE,"E149.trimOffspring"),sQuery(id+"F30.wireOp",EDGE,"E150.trimOffspring"),sQuery(id+"F30.wireOp",EDGE,"E152.trimOffspring"),sQuery(id+"F30.wireOp",EDGE,"E153.trimOffspring"),sQuery(id+"F30.wireOp",EDGE,"E155.trimOffspring"),sQuery(id+"F30.wireOp",EDGE,"E156.bottom"),sQuery(id+"F30.wireOp",EDGE,"E156.left"),sQuery(id+"F30.wireOp",EDGE,"E156.top"),sQuery(id+"F30.wireOp",EDGE,"E156.right"),sQuery(id+"F30.wireOp",EDGE,"E160"),sQuery(id+"F30.wireOp",EDGE,"E162"),sQuery(id+"F30.wireOp",EDGE,"E167.left"),sQuery(id+"F30.wireOp",EDGE,"E167.right"),sQuery(id+"F30.wireOp",EDGE,"E168.left"),sQuery(id+"F30.wireOp",EDGE,"E168.right"),sQuery(id+"F30.wireOp",EDGE,"E169.bottom"),sQuery(id+"F30.wireOp",EDGE,"E169.top"),sQuery(id+"F30.wireOp",EDGE,"E170.trimOffspring"),sQuery(id+"F30.wireOp",EDGE,"E171.trimOffspring"),sQuery(id+"F30.wireOp",EDGE,"E174.trimOffspring"),sQuery(id+"F30.wireOp",EDGE,"E175.trimOffspring"),sQuery(id+"F30.wireOp",EDGE,"E176.trimOffspring"),sQuery(id+"F30.wireOp",EDGE,"E178.trimOffspring"),sQuery(id+"F30.wireOp",EDGE,"E179.trimOffspring"),sQuery(id+"F30.wireOp",EDGE,"E181.trimOffspring"),sQuery(id+"F30.wireOp",EDGE,"E182.bottom"),sQuery(id+"F30.wireOp",EDGE,"E182.left"),sQuery(id+"F30.wireOp",EDGE,"E182.top"),sQuery(id+"F30.wireOp",EDGE,"E182.right"),sQuery(id+"F30.wireOp",EDGE,"E186"),sQuery(id+"F30.wireOp",EDGE,"E188"),sQuery(id+"F30.wireOp",EDGE,"E193.left"),sQuery(id+"F30.wireOp",EDGE,"E193.right"),sQuery(id+"F30.wireOp",EDGE,"E194.left"),sQuery(id+"F30.wireOp",EDGE,"E194.right"),sQuery(id+"F30.wireOp",EDGE,"E195.bottom"),sQuery(id+"F30.wireOp",EDGE,"E195.top"),sQuery(id+"F30.wireOp",EDGE,"E196.trimOffspring"),sQuery(id+"F30.wireOp",EDGE,"E197.trimOffspring"),sQuery(id+"F30.wireOp",EDGE,"E200.trimOffspring"),sQuery(id+"F30.wireOp",EDGE,"E201.trimOffspring"),sQuery(id+"F30.wireOp",EDGE,"E202.trimOffspring"),sQuery(id+"F30.wireOp",EDGE,"E204.trimOffspring"),sQuery(id+"F30.wireOp",EDGE,"E205.trimOffspring"),sQuery(id+"F30.wireOp",EDGE,"E207.trimOffspring"),sQuery(id+"F30.wireOp",EDGE,"E208.bottom"),sQuery(id+"F30.wireOp",EDGE,"E208.top"),subQ0,sQuery(id+"F30.wireOp",EDGE,"E208.right")])],"isStart":true}),makeQuery(id+"F46.opExtrude","SWEPT_FACE",FACE,{"disambiguationData":[OSD([subQ0]),TDD([makeQuery(id+"F31.opExtrude","CAP_EDGE",EDGE,{"disambiguationData":[OSD([subQ0])],"isStart":true})])]})]});}
            extrude(context, id + "F64", {"entities" : qUnion([Q0, Q1]), "operationType" : NewBodyOperationType.ADD, "oppositeDirection" : true, "depth" : 1 * mm});
        }
        {
            var Q0;
            Q0=makeQuery(id+"F33.opExtrude","CAP_FACE",FACE,{"disambiguationData":[OSD([sQuery(id+"F32.wireOp",EDGE,"E209.bottom"),sQuery(id+"F32.wireOp",EDGE,"E209.top"),sQuery(id+"F32.wireOp",EDGE,"E209.left"),sQuery(id+"F32.wireOp",EDGE,"E209.right"),sQuery(id+"F32.wireOp",EDGE,"E210.bottom"),sQuery(id+"F32.wireOp",EDGE,"E210.top"),sQuery(id+"F32.wireOp",EDGE,"E210.left"),sQuery(id+"F32.wireOp",EDGE,"E210.right"),sQuery(id+"F32.wireOp",EDGE,"E213.bottom"),sQuery(id+"F32.wireOp",EDGE,"E213.top"),sQuery(id+"F32.wireOp",EDGE,"E213.left"),sQuery(id+"F32.wireOp",EDGE,"E213.right"),sQuery(id+"F32.wireOp",EDGE,"E216.bottom"),sQuery(id+"F32.wireOp",EDGE,"E216.top"),sQuery(id+"F32.wireOp",EDGE,"E216.left"),sQuery(id+"F32.wireOp",EDGE,"E216.right"),sQuery(id+"F32.wireOp",EDGE,"E219.bottom"),sQuery(id+"F32.wireOp",EDGE,"E219.top"),sQuery(id+"F32.wireOp",EDGE,"E219.left"),sQuery(id+"F32.wireOp",EDGE,"E219.right")])],"isStart":true});
            extrude(context, id + "F65", {"entities" : qUnion([Q0]), "operationType" : NewBodyOperationType.ADD, "depth" : 1 * mm});
        }
        {
            var Q0;
            {var subQ0=sQuery(id+"F38.wireOp",EDGE,"E237.right");var subQ1=sQuery(id+"F38.wireOp",EDGE,"E236.right");var subQ2=sQuery(id+"F36.wireOp",EDGE,"E229.right");Q0=makeQuery(id+"F58.opExtrude","SWEPT_FACE",FACE,{"disambiguationData":[OSD([subQ2,subQ1,subQ0]),TDD([makeQuery(id+"F45.boolean.opBoolean","MERGE",EDGE,{"derivedFrom":[makeQuery(id+"F37.opExtrude","CAP_EDGE",EDGE,{"disambiguationData":[OSD([subQ2])],"isStart":true}),makeQuery(id+"F45.opExtrude","CAP_EDGE",EDGE,{"disambiguationData":[OSD([subQ1])],"isStart":true}),makeQuery(id+"F45.opExtrude","CAP_EDGE",EDGE,{"disambiguationData":[OSD([subQ0])],"isStart":true})]})])]});}
            extrude(context, id + "F66", {"entities" : qUnion([Q0]), "operationType" : NewBodyOperationType.ADD, "depth" : 2 * mm});
        }
        {
            var Q0;
            {var subQ1=sQuery(id+"F11.wireOp",EDGE,"E46.bottom");var subQ2=sQuery(id+"F11.wireOp",EDGE,"E45.right");var subQ3=sQuery(id+"F11.wireOp",EDGE,"E45.top");var subQ4=sQuery(id+"F11.wireOp",EDGE,"E45.bottom");var subQ5=sQuery(id+"F11.wireOp",EDGE,"E44.right");var subQ6=sQuery(id+"F11.wireOp",EDGE,"E44.top");var subQ7=sQuery(id+"F11.wireOp",EDGE,"E44.bottom");var subQ8=sQuery(id+"F11.wireOp",EDGE,"E43.right");var subQ9=sQuery(id+"F11.wireOp",EDGE,"E43.left");var subQ10=sQuery(id+"F11.wireOp",EDGE,"E42.right");var subQ11=sQuery(id+"F11.wireOp",EDGE,"E42.left");var subQ12=sQuery(id+"F11.wireOp",EDGE,"E42.top");var subQ13=makeQuery(id+"F12.opExtrude","CAP_FACE",FACE,{"disambiguationData":[OSD([subQ12,subQ11,subQ10,subQ9,subQ8,subQ7,subQ6,subQ5,subQ4,subQ3,subQ2,subQ1])],"isStart":false});Q0=makeQuery(id+"F44.opFillet","MERGE",FACE,{"derivedFrom":[makeQuery(id+"F12.boolean.opBoolean","SPLIT",FACE,{"disambiguationData":[TD([makeQuery(id+"F12.opExtrude","SWEPT_FACE",FACE,{"disambiguationData":[OSD([subQ12])]})])],"derivedFrom":subQ13}),makeQuery(id+"F12.boolean.opBoolean","SPLIT",FACE,{"disambiguationData":[TD([makeQuery(id+"F12.opExtrude","SWEPT_FACE",FACE,{"disambiguationData":[OSD([subQ1])]})])],"derivedFrom":subQ13}),makeQuery(id+"F12.boolean.opBoolean","SPLIT",FACE,{"disambiguationData":[TD([makeQuery(id+"F12.opExtrude","SWEPT_FACE",FACE,{"disambiguationData":[OSD([subQ5])]})])],"derivedFrom":subQ13}),makeQuery(id+"F12.boolean.opBoolean","SPLIT",FACE,{"disambiguationData":[TD([makeQuery(id+"F12.opExtrude","SWEPT_FACE",FACE,{"disambiguationData":[OSD([subQ2])]})])],"derivedFrom":subQ13})]});}
            extrude(context, id + "F67", {"entities" : qUnion([Q0]), "operationType" : NewBodyOperationType.ADD, "depth" : 0.05 * mm});
        }
        {
            var Q0;
            {var subQ0=sQuery(id+"F30.wireOp",EDGE,"E208.left");var subQ1=sQuery(id+"F30.wireOp",EDGE,"E109.right");var subQ2=sQuery(id+"F30.wireOp",EDGE,"E109.bottom");var subQ4=sQuery(id+"F30.wireOp",EDGE,"E129.trimOffspring");var subQ6=sQuery(id+"F30.wireOp",EDGE,"E208.top");var subQ7=sQuery(id+"F30.wireOp",EDGE,"E130.trimOffspring");var subQ8=sQuery(id+"F30.wireOp",EDGE,"E109.left");var subQ9=sQuery(id+"F30.wireOp",EDGE,"E109.top");var subQ12=sQuery(id+"F30.wireOp",EDGE,"E120.top");var subQ13=sQuery(id+"F30.wireOp",EDGE,"E208.bottom");var subQ15=sQuery(id+"F30.wireOp",EDGE,"E120.bottom");var subQ16=sQuery(id+"F30.wireOp",EDGE,"E126.trimOffspring");var subQ17=sQuery(id+"F30.wireOp",EDGE,"E121.trimOffspring");var subQ19=sQuery(id+"F30.wireOp",EDGE,"E119.right");var subQ21=sQuery(id+"F30.wireOp",EDGE,"E118.right");var subQ23=sQuery(id+"F30.wireOp",EDGE,"E119.left");var subQ24=sQuery(id+"F30.wireOp",EDGE,"E128.trimOffspring");var subQ25=sQuery(id+"F30.wireOp",EDGE,"E127.trimOffspring");var subQ28=sQuery(id+"F30.wireOp",EDGE,"E122.trimOffspring");var subQ29=sQuery(id+"F30.wireOp",EDGE,"E118.left");var subQ30=sQuery(id+"F30.wireOp",EDGE,"E111");var subQ31=sQuery(id+"F30.wireOp",EDGE,"E113");var subQ32=sQuery(id+"F30.wireOp",EDGE,"E125.trimOffspring");Q0=makeQuery(id+"F46.boolean.opBoolean","MERGE",FACE,{"derivedFrom":[makeQuery(id+"F45.boolean.opBoolean","SPLIT",FACE,{"disambiguationData":[TD([makeQuery(id+"F31.opExtrude","SWEPT_FACE",FACE,{"disambiguationData":[OSD([subQ30])]})])],"derivedFrom":makeQuery(id+"F31.opExtrude","CAP_FACE",FACE,{"disambiguationData":[OSD([subQ2,subQ9,subQ8,subQ1,subQ30,subQ31,subQ29,subQ21,subQ23,subQ19,subQ15,subQ12,subQ17,subQ28,subQ32,subQ16,subQ25,subQ24,subQ4,subQ7,sQuery(id+"F30.wireOp",EDGE,"E131.bottom"),sQuery(id+"F30.wireOp",EDGE,"E131.left"),sQuery(id+"F30.wireOp",EDGE,"E131.top"),sQuery(id+"F30.wireOp",EDGE,"E131.right"),sQuery(id+"F30.wireOp",EDGE,"E134"),sQuery(id+"F30.wireOp",EDGE,"E136"),sQuery(id+"F30.wireOp",EDGE,"E141.left"),sQuery(id+"F30.wireOp",EDGE,"E141.right"),sQuery(id+"F30.wireOp",EDGE,"E142.left"),sQuery(id+"F30.wireOp",EDGE,"E142.right"),sQuery(id+"F30.wireOp",EDGE,"E143.bottom"),sQuery(id+"F30.wireOp",EDGE,"E143.top"),sQuery(id+"F30.wireOp",EDGE,"E144.trimOffspring"),sQuery(id+"F30.wireOp",EDGE,"E145.trimOffspring"),sQuery(id+"F30.wireOp",EDGE,"E148.trimOffspring"),sQuery(id+"F30.wireOp",EDGE,"E149.trimOffspring"),sQuery(id+"F30.wireOp",EDGE,"E150.trimOffspring"),sQuery(id+"F30.wireOp",EDGE,"E152.trimOffspring"),sQuery(id+"F30.wireOp",EDGE,"E153.trimOffspring"),sQuery(id+"F30.wireOp",EDGE,"E155.trimOffspring"),sQuery(id+"F30.wireOp",EDGE,"E156.bottom"),sQuery(id+"F30.wireOp",EDGE,"E156.left"),sQuery(id+"F30.wireOp",EDGE,"E156.top"),sQuery(id+"F30.wireOp",EDGE,"E156.right"),sQuery(id+"F30.wireOp",EDGE,"E160"),sQuery(id+"F30.wireOp",EDGE,"E162"),sQuery(id+"F30.wireOp",EDGE,"E167.left"),sQuery(id+"F30.wireOp",EDGE,"E167.right"),sQuery(id+"F30.wireOp",EDGE,"E168.left"),sQuery(id+"F30.wireOp",EDGE,"E168.right"),sQuery(id+"F30.wireOp",EDGE,"E169.bottom"),sQuery(id+"F30.wireOp",EDGE,"E169.top"),sQuery(id+"F30.wireOp",EDGE,"E170.trimOffspring"),sQuery(id+"F30.wireOp",EDGE,"E171.trimOffspring"),sQuery(id+"F30.wireOp",EDGE,"E174.trimOffspring"),sQuery(id+"F30.wireOp",EDGE,"E175.trimOffspring"),sQuery(id+"F30.wireOp",EDGE,"E176.trimOffspring"),sQuery(id+"F30.wireOp",EDGE,"E178.trimOffspring"),sQuery(id+"F30.wireOp",EDGE,"E179.trimOffspring"),sQuery(id+"F30.wireOp",EDGE,"E181.trimOffspring"),sQuery(id+"F30.wireOp",EDGE,"E182.bottom"),sQuery(id+"F30.wireOp",EDGE,"E182.left"),sQuery(id+"F30.wireOp",EDGE,"E182.top"),sQuery(id+"F30.wireOp",EDGE,"E182.right"),sQuery(id+"F30.wireOp",EDGE,"E186"),sQuery(id+"F30.wireOp",EDGE,"E188"),sQuery(id+"F30.wireOp",EDGE,"E193.left"),sQuery(id+"F30.wireOp",EDGE,"E193.right"),sQuery(id+"F30.wireOp",EDGE,"E194.left"),sQuery(id+"F30.wireOp",EDGE,"E194.right"),sQuery(id+"F30.wireOp",EDGE,"E195.bottom"),sQuery(id+"F30.wireOp",EDGE,"E195.top"),sQuery(id+"F30.wireOp",EDGE,"E196.trimOffspring"),sQuery(id+"F30.wireOp",EDGE,"E197.trimOffspring"),sQuery(id+"F30.wireOp",EDGE,"E200.trimOffspring"),sQuery(id+"F30.wireOp",EDGE,"E201.trimOffspring"),sQuery(id+"F30.wireOp",EDGE,"E202.trimOffspring"),sQuery(id+"F30.wireOp",EDGE,"E204.trimOffspring"),sQuery(id+"F30.wireOp",EDGE,"E205.trimOffspring"),sQuery(id+"F30.wireOp",EDGE,"E207.trimOffspring"),subQ13,subQ6,subQ0,sQuery(id+"F30.wireOp",EDGE,"E208.right")])],"isStart":false})}),makeQuery(id+"F46.opExtrude","SWEPT_FACE",FACE,{"disambiguationData":[OSD([subQ0]),TDD([makeQuery(id+"F31.opExtrude","CAP_EDGE",EDGE,{"disambiguationData":[OSD([subQ0])],"isStart":false})])]})]});}
            var sketch = newSketch(context, id + "F68", { "sketchPlane" : qUnion([Q0])});
            skLineSegment(sketch, "E258.bottom", {"start": v(-123.98, -144.56) * mm, "end": v(-117.98, -144.56) * mm, "construction": true});
            skLineSegment(sketch, "E258.top", {"start": v(-123.98, -150.56) * mm, "end": v(-117.98, -150.56) * mm, "construction": true});
            skLineSegment(sketch, "E258.left", {"start": v(-123.98, -144.56) * mm, "end": v(-123.98, -150.56) * mm, "construction": true});
            skLineSegment(sketch, "E258.right", {"start": v(-117.98, -144.56) * mm, "end": v(-117.98, -150.56) * mm, "construction": true});
            skLineSegment(sketch, "E259.bottom", {"start": v(-113.98, -144.56) * mm, "end": v(-107.98, -144.56) * mm, "construction": true});
            skLineSegment(sketch, "E259.top", {"start": v(-113.98, -150.56) * mm, "end": v(-107.98, -150.56) * mm, "construction": true});
            skLineSegment(sketch, "E259.left", {"start": v(-113.98, -144.56) * mm, "end": v(-113.98, -150.56) * mm, "construction": true});
            skLineSegment(sketch, "E259.right", {"start": v(-107.98, -144.56) * mm, "end": v(-107.98, -150.56) * mm, "construction": true});
            skLineSegment(sketch, "E260.bottom", {"start": v(-123.98, -154.56) * mm, "end": v(-117.98, -154.56) * mm, "construction": true});
            skLineSegment(sketch, "E260.top", {"start": v(-123.98, -160.56) * mm, "end": v(-117.98, -160.56) * mm, "construction": true});
            skLineSegment(sketch, "E260.left", {"start": v(-123.98, -154.56) * mm, "end": v(-123.98, -160.56) * mm, "construction": true});
            skLineSegment(sketch, "E260.right", {"start": v(-117.98, -154.56) * mm, "end": v(-117.98, -160.56) * mm, "construction": true});
            skLineSegment(sketch, "E261.bottom", {"start": v(-113.98, -154.56) * mm, "end": v(-107.98, -154.56) * mm, "construction": true});
            skLineSegment(sketch, "E261.top", {"start": v(-113.98, -160.56) * mm, "end": v(-107.98, -160.56) * mm, "construction": true});
            skLineSegment(sketch, "E261.left", {"start": v(-113.98, -154.56) * mm, "end": v(-113.98, -160.56) * mm, "construction": true});
            skLineSegment(sketch, "E261.right", {"start": v(-107.98, -154.56) * mm, "end": v(-107.98, -160.56) * mm, "construction": true});
            skSolve(sketch);
        }
        {
            var Q0;
            Q0=makeQuery(id+"F33.opExtrude","CAP_FACE",FACE,{"disambiguationData":[OSD([sQuery(id+"F32.wireOp",EDGE,"E209.bottom"),sQuery(id+"F32.wireOp",EDGE,"E209.top"),sQuery(id+"F32.wireOp",EDGE,"E209.left"),sQuery(id+"F32.wireOp",EDGE,"E209.right"),sQuery(id+"F32.wireOp",EDGE,"E210.bottom"),sQuery(id+"F32.wireOp",EDGE,"E210.top"),sQuery(id+"F32.wireOp",EDGE,"E210.left"),sQuery(id+"F32.wireOp",EDGE,"E210.right"),sQuery(id+"F32.wireOp",EDGE,"E213.bottom"),sQuery(id+"F32.wireOp",EDGE,"E213.top"),sQuery(id+"F32.wireOp",EDGE,"E213.left"),sQuery(id+"F32.wireOp",EDGE,"E213.right"),sQuery(id+"F32.wireOp",EDGE,"E216.bottom"),sQuery(id+"F32.wireOp",EDGE,"E216.top"),sQuery(id+"F32.wireOp",EDGE,"E216.left"),sQuery(id+"F32.wireOp",EDGE,"E216.right"),sQuery(id+"F32.wireOp",EDGE,"E219.bottom"),sQuery(id+"F32.wireOp",EDGE,"E219.top"),sQuery(id+"F32.wireOp",EDGE,"E219.left"),sQuery(id+"F32.wireOp",EDGE,"E219.right")])],"isStart":false});
            var sketch = newSketch(context, id + "F69", { "sketchPlane" : qUnion([Q0])});
            skLineSegment(sketch, "E262.bottom", {"start": v(22.26, -144.36) * mm, "end": v(42.46, -144.36) * mm});
            skLineSegment(sketch, "E262.top", {"start": v(22.26, -141.36) * mm, "end": v(42.46, -141.36) * mm});
            skLineSegment(sketch, "E262.left", {"start": v(22.26, -144.36) * mm, "end": v(22.26, -141.36) * mm});
            skLineSegment(sketch, "E262.right", {"start": v(42.46, -144.36) * mm, "end": v(42.46, -141.36) * mm});
            skLineSegment(sketch, "E263.bottom", {"start": v(22.26, -164.56) * mm, "end": v(42.46, -164.56) * mm});
            skLineSegment(sketch, "E263.top", {"start": v(22.26, -167.56) * mm, "end": v(42.46, -167.56) * mm});
            skLineSegment(sketch, "E263.left", {"start": v(22.26, -164.56) * mm, "end": v(22.26, -167.56) * mm});
            skLineSegment(sketch, "E263.right", {"start": v(42.46, -164.56) * mm, "end": v(42.46, -167.56) * mm});
            skLineSegment(sketch, "E264.bottom", {"start": v(22.26, -141.36) * mm, "end": v(19.26, -141.36) * mm});
            skLineSegment(sketch, "E264.top", {"start": v(22.26, -167.56) * mm, "end": v(19.26, -167.56) * mm});
            skLineSegment(sketch, "E264.left", {"start": v(22.26, -141.36) * mm, "end": v(22.26, -167.56) * mm});
            skLineSegment(sketch, "E264.right", {"start": v(19.26, -141.36) * mm, "end": v(19.26, -167.56) * mm});
            skLineSegment(sketch, "E265.bottom", {"start": v(42.46, -141.36) * mm, "end": v(45.46, -141.36) * mm});
            skLineSegment(sketch, "E265.top", {"start": v(42.46, -167.56) * mm, "end": v(45.46, -167.56) * mm});
            skLineSegment(sketch, "E265.left", {"start": v(42.46, -141.36) * mm, "end": v(42.46, -167.56) * mm});
            skLineSegment(sketch, "E265.right", {"start": v(45.46, -141.36) * mm, "end": v(45.46, -167.56) * mm});
            skLineSegment(sketch, "E266.bottom", {"start": v(52.26, -144.36) * mm, "end": v(72.46, -144.36) * mm});
            skLineSegment(sketch, "E266.top", {"start": v(52.26, -141.36) * mm, "end": v(72.46, -141.36) * mm});
            skLineSegment(sketch, "E266.left", {"start": v(52.26, -144.36) * mm, "end": v(52.26, -141.36) * mm});
            skLineSegment(sketch, "E266.right", {"start": v(72.46, -144.36) * mm, "end": v(72.46, -141.36) * mm});
            skLineSegment(sketch, "E267.bottom", {"start": v(52.26, -141.36) * mm, "end": v(49.26, -141.36) * mm});
            skLineSegment(sketch, "E267.top", {"start": v(52.26, -167.56) * mm, "end": v(49.26, -167.56) * mm});
            skLineSegment(sketch, "E267.left", {"start": v(52.26, -141.36) * mm, "end": v(52.26, -167.56) * mm});
            skLineSegment(sketch, "E267.right", {"start": v(49.26, -141.36) * mm, "end": v(49.26, -167.56) * mm});
            skLineSegment(sketch, "E268.bottom", {"start": v(52.26, -167.56) * mm, "end": v(72.46, -167.56) * mm});
            skLineSegment(sketch, "E268.top", {"start": v(52.26, -164.56) * mm, "end": v(72.46, -164.56) * mm});
            skLineSegment(sketch, "E268.left", {"start": v(52.26, -167.56) * mm, "end": v(52.26, -164.56) * mm});
            skLineSegment(sketch, "E268.right", {"start": v(72.46, -167.56) * mm, "end": v(72.46, -164.56) * mm});
            skLineSegment(sketch, "E269.bottom", {"start": v(72.46, -167.56) * mm, "end": v(75.46, -167.56) * mm});
            skLineSegment(sketch, "E269.top", {"start": v(72.46, -141.36) * mm, "end": v(75.46, -141.36) * mm});
            skLineSegment(sketch, "E269.left", {"start": v(72.46, -167.56) * mm, "end": v(72.46, -141.36) * mm});
            skLineSegment(sketch, "E269.right", {"start": v(75.46, -167.56) * mm, "end": v(75.46, -141.36) * mm});
            skLineSegment(sketch, "E270.bottom", {"start": v(82.26, -144.36) * mm, "end": v(102.46, -144.36) * mm});
            skLineSegment(sketch, "E270.top", {"start": v(82.26, -141.36) * mm, "end": v(102.46, -141.36) * mm});
            skLineSegment(sketch, "E270.left", {"start": v(82.26, -144.36) * mm, "end": v(82.26, -141.36) * mm});
            skLineSegment(sketch, "E270.right", {"start": v(102.46, -144.36) * mm, "end": v(102.46, -141.36) * mm});
            skLineSegment(sketch, "E271.bottom", {"start": v(82.26, -141.36) * mm, "end": v(79.26, -141.36) * mm});
            skLineSegment(sketch, "E271.top", {"start": v(82.26, -167.56) * mm, "end": v(79.26, -167.56) * mm});
            skLineSegment(sketch, "E271.left", {"start": v(82.26, -141.36) * mm, "end": v(82.26, -167.56) * mm});
            skLineSegment(sketch, "E271.right", {"start": v(79.26, -141.36) * mm, "end": v(79.26, -167.56) * mm});
            skLineSegment(sketch, "E272.bottom", {"start": v(82.26, -167.56) * mm, "end": v(102.46, -167.56) * mm});
            skLineSegment(sketch, "E272.top", {"start": v(82.26, -164.56) * mm, "end": v(102.46, -164.56) * mm});
            skLineSegment(sketch, "E272.left", {"start": v(82.26, -167.56) * mm, "end": v(82.26, -164.56) * mm});
            skLineSegment(sketch, "E272.right", {"start": v(102.46, -167.56) * mm, "end": v(102.46, -164.56) * mm});
            skLineSegment(sketch, "E273.bottom", {"start": v(102.46, -141.36) * mm, "end": v(105.46, -141.36) * mm});
            skLineSegment(sketch, "E273.top", {"start": v(102.46, -167.56) * mm, "end": v(105.46, -167.56) * mm});
            skLineSegment(sketch, "E273.left", {"start": v(102.46, -141.36) * mm, "end": v(102.46, -167.56) * mm});
            skLineSegment(sketch, "E273.right", {"start": v(105.46, -141.36) * mm, "end": v(105.46, -167.56) * mm});
            skLineSegment(sketch, "E274.bottom", {"start": v(112.26, -144.36) * mm, "end": v(132.46, -144.36) * mm});
            skLineSegment(sketch, "E274.top", {"start": v(112.26, -141.36) * mm, "end": v(132.46, -141.36) * mm});
            skLineSegment(sketch, "E274.left", {"start": v(112.26, -144.36) * mm, "end": v(112.26, -141.36) * mm});
            skLineSegment(sketch, "E274.right", {"start": v(132.46, -144.36) * mm, "end": v(132.46, -141.36) * mm});
            skLineSegment(sketch, "E275.bottom", {"start": v(112.26, -141.36) * mm, "end": v(109.26, -141.36) * mm});
            skLineSegment(sketch, "E275.top", {"start": v(112.26, -167.56) * mm, "end": v(109.26, -167.56) * mm});
            skLineSegment(sketch, "E275.left", {"start": v(112.26, -141.36) * mm, "end": v(112.26, -167.56) * mm});
            skLineSegment(sketch, "E275.right", {"start": v(109.26, -141.36) * mm, "end": v(109.26, -167.56) * mm});
            skLineSegment(sketch, "E276.bottom", {"start": v(112.26, -167.56) * mm, "end": v(132.46, -167.56) * mm});
            skLineSegment(sketch, "E276.top", {"start": v(112.26, -164.56) * mm, "end": v(132.46, -164.56) * mm});
            skLineSegment(sketch, "E276.left", {"start": v(112.26, -167.56) * mm, "end": v(112.26, -164.56) * mm});
            skLineSegment(sketch, "E276.right", {"start": v(132.46, -167.56) * mm, "end": v(132.46, -164.56) * mm});
            skLineSegment(sketch, "E277.bottom", {"start": v(132.46, -141.36) * mm, "end": v(135.46, -141.36) * mm});
            skLineSegment(sketch, "E277.top", {"start": v(132.46, -167.56) * mm, "end": v(135.46, -167.56) * mm});
            skLineSegment(sketch, "E277.left", {"start": v(132.46, -141.36) * mm, "end": v(132.46, -167.56) * mm});
            skLineSegment(sketch, "E277.right", {"start": v(135.46, -141.36) * mm, "end": v(135.46, -167.56) * mm});
            skSolve(sketch);
        }
        {
            var Q0;
            Q0=qSketchRegion(id+"F69",true);
            extrude(context, id + "F70", {"entities" : qUnion([Q0]), "operationType" : NewBodyOperationType.ADD, "depth" : 0.5 * mm});
        }
        {
            var Q0;
            Q0=makeQuery(id+"F70.opExtrude","CAP_FACE",FACE,{"disambiguationData":[OSD([sQuery(id+"F69.wireOp",EDGE,"E262.bottom"),sQuery(id+"F69.wireOp",EDGE,"E262.top"),sQuery(id+"F69.wireOp",EDGE,"E263.bottom"),sQuery(id+"F69.wireOp",EDGE,"E263.top"),sQuery(id+"F69.wireOp",EDGE,"E264.bottom"),sQuery(id+"F69.wireOp",EDGE,"E264.top"),sQuery(id+"F69.wireOp",EDGE,"E264.left"),sQuery(id+"F69.wireOp",EDGE,"E264.right"),sQuery(id+"F69.wireOp",EDGE,"E265.bottom"),sQuery(id+"F69.wireOp",EDGE,"E265.top"),sQuery(id+"F69.wireOp",EDGE,"E265.left"),sQuery(id+"F69.wireOp",EDGE,"E265.right")])],"isStart":false});
            var sketch = newSketch(context, id + "F71", { "sketchPlane" : qUnion([Q0])});
            skLineSegment(sketch, "E278.bottom", {"start": v(22.26, -144.36) * mm, "end": v(42.46, -144.36) * mm});
            skLineSegment(sketch, "E278.top", {"start": v(22.26, -142.86) * mm, "end": v(42.46, -142.86) * mm});
            skLineSegment(sketch, "E278.left", {"start": v(22.26, -144.36) * mm, "end": v(22.26, -142.86) * mm});
            skLineSegment(sketch, "E278.right", {"start": v(42.46, -144.36) * mm, "end": v(42.46, -142.86) * mm});
            skLineSegment(sketch, "E279.bottom", {"start": v(22.26, -164.56) * mm, "end": v(42.46, -164.56) * mm});
            skLineSegment(sketch, "E279.top", {"start": v(22.26, -166.06) * mm, "end": v(42.46, -166.06) * mm});
            skLineSegment(sketch, "E279.left", {"start": v(22.26, -164.56) * mm, "end": v(22.26, -166.06) * mm});
            skLineSegment(sketch, "E279.right", {"start": v(42.46, -164.56) * mm, "end": v(42.46, -166.06) * mm});
            skLineSegment(sketch, "E280.bottom", {"start": v(22.26, -166.06) * mm, "end": v(20.76, -166.06) * mm});
            skLineSegment(sketch, "E280.top", {"start": v(22.26, -142.86) * mm, "end": v(20.76, -142.86) * mm});
            skLineSegment(sketch, "E280.left", {"start": v(22.26, -166.06) * mm, "end": v(22.26, -142.86) * mm});
            skLineSegment(sketch, "E280.right", {"start": v(20.76, -166.06) * mm, "end": v(20.76, -142.86) * mm});
            skLineSegment(sketch, "E281.bottom", {"start": v(42.46, -166.06) * mm, "end": v(43.96, -166.06) * mm});
            skLineSegment(sketch, "E281.top", {"start": v(42.46, -142.86) * mm, "end": v(43.96, -142.86) * mm});
            skLineSegment(sketch, "E281.left", {"start": v(42.46, -166.06) * mm, "end": v(42.46, -142.86) * mm});
            skLineSegment(sketch, "E281.right", {"start": v(43.96, -166.06) * mm, "end": v(43.96, -142.86) * mm});
            skLineSegment(sketch, "E282.bottom", {"start": v(50.76, -142.86) * mm, "end": v(52.26, -142.86) * mm});
            skLineSegment(sketch, "E282.top", {"start": v(50.76, -166.06) * mm, "end": v(52.26, -166.06) * mm});
            skLineSegment(sketch, "E282.left", {"start": v(50.76, -142.86) * mm, "end": v(50.76, -166.06) * mm});
            skLineSegment(sketch, "E282.right", {"start": v(52.26, -142.86) * mm, "end": v(52.26, -166.06) * mm});
            skLineSegment(sketch, "E283.bottom", {"start": v(72.46, -142.86) * mm, "end": v(73.96, -142.86) * mm});
            skLineSegment(sketch, "E283.top", {"start": v(72.46, -166.06) * mm, "end": v(73.96, -166.06) * mm});
            skLineSegment(sketch, "E283.left", {"start": v(72.46, -142.86) * mm, "end": v(72.46, -166.06) * mm});
            skLineSegment(sketch, "E283.right", {"start": v(73.96, -142.86) * mm, "end": v(73.96, -166.06) * mm});
            skLineSegment(sketch, "E284.bottom", {"start": v(52.26, -142.86) * mm, "end": v(72.46, -142.86) * mm});
            skLineSegment(sketch, "E284.top", {"start": v(52.26, -144.36) * mm, "end": v(72.46, -144.36) * mm});
            skLineSegment(sketch, "E284.left", {"start": v(52.26, -142.86) * mm, "end": v(52.26, -144.36) * mm});
            skLineSegment(sketch, "E284.right", {"start": v(72.46, -142.86) * mm, "end": v(72.46, -144.36) * mm});
            skLineSegment(sketch, "E285.bottom", {"start": v(52.26, -166.06) * mm, "end": v(72.46, -166.06) * mm});
            skLineSegment(sketch, "E285.top", {"start": v(52.26, -164.56) * mm, "end": v(72.46, -164.56) * mm});
            skLineSegment(sketch, "E285.left", {"start": v(52.26, -166.06) * mm, "end": v(52.26, -164.56) * mm});
            skLineSegment(sketch, "E285.right", {"start": v(72.46, -166.06) * mm, "end": v(72.46, -164.56) * mm});
            skLineSegment(sketch, "E286.bottom", {"start": v(80.76, -142.86) * mm, "end": v(82.26, -142.86) * mm});
            skLineSegment(sketch, "E286.top", {"start": v(80.76, -166.06) * mm, "end": v(82.26, -166.06) * mm});
            skLineSegment(sketch, "E286.left", {"start": v(80.76, -142.86) * mm, "end": v(80.76, -166.06) * mm});
            skLineSegment(sketch, "E286.right", {"start": v(82.26, -142.86) * mm, "end": v(82.26, -166.06) * mm});
            skLineSegment(sketch, "E287.bottom", {"start": v(82.26, -142.86) * mm, "end": v(102.46, -142.86) * mm});
            skLineSegment(sketch, "E287.top", {"start": v(82.26, -144.36) * mm, "end": v(102.46, -144.36) * mm});
            skLineSegment(sketch, "E287.left", {"start": v(82.26, -142.86) * mm, "end": v(82.26, -144.36) * mm});
            skLineSegment(sketch, "E287.right", {"start": v(102.46, -142.86) * mm, "end": v(102.46, -144.36) * mm});
            skLineSegment(sketch, "E288.bottom", {"start": v(82.26, -166.06) * mm, "end": v(102.46, -166.06) * mm});
            skLineSegment(sketch, "E288.top", {"start": v(82.26, -164.56) * mm, "end": v(102.46, -164.56) * mm});
            skLineSegment(sketch, "E288.left", {"start": v(82.26, -166.06) * mm, "end": v(82.26, -164.56) * mm});
            skLineSegment(sketch, "E288.right", {"start": v(102.46, -166.06) * mm, "end": v(102.46, -164.56) * mm});
            skLineSegment(sketch, "E289.bottom", {"start": v(102.46, -166.06) * mm, "end": v(103.96, -166.06) * mm});
            skLineSegment(sketch, "E289.top", {"start": v(102.46, -142.86) * mm, "end": v(103.96, -142.86) * mm});
            skLineSegment(sketch, "E289.left", {"start": v(102.46, -166.06) * mm, "end": v(102.46, -142.86) * mm});
            skLineSegment(sketch, "E289.right", {"start": v(103.96, -166.06) * mm, "end": v(103.96, -142.86) * mm});
            skLineSegment(sketch, "E290.bottom", {"start": v(110.76, -142.86) * mm, "end": v(112.26, -142.86) * mm});
            skLineSegment(sketch, "E290.top", {"start": v(110.76, -166.06) * mm, "end": v(112.26, -166.06) * mm});
            skLineSegment(sketch, "E290.left", {"start": v(110.76, -142.86) * mm, "end": v(110.76, -166.06) * mm});
            skLineSegment(sketch, "E290.right", {"start": v(112.26, -142.86) * mm, "end": v(112.26, -166.06) * mm});
            skLineSegment(sketch, "E291.bottom", {"start": v(112.26, -142.86) * mm, "end": v(132.46, -142.86) * mm});
            skLineSegment(sketch, "E291.top", {"start": v(112.26, -144.36) * mm, "end": v(132.46, -144.36) * mm});
            skLineSegment(sketch, "E291.left", {"start": v(112.26, -142.86) * mm, "end": v(112.26, -144.36) * mm});
            skLineSegment(sketch, "E291.right", {"start": v(132.46, -142.86) * mm, "end": v(132.46, -144.36) * mm});
            skLineSegment(sketch, "E292.bottom", {"start": v(112.26, -166.06) * mm, "end": v(132.46, -166.06) * mm});
            skLineSegment(sketch, "E292.top", {"start": v(112.26, -164.56) * mm, "end": v(132.46, -164.56) * mm});
            skLineSegment(sketch, "E292.left", {"start": v(112.26, -166.06) * mm, "end": v(112.26, -164.56) * mm});
            skLineSegment(sketch, "E292.right", {"start": v(132.46, -166.06) * mm, "end": v(132.46, -164.56) * mm});
            skLineSegment(sketch, "E293.bottom", {"start": v(132.46, -166.06) * mm, "end": v(133.96, -166.06) * mm});
            skLineSegment(sketch, "E293.top", {"start": v(132.46, -142.86) * mm, "end": v(133.96, -142.86) * mm});
            skLineSegment(sketch, "E293.left", {"start": v(132.46, -166.06) * mm, "end": v(132.46, -142.86) * mm});
            skLineSegment(sketch, "E293.right", {"start": v(133.96, -166.06) * mm, "end": v(133.96, -142.86) * mm});
            skSolve(sketch);
        }
        {
            var Q0;
            Q0=qSketchRegion(id+"F71",true);
            extrude(context, id + "F72", {"entities" : qUnion([Q0]), "operationType" : NewBodyOperationType.ADD, "depth" : 1 * mm});
        }
        {
            var Q0;
            Q0=makeQuery(id+"F70.opExtrude","SWEPT_EDGE",EDGE,{"disambiguationData":[OSD([sQuery(id+"F69.wireOp",EDGE,"E264.bottom"),sQuery(id+"F69.wireOp",EDGE,"E264.right")])]});
            var Q1;
            Q1=makeQuery(id+"F72.opExtrude","SWEPT_EDGE",EDGE,{"disambiguationData":[OSD([sQuery(id+"F71.wireOp",EDGE,"E280.top"),sQuery(id+"F71.wireOp",EDGE,"E280.right")])]});
            var Q2;
            Q2=makeQuery(id+"F70.opExtrude","SWEPT_EDGE",EDGE,{"disambiguationData":[OSD([sQuery(id+"F69.wireOp",EDGE,"E264.top"),sQuery(id+"F69.wireOp",EDGE,"E264.right")])]});
            var Q3;
            Q3=makeQuery(id+"F72.opExtrude","SWEPT_EDGE",EDGE,{"disambiguationData":[OSD([sQuery(id+"F71.wireOp",EDGE,"E280.bottom"),sQuery(id+"F71.wireOp",EDGE,"E280.right")])]});
            var Q4;
            Q4=makeQuery(id+"F72.opExtrude","SWEPT_EDGE",EDGE,{"disambiguationData":[OSD([sQuery(id+"F71.wireOp",EDGE,"E281.bottom"),sQuery(id+"F71.wireOp",EDGE,"E281.right")])]});
            var Q5;
            Q5=makeQuery(id+"F70.opExtrude","SWEPT_EDGE",EDGE,{"disambiguationData":[OSD([sQuery(id+"F69.wireOp",EDGE,"E265.top"),sQuery(id+"F69.wireOp",EDGE,"E265.right")])]});
            var Q6;
            Q6=makeQuery(id+"F72.opExtrude","SWEPT_EDGE",EDGE,{"disambiguationData":[OSD([sQuery(id+"F71.wireOp",EDGE,"E281.top"),sQuery(id+"F71.wireOp",EDGE,"E281.right")])]});
            var Q7;
            Q7=makeQuery(id+"F70.opExtrude","SWEPT_EDGE",EDGE,{"disambiguationData":[OSD([sQuery(id+"F69.wireOp",EDGE,"E265.bottom"),sQuery(id+"F69.wireOp",EDGE,"E265.right")])]});
            var Q8;
            Q8=makeQuery(id+"F70.opExtrude","SWEPT_EDGE",EDGE,{"disambiguationData":[OSD([sQuery(id+"F69.wireOp",EDGE,"E267.bottom"),sQuery(id+"F69.wireOp",EDGE,"E267.right")])]});
            var Q9;
            Q9=makeQuery(id+"F72.opExtrude","SWEPT_EDGE",EDGE,{"disambiguationData":[OSD([sQuery(id+"F71.wireOp",EDGE,"E282.bottom"),sQuery(id+"F71.wireOp",EDGE,"E282.left")])]});
            var Q10;
            Q10=makeQuery(id+"F72.opExtrude","SWEPT_EDGE",EDGE,{"disambiguationData":[OSD([sQuery(id+"F71.wireOp",EDGE,"E282.top"),sQuery(id+"F71.wireOp",EDGE,"E282.left")])]});
            var Q11;
            Q11=makeQuery(id+"F70.opExtrude","SWEPT_EDGE",EDGE,{"disambiguationData":[OSD([sQuery(id+"F69.wireOp",EDGE,"E267.top"),sQuery(id+"F69.wireOp",EDGE,"E267.right")])]});
            var Q12;
            Q12=makeQuery(id+"F72.opExtrude","SWEPT_EDGE",EDGE,{"disambiguationData":[OSD([sQuery(id+"F71.wireOp",EDGE,"E283.top"),sQuery(id+"F71.wireOp",EDGE,"E283.right")])]});
            var Q13;
            Q13=makeQuery(id+"F70.opExtrude","SWEPT_EDGE",EDGE,{"disambiguationData":[OSD([sQuery(id+"F69.wireOp",EDGE,"E269.bottom"),sQuery(id+"F69.wireOp",EDGE,"E269.right")])]});
            var Q14;
            Q14=makeQuery(id+"F72.opExtrude","SWEPT_EDGE",EDGE,{"disambiguationData":[OSD([sQuery(id+"F71.wireOp",EDGE,"E283.bottom"),sQuery(id+"F71.wireOp",EDGE,"E283.right")])]});
            var Q15;
            Q15=makeQuery(id+"F70.opExtrude","SWEPT_EDGE",EDGE,{"disambiguationData":[OSD([sQuery(id+"F69.wireOp",EDGE,"E269.top"),sQuery(id+"F69.wireOp",EDGE,"E269.right")])]});
            var Q16;
            Q16=makeQuery(id+"F70.opExtrude","SWEPT_EDGE",EDGE,{"disambiguationData":[OSD([sQuery(id+"F69.wireOp",EDGE,"E271.bottom"),sQuery(id+"F69.wireOp",EDGE,"E271.right")])]});
            var Q17;
            Q17=makeQuery(id+"F72.opExtrude","SWEPT_EDGE",EDGE,{"disambiguationData":[OSD([sQuery(id+"F71.wireOp",EDGE,"E286.bottom"),sQuery(id+"F71.wireOp",EDGE,"E286.left")])]});
            var Q18;
            Q18=makeQuery(id+"F70.opExtrude","SWEPT_EDGE",EDGE,{"disambiguationData":[OSD([sQuery(id+"F69.wireOp",EDGE,"E271.top"),sQuery(id+"F69.wireOp",EDGE,"E271.right")])]});
            var Q19;
            Q19=makeQuery(id+"F72.opExtrude","SWEPT_EDGE",EDGE,{"disambiguationData":[OSD([sQuery(id+"F71.wireOp",EDGE,"E286.top"),sQuery(id+"F71.wireOp",EDGE,"E286.left")])]});
            var Q20;
            Q20=makeQuery(id+"F72.opExtrude","SWEPT_EDGE",EDGE,{"disambiguationData":[OSD([sQuery(id+"F71.wireOp",EDGE,"E289.bottom"),sQuery(id+"F71.wireOp",EDGE,"E289.right")])]});
            var Q21;
            Q21=makeQuery(id+"F70.opExtrude","SWEPT_EDGE",EDGE,{"disambiguationData":[OSD([sQuery(id+"F69.wireOp",EDGE,"E273.top"),sQuery(id+"F69.wireOp",EDGE,"E273.right")])]});
            var Q22;
            Q22=makeQuery(id+"F72.opExtrude","SWEPT_EDGE",EDGE,{"disambiguationData":[OSD([sQuery(id+"F71.wireOp",EDGE,"E289.top"),sQuery(id+"F71.wireOp",EDGE,"E289.right")])]});
            var Q23;
            Q23=makeQuery(id+"F70.opExtrude","SWEPT_EDGE",EDGE,{"disambiguationData":[OSD([sQuery(id+"F69.wireOp",EDGE,"E273.bottom"),sQuery(id+"F69.wireOp",EDGE,"E273.right")])]});
            var Q24;
            Q24=makeQuery(id+"F70.opExtrude","SWEPT_EDGE",EDGE,{"disambiguationData":[OSD([sQuery(id+"F69.wireOp",EDGE,"E275.bottom"),sQuery(id+"F69.wireOp",EDGE,"E275.right")])]});
            var Q25;
            Q25=makeQuery(id+"F72.opExtrude","SWEPT_EDGE",EDGE,{"disambiguationData":[OSD([sQuery(id+"F71.wireOp",EDGE,"E290.bottom"),sQuery(id+"F71.wireOp",EDGE,"E290.left")])]});
            var Q26;
            Q26=makeQuery(id+"F70.opExtrude","SWEPT_EDGE",EDGE,{"disambiguationData":[OSD([sQuery(id+"F69.wireOp",EDGE,"E275.top"),sQuery(id+"F69.wireOp",EDGE,"E275.right")])]});
            var Q27;
            Q27=makeQuery(id+"F72.opExtrude","SWEPT_EDGE",EDGE,{"disambiguationData":[OSD([sQuery(id+"F71.wireOp",EDGE,"E290.top"),sQuery(id+"F71.wireOp",EDGE,"E290.left")])]});
            var Q28;
            Q28=makeQuery(id+"F72.opExtrude","SWEPT_EDGE",EDGE,{"disambiguationData":[OSD([sQuery(id+"F71.wireOp",EDGE,"E293.bottom"),sQuery(id+"F71.wireOp",EDGE,"E293.right")])]});
            var Q29;
            Q29=makeQuery(id+"F70.opExtrude","SWEPT_EDGE",EDGE,{"disambiguationData":[OSD([sQuery(id+"F69.wireOp",EDGE,"E277.top"),sQuery(id+"F69.wireOp",EDGE,"E277.right")])]});
            var Q30;
            Q30=makeQuery(id+"F72.opExtrude","SWEPT_EDGE",EDGE,{"disambiguationData":[OSD([sQuery(id+"F71.wireOp",EDGE,"E293.top"),sQuery(id+"F71.wireOp",EDGE,"E293.right")])]});
            var Q31;
            Q31=makeQuery(id+"F70.opExtrude","SWEPT_EDGE",EDGE,{"disambiguationData":[OSD([sQuery(id+"F69.wireOp",EDGE,"E277.bottom"),sQuery(id+"F69.wireOp",EDGE,"E277.right")])]});
            fillet(context, id + "F73", {"entities" : qUnion([Q0, Q1, Q2, Q3, Q4, Q5, Q6, Q7, Q8, Q9, Q10, Q11, Q12, Q13, Q14, Q15, Q16, Q17, Q18, Q19, Q20, Q21, Q22, Q23, Q24, Q25, Q26, Q27, Q28, Q29, Q30, Q31]), "radius" : 0.5 * mm, "tangentPropagation" : true, "allowEdgeOverflow" : false});
        }
        {
            var Q0;
            Q0=makeQuery(id+"F10.opExtrude","CAP_FACE",FACE,{"disambiguationData":[OSD([sQuery(id+"F9.wireOp",EDGE,"E41.bottom"),sQuery(id+"F9.wireOp",EDGE,"E41.top"),sQuery(id+"F9.wireOp",EDGE,"E41.left"),sQuery(id+"F9.wireOp",EDGE,"E41.right")])],"isStart":false});
            var sketch = newSketch(context, id + "F74", { "sketchPlane" : qUnion([Q0])});
            skLineSegment(sketch, "E294.bottom", {"start": v(-87.88, 7.7) * mm, "end": v(-69.88, 7.7) * mm});
            skLineSegment(sketch, "E294.top", {"start": v(-87.88, -10.3) * mm, "end": v(-69.88, -10.3) * mm});
            skLineSegment(sketch, "E294.left", {"start": v(-87.88, 7.7) * mm, "end": v(-87.88, -10.3) * mm});
            skLineSegment(sketch, "E294.right", {"start": v(-69.88, 7.7) * mm, "end": v(-69.88, -10.3) * mm});
            skSolve(sketch);
        }
        {
            var Q0;
            Q0 = qSketchRegion(id + "F74", true);
            extrude(context, id + "F75", {"entities" : qUnion([Q0]), "operationType" : NewBodyOperationType.REMOVE, "oppositeDirection" : true, "depth" : 1 * mm});
        }
        {
            var Q0;
            Q0=qCreatedBy(makeId("Top.planeOp"),FACE);
            var sketch = newSketch(context, id + "F76", { "sketchPlane" : qUnion([Q0])});
            skLineSegment(sketch, "E295.bottom", {"start": v(-55.36, 28.3) * mm, "end": v(-37.36, 28.3) * mm});
            skLineSegment(sketch, "E295.top", {"start": v(-55.36, 10.3) * mm, "end": v(-37.36, 10.3) * mm});
            skLineSegment(sketch, "E295.left", {"start": v(-55.36, 28.3) * mm, "end": v(-55.36, 10.3) * mm});
            skLineSegment(sketch, "E295.right", {"start": v(-37.36, 28.3) * mm, "end": v(-37.36, 10.3) * mm});
            skSolve(sketch);
        }
        {
            var Q0;
            Q0 = qSketchRegion(id + "F76", true);
            extrude(context, id + "F77", {"entities" : qUnion([Q0]), "depth" : 1 * mm});
        }
        {
            var Q0;
            Q0=makeQuery(id+"F1.opExtrude","CAP_FACE",FACE,{"disambiguationData":[OSD([sQuery(id+"F0.wireOp",EDGE,"E1.bottom"),sQuery(id+"F0.wireOp",EDGE,"E1.top"),sQuery(id+"F0.wireOp",EDGE,"E1.left"),sQuery(id+"F0.wireOp",EDGE,"E1.right")])],"isStart":false});
            var sketch = newSketch(context, id + "F78", { "sketchPlane" : qUnion([Q0])});
            skLineSegment(sketch, "E296.bottom", {"start": v(9, 9) * mm, "end": v(-9, 9) * mm});
            skLineSegment(sketch, "E296.top", {"start": v(9, -9) * mm, "end": v(-9, -9) * mm});
            skLineSegment(sketch, "E296.left", {"start": v(9, 9) * mm, "end": v(9, -9) * mm});
            skLineSegment(sketch, "E296.right", {"start": v(-9, 9) * mm, "end": v(-9, -9) * mm});
            skPoint(sketch, "E296.middle", {"position": v(0, 0) * mm});
            skSolve(sketch);
        }
        {
            var Q0;
            Q0 = qSketchRegion(id + "F78", true);
            extrude(context, id + "F79", {"entities" : qUnion([Q0]), "operationType" : NewBodyOperationType.REMOVE, "oppositeDirection" : true, "depth" : 1 * mm});
        }
    });
